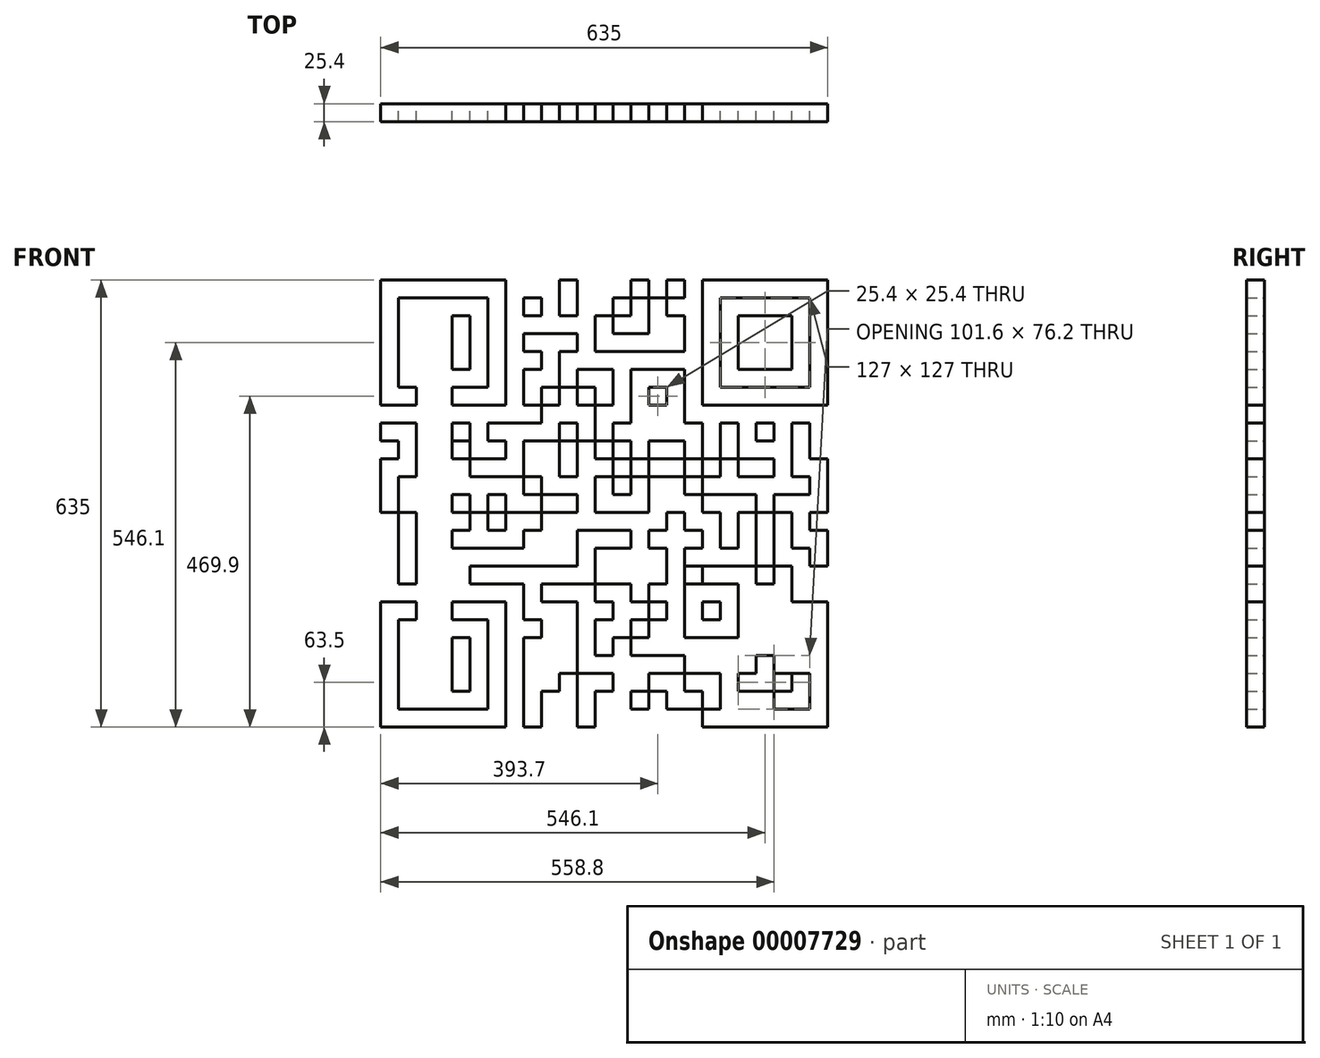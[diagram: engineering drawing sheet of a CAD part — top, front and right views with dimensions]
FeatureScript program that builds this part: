
annotation { "Feature Type Name" : "Feature", "Feature Type Description" : "" }
export const myFeature = defineFeature(function(context is Context, id is Id, definition is map)
    precondition{}
    {
        {
            var Q0;
            Q0=qCreatedBy(makeId("Front.planeOp"),FACE);
            var sketch = newSketch(context, id + "F0", { "sketchPlane" : qUnion([Q0])});
            skLineSegment(sketch, "E0", {"start": v(25.4, 635) * mm, "end": v(25.4, 0) * mm});
            skLineSegment(sketch, "E1", {"start": v(25.4, 0) * mm, "end": v(50.8, 0) * mm});
            skLineSegment(sketch, "E2", {"start": v(50.8, 0) * mm, "end": v(50.8, 635) * mm});
            skLineSegment(sketch, "E3.bottom", {"start": v(50.8, 635) * mm, "end": v(76.2, 635) * mm});
            skLineSegment(sketch, "E3.top", {"start": v(50.8, 0) * mm, "end": v(50.8, 0) * mm});
            skLineSegment(sketch, "E3.left", {"start": v(50.8, 635) * mm, "end": v(50.8, 0) * mm});
            skLineSegment(sketch, "E3.right", {"start": v(76.2, 635) * mm, "end": v(76.2, 0) * mm});
            skLineSegment(sketch, "E4.bottom", {"start": v(76.2, 0) * mm, "end": v(76.2, 0) * mm});
            skLineSegment(sketch, "E4.top", {"start": v(76.2, 635) * mm, "end": v(101.6, 635) * mm});
            skLineSegment(sketch, "E4.left", {"start": v(76.2, 0) * mm, "end": v(76.2, 635) * mm});
            skLineSegment(sketch, "E4.right", {"start": v(101.6, 0) * mm, "end": v(101.6, 0) * mm});
            skLineSegment(sketch, "E5.bottom", {"start": v(127, 635) * mm, "end": v(152.4, 635) * mm});
            skLineSegment(sketch, "E5.top", {"start": v(127, 0) * mm, "end": v(127, 0) * mm});
            skLineSegment(sketch, "E5.left", {"start": v(127, 635) * mm, "end": v(127, 0) * mm});
            skLineSegment(sketch, "E5.right", {"start": v(152.4, 635) * mm, "end": v(152.4, 0) * mm});
            skLineSegment(sketch, "E6.bottom", {"start": v(177.8, 0) * mm, "end": v(203.2, 0) * mm});
            skLineSegment(sketch, "E6.top", {"start": v(177.8, 635) * mm, "end": v(203.2, 635) * mm});
            skLineSegment(sketch, "E6.left", {"start": v(177.8, 0) * mm, "end": v(177.8, 0) * mm});
            skLineSegment(sketch, "E6.right", {"start": v(203.2, 0) * mm, "end": v(203.2, 635) * mm});
            skLineSegment(sketch, "E7.bottom", {"start": v(228.6, 635) * mm, "end": v(254, 635) * mm});
            skLineSegment(sketch, "E7.top", {"start": v(228.6, 0) * mm, "end": v(254, 0) * mm});
            skLineSegment(sketch, "E7.left", {"start": v(228.6, 635) * mm, "end": v(228.6, 0) * mm});
            skLineSegment(sketch, "E7.right", {"start": v(254, 635) * mm, "end": v(254, 0) * mm});
            skLineSegment(sketch, "E8.top", {"start": v(279.4, 635) * mm, "end": v(330.2, 635) * mm});
            skLineSegment(sketch, "E8.left", {"start": v(279.4, 0) * mm, "end": v(279.4, 635) * mm});
            skLineSegment(sketch, "E8.right", {"start": v(330.2, 0) * mm, "end": v(330.2, 635) * mm});
            skLineSegment(sketch, "E9.bottom", {"start": v(355.6, 635) * mm, "end": v(381, 635) * mm});
            skLineSegment(sketch, "E9.left", {"start": v(355.6, 635) * mm, "end": v(355.6, 0) * mm});
            skLineSegment(sketch, "E9.right", {"start": v(381, 635) * mm, "end": v(381, 0) * mm});
            skLineSegment(sketch, "E10.bottom", {"start": v(330.2, 0) * mm, "end": v(304.8, 0) * mm});
            skLineSegment(sketch, "E10.top", {"start": v(330.2, 635) * mm, "end": v(304.8, 635) * mm});
            skLineSegment(sketch, "E10.right", {"start": v(304.8, 0) * mm, "end": v(304.8, 635) * mm});
            skLineSegment(sketch, "E11.bottom", {"start": v(406.4, 635) * mm, "end": v(431.8, 635) * mm});
            skLineSegment(sketch, "E11.left", {"start": v(406.4, 635) * mm, "end": v(406.4, 0) * mm});
            skLineSegment(sketch, "E11.right", {"start": v(431.8, 635) * mm, "end": v(431.8, 0) * mm});
            skLineSegment(sketch, "E12.bottom", {"start": v(457.2, 635) * mm, "end": v(482.6, 635) * mm});
            skLineSegment(sketch, "E12.left", {"start": v(457.2, 635) * mm, "end": v(457.2, 0) * mm});
            skLineSegment(sketch, "E12.right", {"start": v(482.6, 635) * mm, "end": v(482.6, 0) * mm});
            skLineSegment(sketch, "E13.top", {"start": v(508, 635) * mm, "end": v(533.4, 635) * mm});
            skLineSegment(sketch, "E13.left", {"start": v(508, 0) * mm, "end": v(508, 635) * mm});
            skLineSegment(sketch, "E13.right", {"start": v(533.4, 0) * mm, "end": v(533.4, 635) * mm});
            skLineSegment(sketch, "E14.bottom", {"start": v(558.8, 635) * mm, "end": v(584.2, 635) * mm});
            skLineSegment(sketch, "E14.left", {"start": v(558.8, 635) * mm, "end": v(558.8, 0) * mm});
            skLineSegment(sketch, "E14.right", {"start": v(584.2, 635) * mm, "end": v(584.2, 0) * mm});
            skLineSegment(sketch, "E15.top", {"start": v(0, 609.6) * mm, "end": v(635, 609.6) * mm});
            skLineSegment(sketch, "E15.left", {"start": v(0, 635) * mm, "end": v(0, 609.6) * mm});
            skLineSegment(sketch, "E15.right", {"start": v(609.6, 635) * mm, "end": v(609.6, 609.6) * mm});
            skLineSegment(sketch, "E16.bottom", {"start": v(635, 584.2) * mm, "end": v(0, 584.2) * mm});
            skLineSegment(sketch, "E16.top", {"start": v(635, 558.8) * mm, "end": v(0, 558.8) * mm});
            skLineSegment(sketch, "E16.left", {"start": v(609.6, 584.2) * mm, "end": v(609.6, 558.8) * mm});
            skLineSegment(sketch, "E16.right", {"start": v(0, 584.2) * mm, "end": v(0, 558.8) * mm});
            skLineSegment(sketch, "E17.bottom", {"start": v(0, 533.4) * mm, "end": v(635, 533.4) * mm});
            skLineSegment(sketch, "E17.top", {"start": v(0, 508) * mm, "end": v(635, 508) * mm});
            skLineSegment(sketch, "E17.left", {"start": v(0, 533.4) * mm, "end": v(0, 508) * mm});
            skLineSegment(sketch, "E17.right", {"start": v(609.6, 533.4) * mm, "end": v(609.6, 508) * mm});
            skLineSegment(sketch, "E18.bottom", {"start": v(635, 482.6) * mm, "end": v(0, 482.6) * mm});
            skLineSegment(sketch, "E18.top", {"start": v(635, 457.2) * mm, "end": v(0, 457.2) * mm});
            skLineSegment(sketch, "E18.left", {"start": v(609.6, 482.6) * mm, "end": v(609.6, 457.2) * mm});
            skLineSegment(sketch, "E18.right", {"start": v(0, 482.6) * mm, "end": v(0, 457.2) * mm});
            skLineSegment(sketch, "E19.bottom", {"start": v(0, 431.8) * mm, "end": v(635, 431.8) * mm});
            skLineSegment(sketch, "E19.top", {"start": v(0, 406.4) * mm, "end": v(635, 406.4) * mm});
            skLineSegment(sketch, "E19.left", {"start": v(0, 431.8) * mm, "end": v(0, 406.4) * mm});
            skLineSegment(sketch, "E19.right", {"start": v(609.6, 431.8) * mm, "end": v(609.6, 406.4) * mm});
            skLineSegment(sketch, "E20.bottom", {"start": v(635, 381) * mm, "end": v(0, 381) * mm});
            skLineSegment(sketch, "E20.top", {"start": v(635, 355.6) * mm, "end": v(0, 355.6) * mm});
            skLineSegment(sketch, "E20.left", {"start": v(609.6, 381) * mm, "end": v(609.6, 355.6) * mm});
            skLineSegment(sketch, "E20.right", {"start": v(0, 381) * mm, "end": v(0, 355.6) * mm});
            skLineSegment(sketch, "E21.bottom", {"start": v(0, 330.2) * mm, "end": v(635, 330.2) * mm});
            skLineSegment(sketch, "E21.top", {"start": v(0, 304.8) * mm, "end": v(635, 304.8) * mm});
            skLineSegment(sketch, "E21.left", {"start": v(0, 330.2) * mm, "end": v(0, 304.8) * mm});
            skLineSegment(sketch, "E21.right", {"start": v(609.6, 330.2) * mm, "end": v(609.6, 304.8) * mm});
            skLineSegment(sketch, "E22.bottom", {"start": v(635, 279.4) * mm, "end": v(0, 279.4) * mm});
            skLineSegment(sketch, "E22.top", {"start": v(635, 254) * mm, "end": v(0, 254) * mm});
            skLineSegment(sketch, "E22.left", {"start": v(609.6, 279.4) * mm, "end": v(609.6, 254) * mm});
            skLineSegment(sketch, "E22.right", {"start": v(0, 279.4) * mm, "end": v(0, 254) * mm});
            skLineSegment(sketch, "E23.bottom", {"start": v(0, 228.6) * mm, "end": v(635, 228.6) * mm});
            skLineSegment(sketch, "E23.top", {"start": v(0, 203.2) * mm, "end": v(635, 203.2) * mm});
            skLineSegment(sketch, "E23.left", {"start": v(0, 228.6) * mm, "end": v(0, 203.2) * mm});
            skLineSegment(sketch, "E23.right", {"start": v(609.6, 228.6) * mm, "end": v(609.6, 203.2) * mm});
            skLineSegment(sketch, "E24.bottom", {"start": v(635, 177.8) * mm, "end": v(0, 177.8) * mm});
            skLineSegment(sketch, "E24.top", {"start": v(635, 152.4) * mm, "end": v(0, 152.4) * mm});
            skLineSegment(sketch, "E24.left", {"start": v(609.6, 177.8) * mm, "end": v(609.6, 152.4) * mm});
            skLineSegment(sketch, "E24.right", {"start": v(0, 177.8) * mm, "end": v(0, 152.4) * mm});
            skLineSegment(sketch, "E25.bottom", {"start": v(0, 127) * mm, "end": v(635, 127) * mm});
            skLineSegment(sketch, "E25.top", {"start": v(0, 101.6) * mm, "end": v(635, 101.6) * mm});
            skLineSegment(sketch, "E25.left", {"start": v(0, 127) * mm, "end": v(0, 101.6) * mm});
            skLineSegment(sketch, "E25.right", {"start": v(609.6, 127) * mm, "end": v(609.6, 101.6) * mm});
            skLineSegment(sketch, "E26.bottom", {"start": v(635, 76.2) * mm, "end": v(0, 76.2) * mm});
            skLineSegment(sketch, "E26.top", {"start": v(635, 50.8) * mm, "end": v(0, 50.8) * mm});
            skLineSegment(sketch, "E26.left", {"start": v(609.6, 76.2) * mm, "end": v(609.6, 50.8) * mm});
            skLineSegment(sketch, "E26.right", {"start": v(0, 76.2) * mm, "end": v(0, 50.8) * mm});
            skLineSegment(sketch, "E27.bottom", {"start": v(0, 25.4) * mm, "end": v(635, 25.4) * mm});
            skLineSegment(sketch, "E28", {"start": v(0, 635) * mm, "end": v(25.4, 635) * mm});
            skLineSegment(sketch, "E29", {"start": v(25.4, 635) * mm, "end": v(50.8, 635) * mm});
            skLineSegment(sketch, "E30", {"start": v(101.6, 635) * mm, "end": v(127, 635) * mm});
            skLineSegment(sketch, "E31", {"start": v(50.8, 0) * mm, "end": v(76.2, 0) * mm});
            skLineSegment(sketch, "E32", {"start": v(76.2, 0) * mm, "end": v(101.6, 0) * mm});
            skLineSegment(sketch, "E33", {"start": v(101.6, 0) * mm, "end": v(101.6, 635) * mm});
            skLineSegment(sketch, "E34", {"start": v(177.8, 0) * mm, "end": v(177.8, 635) * mm});
            skLineSegment(sketch, "E35", {"start": v(152.4, 635) * mm, "end": v(177.8, 635) * mm});
            skLineSegment(sketch, "E36", {"start": v(203.2, 635) * mm, "end": v(228.6, 635) * mm});
            skLineSegment(sketch, "E37", {"start": v(254, 635) * mm, "end": v(279.4, 635) * mm});
            skLineSegment(sketch, "E38", {"start": v(330.2, 635) * mm, "end": v(355.6, 635) * mm});
            skLineSegment(sketch, "E39", {"start": v(381, 635) * mm, "end": v(406.4, 635) * mm});
            skLineSegment(sketch, "E40", {"start": v(431.8, 635) * mm, "end": v(457.2, 635) * mm});
            skLineSegment(sketch, "E41", {"start": v(482.6, 635) * mm, "end": v(508, 635) * mm});
            skLineSegment(sketch, "E42", {"start": v(533.4, 635) * mm, "end": v(558.8, 635) * mm});
            skLineSegment(sketch, "E43", {"start": v(584.2, 635) * mm, "end": v(609.6, 635) * mm});
            skLineSegment(sketch, "E44", {"start": v(0, 609.6) * mm, "end": v(0, 584.2) * mm});
            skLineSegment(sketch, "E45", {"start": v(0, 558.8) * mm, "end": v(0, 533.4) * mm});
            skLineSegment(sketch, "E46", {"start": v(0, 508) * mm, "end": v(0, 482.6) * mm});
            skLineSegment(sketch, "E47", {"start": v(0, 457.2) * mm, "end": v(0, 431.8) * mm});
            skLineSegment(sketch, "E48", {"start": v(0, 406.4) * mm, "end": v(0, 381) * mm});
            skLineSegment(sketch, "E49", {"start": v(0, 355.6) * mm, "end": v(0, 330.2) * mm});
            skLineSegment(sketch, "E50", {"start": v(0, 304.8) * mm, "end": v(0, 279.4) * mm});
            skLineSegment(sketch, "E51", {"start": v(0, 254) * mm, "end": v(0, 228.6) * mm});
            skLineSegment(sketch, "E52", {"start": v(25.4, 0) * mm, "end": v(0, 0) * mm});
            skLineSegment(sketch, "E53", {"start": v(0, 0) * mm, "end": v(0, 25.4) * mm});
            skLineSegment(sketch, "E54", {"start": v(0, 50.8) * mm, "end": v(0, 25.4) * mm});
            skLineSegment(sketch, "E55", {"start": v(0, 76.2) * mm, "end": v(0, 101.6) * mm});
            skLineSegment(sketch, "E56", {"start": v(0, 127) * mm, "end": v(0, 152.4) * mm});
            skLineSegment(sketch, "E57", {"start": v(0, 177.8) * mm, "end": v(0, 203.2) * mm});
            skLineSegment(sketch, "E58", {"start": v(101.6, 0) * mm, "end": v(127, 0) * mm});
            skLineSegment(sketch, "E59", {"start": v(152.4, 0) * mm, "end": v(177.8, 0) * mm});
            skLineSegment(sketch, "E60", {"start": v(203.2, 0) * mm, "end": v(228.6, 0) * mm});
            skLineSegment(sketch, "E61", {"start": v(254, 0) * mm, "end": v(279.4, 0) * mm});
            skLineSegment(sketch, "E62", {"start": v(609.6, 609.6) * mm, "end": v(609.6, 584.2) * mm});
            skLineSegment(sketch, "E63", {"start": v(609.6, 558.8) * mm, "end": v(609.6, 533.4) * mm});
            skLineSegment(sketch, "E64", {"start": v(609.6, 508) * mm, "end": v(609.6, 482.6) * mm});
            skLineSegment(sketch, "E65", {"start": v(609.6, 25.4) * mm, "end": v(609.6, 0) * mm});
            skLineSegment(sketch, "E66", {"start": v(609.6, 25.4) * mm, "end": v(609.6, 50.8) * mm});
            skLineSegment(sketch, "E67", {"start": v(609.6, 76.2) * mm, "end": v(609.6, 101.6) * mm});
            skLineSegment(sketch, "E68", {"start": v(609.6, 127) * mm, "end": v(609.6, 152.4) * mm});
            skLineSegment(sketch, "E69", {"start": v(609.6, 177.8) * mm, "end": v(609.6, 203.2) * mm});
            skLineSegment(sketch, "E70", {"start": v(609.6, 228.6) * mm, "end": v(609.6, 254) * mm});
            skLineSegment(sketch, "E71", {"start": v(609.6, 279.4) * mm, "end": v(609.6, 304.8) * mm});
            skLineSegment(sketch, "E72", {"start": v(609.6, 381) * mm, "end": v(609.6, 406.4) * mm});
            skLineSegment(sketch, "E73", {"start": v(609.6, 431.8) * mm, "end": v(609.6, 457.2) * mm});
            skLineSegment(sketch, "E74", {"start": v(609.6, 355.6) * mm, "end": v(609.6, 330.2) * mm});
            skLineSegment(sketch, "E75", {"start": v(127, 0) * mm, "end": v(152.4, 0) * mm});
            skLineSegment(sketch, "E76", {"start": v(279.4, 0) * mm, "end": v(304.8, 0) * mm});
            skLineSegment(sketch, "E77", {"start": v(330.2, 0) * mm, "end": v(355.6, 0) * mm});
            skLineSegment(sketch, "E78", {"start": v(355.6, 0) * mm, "end": v(381, 0) * mm});
            skLineSegment(sketch, "E79", {"start": v(381, 0) * mm, "end": v(406.4, 0) * mm});
            skLineSegment(sketch, "E80", {"start": v(406.4, 0) * mm, "end": v(431.8, 0) * mm});
            skLineSegment(sketch, "E81", {"start": v(431.8, 0) * mm, "end": v(457.2, 0) * mm});
            skLineSegment(sketch, "E82", {"start": v(457.2, 0) * mm, "end": v(482.6, 0) * mm});
            skLineSegment(sketch, "E83", {"start": v(482.6, 0) * mm, "end": v(508, 0) * mm});
            skLineSegment(sketch, "E84", {"start": v(508, 0) * mm, "end": v(533.4, 0) * mm});
            skLineSegment(sketch, "E85", {"start": v(533.4, 0) * mm, "end": v(558.8, 0) * mm});
            skLineSegment(sketch, "E86", {"start": v(558.8, 0) * mm, "end": v(584.2, 0) * mm});
            skLineSegment(sketch, "E87", {"start": v(584.2, 0) * mm, "end": v(609.6, 0) * mm});
            skLineSegment(sketch, "E88.bottom", {"start": v(609.6, 635) * mm, "end": v(635, 635) * mm});
            skLineSegment(sketch, "E88.top", {"start": v(609.6, 0) * mm, "end": v(635, 0) * mm});
            skLineSegment(sketch, "E88.left", {"start": v(609.6, 635) * mm, "end": v(609.6, 0) * mm});
            skLineSegment(sketch, "E88.right", {"start": v(635, 635) * mm, "end": v(635, 0) * mm});
            skSolve(sketch);
        }
        {
            var Q0;
            {var subQ1=sQuery(id+"F0.wireOp",EDGE,"E88.bottom");Q0=makeQuery(id+"F0.imprint","IMPRINT",FACE,{"disambiguationData":[TD([[makeQuery(id+"F0.imprint","IMPRINT",EDGE,{"derivedFrom":subQ1}),-1.0]])]});}
            var Q1;
            {var subQ1=sQuery(id+"F0.wireOp",EDGE,"E15.left");Q1=makeQuery(id+"F0.imprint","IMPRINT",FACE,{"disambiguationData":[TD([[makeQuery(id+"F0.imprint","IMPRINT",EDGE,{"derivedFrom":subQ1}),1.0]])]});}
            var Q2;
            {var subQ0=sQuery(id+"F0.wireOp",EDGE,"E29");Q2=makeQuery(id+"F0.imprint","IMPRINT",FACE,{"disambiguationData":[TD([[makeQuery(id+"F0.imprint","IMPRINT",EDGE,{"derivedFrom":subQ0}),-1.0]])]});}
            var Q3;
            {var subQ5=sQuery(id+"F0.wireOp",EDGE,"E3.bottom");Q3=makeQuery(id+"F0.imprint","IMPRINT",FACE,{"disambiguationData":[TD([[makeQuery(id+"F0.imprint","IMPRINT",EDGE,{"derivedFrom":subQ5}),-1.0]])]});}
            var Q4;
            {var subQ3=sQuery(id+"F0.wireOp",EDGE,"E4.top");Q4=makeQuery(id+"F0.imprint","IMPRINT",FACE,{"disambiguationData":[TD([[makeQuery(id+"F0.imprint","IMPRINT",EDGE,{"derivedFrom":subQ3}),-1.0]])]});}
            var Q5;
            {var subQ3=sQuery(id+"F0.wireOp",EDGE,"E30");Q5=makeQuery(id+"F0.imprint","IMPRINT",FACE,{"disambiguationData":[TD([[makeQuery(id+"F0.imprint","IMPRINT",EDGE,{"derivedFrom":subQ3}),-1.0]])]});}
            var Q6;
            {var subQ5=sQuery(id+"F0.wireOp",EDGE,"E5.bottom");Q6=makeQuery(id+"F0.imprint","IMPRINT",FACE,{"disambiguationData":[TD([[makeQuery(id+"F0.imprint","IMPRINT",EDGE,{"derivedFrom":subQ5}),-1.0]])]});}
            var Q7;
            {var subQ3=sQuery(id+"F0.wireOp",EDGE,"E3.left");var subQ5=sQuery(id+"F0.wireOp",EDGE,"E16.bottom");var subQ7=makeQuery(id+"F0.imprint","INTERSECT",VERTEX,{"derivedFrom":[subQ3,subQ5]});Q7=makeQuery(id+"F0.imprint","IMPRINT",FACE,{"disambiguationData":[TD([[makeQuery(id+"F0.imprint","IMPRINT",EDGE,{"disambiguationData":[TD([[subQ7,-1.0]])],"derivedFrom":subQ3}),1.0]])]});}
            var Q8;
            {var subQ1=sQuery(id+"F0.wireOp",EDGE,"E16.top");var subQ5=sQuery(id+"F0.wireOp",EDGE,"E4.left");var subQ6=makeQuery(id+"F0.imprint","INTERSECT",VERTEX,{"derivedFrom":[subQ5,subQ1]});Q8=makeQuery(id+"F0.imprint","IMPRINT",FACE,{"disambiguationData":[TD([[makeQuery(id+"F0.imprint","IMPRINT",EDGE,{"disambiguationData":[TD([[subQ6,-1.0]])],"derivedFrom":subQ5}),-1.0]])]});}
            var Q9;
            {var subQ3=sQuery(id+"F0.wireOp",EDGE,"E5.left");var subQ5=sQuery(id+"F0.wireOp",EDGE,"E16.bottom");var subQ7=makeQuery(id+"F0.imprint","INTERSECT",VERTEX,{"derivedFrom":[subQ3,subQ5]});Q9=makeQuery(id+"F0.imprint","IMPRINT",FACE,{"disambiguationData":[TD([[makeQuery(id+"F0.imprint","IMPRINT",EDGE,{"disambiguationData":[TD([[subQ7,-1.0]])],"derivedFrom":subQ3}),-1.0]])]});}
            var Q10;
            {var subQ3=sQuery(id+"F0.wireOp",EDGE,"E16.top");var subQ5=sQuery(id+"F0.wireOp",EDGE,"E5.left");var subQ7=makeQuery(id+"F0.imprint","INTERSECT",VERTEX,{"derivedFrom":[subQ5,subQ3]});Q10=makeQuery(id+"F0.imprint","IMPRINT",FACE,{"disambiguationData":[TD([[makeQuery(id+"F0.imprint","IMPRINT",EDGE,{"disambiguationData":[TD([[subQ7,-1.0]])],"derivedFrom":subQ5}),-1.0]])]});}
            var Q11;
            {var subQ1=sQuery(id+"F0.wireOp",EDGE,"E17.bottom");var subQ5=sQuery(id+"F0.wireOp",EDGE,"E4.left");var subQ6=makeQuery(id+"F0.imprint","INTERSECT",VERTEX,{"derivedFrom":[subQ5,subQ1]});Q11=makeQuery(id+"F0.imprint","IMPRINT",FACE,{"disambiguationData":[TD([[makeQuery(id+"F0.imprint","IMPRINT",EDGE,{"disambiguationData":[TD([[subQ6,-1.0]])],"derivedFrom":subQ5}),-1.0]])]});}
            var Q12;
            {var subQ3=sQuery(id+"F0.wireOp",EDGE,"E3.left");var subQ5=sQuery(id+"F0.wireOp",EDGE,"E16.top");var subQ7=makeQuery(id+"F0.imprint","INTERSECT",VERTEX,{"derivedFrom":[subQ3,subQ5]});Q12=makeQuery(id+"F0.imprint","IMPRINT",FACE,{"disambiguationData":[TD([[makeQuery(id+"F0.imprint","IMPRINT",EDGE,{"disambiguationData":[TD([[subQ7,-1.0]])],"derivedFrom":subQ3}),1.0]])]});}
            var Q13;
            {var subQ0=sQuery(id+"F0.wireOp",EDGE,"E17.bottom");var subQ3=sQuery(id+"F0.wireOp",EDGE,"E3.left");var subQ4=makeQuery(id+"F0.imprint","INTERSECT",VERTEX,{"derivedFrom":[subQ3,subQ0]});Q13=makeQuery(id+"F0.imprint","IMPRINT",FACE,{"disambiguationData":[TD([[makeQuery(id+"F0.imprint","IMPRINT",EDGE,{"disambiguationData":[TD([[subQ4,-1.0]])],"derivedFrom":subQ3}),1.0]])]});}
            var Q14;
            {var subQ1=sQuery(id+"F0.wireOp",EDGE,"E17.top");var subQ5=sQuery(id+"F0.wireOp",EDGE,"E4.left");var subQ6=makeQuery(id+"F0.imprint","INTERSECT",VERTEX,{"derivedFrom":[subQ5,subQ1]});Q14=makeQuery(id+"F0.imprint","IMPRINT",FACE,{"disambiguationData":[TD([[makeQuery(id+"F0.imprint","IMPRINT",EDGE,{"disambiguationData":[TD([[subQ6,-1.0]])],"derivedFrom":subQ5}),-1.0]])]});}
            var Q15;
            {var subQ3=sQuery(id+"F0.wireOp",EDGE,"E17.bottom");var subQ5=sQuery(id+"F0.wireOp",EDGE,"E5.left");var subQ7=makeQuery(id+"F0.imprint","INTERSECT",VERTEX,{"derivedFrom":[subQ5,subQ3]});Q15=makeQuery(id+"F0.imprint","IMPRINT",FACE,{"disambiguationData":[TD([[makeQuery(id+"F0.imprint","IMPRINT",EDGE,{"disambiguationData":[TD([[subQ7,-1.0]])],"derivedFrom":subQ5}),-1.0]])]});}
            var Q16;
            {var subQ0=sQuery(id+"F0.wireOp",EDGE,"E44");Q16=makeQuery(id+"F0.imprint","IMPRINT",FACE,{"disambiguationData":[TD([[makeQuery(id+"F0.imprint","IMPRINT",EDGE,{"derivedFrom":subQ0}),1.0]])]});}
            var Q17;
            {var subQ0=sQuery(id+"F0.wireOp",EDGE,"E16.right");Q17=makeQuery(id+"F0.imprint","IMPRINT",FACE,{"disambiguationData":[TD([[makeQuery(id+"F0.imprint","IMPRINT",EDGE,{"derivedFrom":subQ0}),1.0]])]});}
            var Q18;
            {var subQ0=sQuery(id+"F0.wireOp",EDGE,"E45");Q18=makeQuery(id+"F0.imprint","IMPRINT",FACE,{"disambiguationData":[TD([[makeQuery(id+"F0.imprint","IMPRINT",EDGE,{"derivedFrom":subQ0}),1.0]])]});}
            var Q19;
            {var subQ0=sQuery(id+"F0.wireOp",EDGE,"E17.left");Q19=makeQuery(id+"F0.imprint","IMPRINT",FACE,{"disambiguationData":[TD([[makeQuery(id+"F0.imprint","IMPRINT",EDGE,{"derivedFrom":subQ0}),1.0]])]});}
            var Q20;
            {var subQ0=sQuery(id+"F0.wireOp",EDGE,"E46");Q20=makeQuery(id+"F0.imprint","IMPRINT",FACE,{"disambiguationData":[TD([[makeQuery(id+"F0.imprint","IMPRINT",EDGE,{"derivedFrom":subQ0}),1.0]])]});}
            var Q21;
            {var subQ0=sQuery(id+"F0.wireOp",EDGE,"E18.right");Q21=makeQuery(id+"F0.imprint","IMPRINT",FACE,{"disambiguationData":[TD([[makeQuery(id+"F0.imprint","IMPRINT",EDGE,{"derivedFrom":subQ0}),1.0]])]});}
            var Q22;
            {var subQ3=sQuery(id+"F0.wireOp",EDGE,"E0");var subQ5=sQuery(id+"F0.wireOp",EDGE,"E18.bottom");var subQ7=makeQuery(id+"F0.imprint","INTERSECT",VERTEX,{"derivedFrom":[subQ3,subQ5]});Q22=makeQuery(id+"F0.imprint","IMPRINT",FACE,{"disambiguationData":[TD([[makeQuery(id+"F0.imprint","IMPRINT",EDGE,{"disambiguationData":[TD([[subQ7,-1.0]])],"derivedFrom":subQ3}),1.0]])]});}
            var Q23;
            {var subQ3=sQuery(id+"F0.wireOp",EDGE,"E3.left");var subQ5=sQuery(id+"F0.wireOp",EDGE,"E18.bottom");var subQ7=makeQuery(id+"F0.imprint","INTERSECT",VERTEX,{"derivedFrom":[subQ3,subQ5]});Q23=makeQuery(id+"F0.imprint","IMPRINT",FACE,{"disambiguationData":[TD([[makeQuery(id+"F0.imprint","IMPRINT",EDGE,{"disambiguationData":[TD([[subQ7,-1.0]])],"derivedFrom":subQ3}),1.0]])]});}
            var Q24;
            {var subQ1=sQuery(id+"F0.wireOp",EDGE,"E18.top");var subQ5=sQuery(id+"F0.wireOp",EDGE,"E4.left");var subQ6=makeQuery(id+"F0.imprint","INTERSECT",VERTEX,{"derivedFrom":[subQ5,subQ1]});Q24=makeQuery(id+"F0.imprint","IMPRINT",FACE,{"disambiguationData":[TD([[makeQuery(id+"F0.imprint","IMPRINT",EDGE,{"disambiguationData":[TD([[subQ6,-1.0]])],"derivedFrom":subQ5}),-1.0]])]});}
            var Q25;
            {var subQ3=sQuery(id+"F0.wireOp",EDGE,"E5.left");var subQ5=sQuery(id+"F0.wireOp",EDGE,"E18.bottom");var subQ7=makeQuery(id+"F0.imprint","INTERSECT",VERTEX,{"derivedFrom":[subQ3,subQ5]});Q25=makeQuery(id+"F0.imprint","IMPRINT",FACE,{"disambiguationData":[TD([[makeQuery(id+"F0.imprint","IMPRINT",EDGE,{"disambiguationData":[TD([[subQ7,-1.0]])],"derivedFrom":subQ3}),-1.0]])]});}
            var Q26;
            {var subQ0=sQuery(id+"F0.wireOp",EDGE,"E18.bottom");var subQ3=sQuery(id+"F0.wireOp",EDGE,"E5.left");var subQ4=makeQuery(id+"F0.imprint","INTERSECT",VERTEX,{"derivedFrom":[subQ3,subQ0]});Q26=makeQuery(id+"F0.imprint","IMPRINT",FACE,{"disambiguationData":[TD([[makeQuery(id+"F0.imprint","IMPRINT",EDGE,{"disambiguationData":[TD([[subQ4,-1.0]])],"derivedFrom":subQ3}),1.0]])]});}
            var Q27;
            {var subQ3=sQuery(id+"F0.wireOp",EDGE,"E18.bottom");var subQ5=sQuery(id+"F0.wireOp",EDGE,"E5.right");var subQ7=makeQuery(id+"F0.imprint","INTERSECT",VERTEX,{"derivedFrom":[subQ5,subQ3]});Q27=makeQuery(id+"F0.imprint","IMPRINT",FACE,{"disambiguationData":[TD([[makeQuery(id+"F0.imprint","IMPRINT",EDGE,{"disambiguationData":[TD([[subQ7,-1.0]])],"derivedFrom":subQ5}),1.0]])]});}
            var Q28;
            {var subQ3=sQuery(id+"F0.wireOp",EDGE,"E17.top");var subQ5=sQuery(id+"F0.wireOp",EDGE,"E5.right");var subQ7=makeQuery(id+"F0.imprint","INTERSECT",VERTEX,{"derivedFrom":[subQ5,subQ3]});Q28=makeQuery(id+"F0.imprint","IMPRINT",FACE,{"disambiguationData":[TD([[makeQuery(id+"F0.imprint","IMPRINT",EDGE,{"disambiguationData":[TD([[subQ7,-1.0]])],"derivedFrom":subQ5}),1.0]])]});}
            var Q29;
            {var subQ3=sQuery(id+"F0.wireOp",EDGE,"E17.bottom");var subQ5=sQuery(id+"F0.wireOp",EDGE,"E5.right");var subQ7=makeQuery(id+"F0.imprint","INTERSECT",VERTEX,{"derivedFrom":[subQ5,subQ3]});Q29=makeQuery(id+"F0.imprint","IMPRINT",FACE,{"disambiguationData":[TD([[makeQuery(id+"F0.imprint","IMPRINT",EDGE,{"disambiguationData":[TD([[subQ7,-1.0]])],"derivedFrom":subQ5}),1.0]])]});}
            var Q30;
            {var subQ3=sQuery(id+"F0.wireOp",EDGE,"E16.top");var subQ5=sQuery(id+"F0.wireOp",EDGE,"E5.right");var subQ7=makeQuery(id+"F0.imprint","INTERSECT",VERTEX,{"derivedFrom":[subQ5,subQ3]});Q30=makeQuery(id+"F0.imprint","IMPRINT",FACE,{"disambiguationData":[TD([[makeQuery(id+"F0.imprint","IMPRINT",EDGE,{"disambiguationData":[TD([[subQ7,-1.0]])],"derivedFrom":subQ5}),1.0]])]});}
            var Q31;
            {var subQ3=sQuery(id+"F0.wireOp",EDGE,"E5.right");var subQ5=sQuery(id+"F0.wireOp",EDGE,"E16.bottom");var subQ7=makeQuery(id+"F0.imprint","INTERSECT",VERTEX,{"derivedFrom":[subQ3,subQ5]});Q31=makeQuery(id+"F0.imprint","IMPRINT",FACE,{"disambiguationData":[TD([[makeQuery(id+"F0.imprint","IMPRINT",EDGE,{"disambiguationData":[TD([[subQ7,-1.0]])],"derivedFrom":subQ3}),1.0]])]});}
            var Q32;
            {var subQ3=sQuery(id+"F0.wireOp",EDGE,"E15.top");var subQ5=sQuery(id+"F0.wireOp",EDGE,"E5.right");var subQ7=makeQuery(id+"F0.imprint","INTERSECT",VERTEX,{"derivedFrom":[subQ5,subQ3]});Q32=makeQuery(id+"F0.imprint","IMPRINT",FACE,{"disambiguationData":[TD([[makeQuery(id+"F0.imprint","IMPRINT",EDGE,{"disambiguationData":[TD([[subQ7,-1.0]])],"derivedFrom":subQ5}),1.0]])]});}
            var Q33;
            {var subQ0=sQuery(id+"F0.wireOp",EDGE,"E35");Q33=makeQuery(id+"F0.imprint","IMPRINT",FACE,{"disambiguationData":[TD([[makeQuery(id+"F0.imprint","IMPRINT",EDGE,{"derivedFrom":subQ0}),-1.0]])]});}
            var Q34;
            {var subQ0=sQuery(id+"F0.wireOp",EDGE,"E16.bottom");var subQ3=sQuery(id+"F0.wireOp",EDGE,"E6.right");var subQ4=makeQuery(id+"F0.imprint","INTERSECT",VERTEX,{"derivedFrom":[subQ3,subQ0]});Q34=makeQuery(id+"F0.imprint","IMPRINT",FACE,{"disambiguationData":[TD([[makeQuery(id+"F0.imprint","IMPRINT",EDGE,{"disambiguationData":[TD([[subQ4,-1.0]])],"derivedFrom":subQ3}),-1.0]])]});}
            var Q35;
            {var subQ0=sQuery(id+"F0.wireOp",EDGE,"E37");Q35=makeQuery(id+"F0.imprint","IMPRINT",FACE,{"disambiguationData":[TD([[makeQuery(id+"F0.imprint","IMPRINT",EDGE,{"derivedFrom":subQ0}),-1.0]])]});}
            var Q36;
            {var subQ3=sQuery(id+"F0.wireOp",EDGE,"E7.right");var subQ5=sQuery(id+"F0.wireOp",EDGE,"E15.top");var subQ7=makeQuery(id+"F0.imprint","INTERSECT",VERTEX,{"derivedFrom":[subQ3,subQ5]});Q36=makeQuery(id+"F0.imprint","IMPRINT",FACE,{"disambiguationData":[TD([[makeQuery(id+"F0.imprint","IMPRINT",EDGE,{"disambiguationData":[TD([[subQ7,-1.0]])],"derivedFrom":subQ3}),1.0]])]});}
            var Q37;
            {var subQ5=sQuery(id+"F0.wireOp",EDGE,"E10.top");Q37=makeQuery(id+"F0.imprint","IMPRINT",FACE,{"disambiguationData":[TD([[makeQuery(id+"F0.imprint","IMPRINT",EDGE,{"derivedFrom":subQ5}),1.0]])]});}
            var Q38;
            {var subQ3=sQuery(id+"F0.wireOp",EDGE,"E9.left");var subQ5=sQuery(id+"F0.wireOp",EDGE,"E15.top");var subQ7=makeQuery(id+"F0.imprint","INTERSECT",VERTEX,{"derivedFrom":[subQ3,subQ5]});Q38=makeQuery(id+"F0.imprint","IMPRINT",FACE,{"disambiguationData":[TD([[makeQuery(id+"F0.imprint","IMPRINT",EDGE,{"disambiguationData":[TD([[subQ7,-1.0]])],"derivedFrom":subQ3}),-1.0]])]});}
            var Q39;
            {var subQ5=sQuery(id+"F0.wireOp",EDGE,"E9.bottom");Q39=makeQuery(id+"F0.imprint","IMPRINT",FACE,{"disambiguationData":[TD([[makeQuery(id+"F0.imprint","IMPRINT",EDGE,{"derivedFrom":subQ5}),-1.0]])]});}
            var Q40;
            {var subQ3=sQuery(id+"F0.wireOp",EDGE,"E9.right");var subQ5=sQuery(id+"F0.wireOp",EDGE,"E15.top");var subQ7=makeQuery(id+"F0.imprint","INTERSECT",VERTEX,{"derivedFrom":[subQ3,subQ5]});Q40=makeQuery(id+"F0.imprint","IMPRINT",FACE,{"disambiguationData":[TD([[makeQuery(id+"F0.imprint","IMPRINT",EDGE,{"disambiguationData":[TD([[subQ7,-1.0]])],"derivedFrom":subQ3}),1.0]])]});}
            var Q41;
            {var subQ5=sQuery(id+"F0.wireOp",EDGE,"E11.bottom");Q41=makeQuery(id+"F0.imprint","IMPRINT",FACE,{"disambiguationData":[TD([[makeQuery(id+"F0.imprint","IMPRINT",EDGE,{"derivedFrom":subQ5}),-1.0]])]});}
            var Q42;
            {var subQ3=sQuery(id+"F0.wireOp",EDGE,"E9.right");var subQ5=sQuery(id+"F0.wireOp",EDGE,"E16.bottom");var subQ7=makeQuery(id+"F0.imprint","INTERSECT",VERTEX,{"derivedFrom":[subQ3,subQ5]});Q42=makeQuery(id+"F0.imprint","IMPRINT",FACE,{"disambiguationData":[TD([[makeQuery(id+"F0.imprint","IMPRINT",EDGE,{"disambiguationData":[TD([[subQ7,-1.0]])],"derivedFrom":subQ3}),1.0]])]});}
            var Q43;
            {var subQ3=sQuery(id+"F0.wireOp",EDGE,"E9.right");var subQ5=sQuery(id+"F0.wireOp",EDGE,"E16.top");var subQ7=makeQuery(id+"F0.imprint","INTERSECT",VERTEX,{"derivedFrom":[subQ3,subQ5]});Q43=makeQuery(id+"F0.imprint","IMPRINT",FACE,{"disambiguationData":[TD([[makeQuery(id+"F0.imprint","IMPRINT",EDGE,{"disambiguationData":[TD([[subQ7,-1.0]])],"derivedFrom":subQ3}),1.0]])]});}
            var Q44;
            {var subQ3=sQuery(id+"F0.wireOp",EDGE,"E11.left");var subQ5=sQuery(id+"F0.wireOp",EDGE,"E16.bottom");var subQ7=makeQuery(id+"F0.imprint","INTERSECT",VERTEX,{"derivedFrom":[subQ3,subQ5]});Q44=makeQuery(id+"F0.imprint","IMPRINT",FACE,{"disambiguationData":[TD([[makeQuery(id+"F0.imprint","IMPRINT",EDGE,{"disambiguationData":[TD([[subQ7,-1.0]])],"derivedFrom":subQ3}),1.0]])]});}
            var Q45;
            {var subQ3=sQuery(id+"F0.wireOp",EDGE,"E11.left");var subQ5=sQuery(id+"F0.wireOp",EDGE,"E16.top");var subQ7=makeQuery(id+"F0.imprint","INTERSECT",VERTEX,{"derivedFrom":[subQ3,subQ5]});Q45=makeQuery(id+"F0.imprint","IMPRINT",FACE,{"disambiguationData":[TD([[makeQuery(id+"F0.imprint","IMPRINT",EDGE,{"disambiguationData":[TD([[subQ7,-1.0]])],"derivedFrom":subQ3}),1.0]])]});}
            var Q46;
            {var subQ3=sQuery(id+"F0.wireOp",EDGE,"E9.left");var subQ5=sQuery(id+"F0.wireOp",EDGE,"E16.top");var subQ7=makeQuery(id+"F0.imprint","INTERSECT",VERTEX,{"derivedFrom":[subQ3,subQ5]});Q46=makeQuery(id+"F0.imprint","IMPRINT",FACE,{"disambiguationData":[TD([[makeQuery(id+"F0.imprint","IMPRINT",EDGE,{"disambiguationData":[TD([[subQ7,-1.0]])],"derivedFrom":subQ3}),1.0]])]});}
            var Q47;
            {var subQ0=sQuery(id+"F0.wireOp",EDGE,"E16.top");var subQ3=sQuery(id+"F0.wireOp",EDGE,"E9.left");var subQ4=makeQuery(id+"F0.imprint","INTERSECT",VERTEX,{"derivedFrom":[subQ3,subQ0]});Q47=makeQuery(id+"F0.imprint","IMPRINT",FACE,{"disambiguationData":[TD([[makeQuery(id+"F0.imprint","IMPRINT",EDGE,{"disambiguationData":[TD([[subQ4,-1.0]])],"derivedFrom":subQ3}),-1.0]])]});}
            var Q48;
            {var subQ0=sQuery(id+"F0.wireOp",EDGE,"E17.bottom");var subQ3=sQuery(id+"F0.wireOp",EDGE,"E8.right");var subQ4=makeQuery(id+"F0.imprint","INTERSECT",VERTEX,{"derivedFrom":[subQ3,subQ0]});Q48=makeQuery(id+"F0.imprint","IMPRINT",FACE,{"disambiguationData":[TD([[makeQuery(id+"F0.imprint","IMPRINT",EDGE,{"disambiguationData":[TD([[subQ4,-1.0]])],"derivedFrom":subQ3}),1.0]])]});}
            var Q49;
            {var subQ0=sQuery(id+"F0.wireOp",EDGE,"E16.top");var subQ3=sQuery(id+"F0.wireOp",EDGE,"E8.right");var subQ4=makeQuery(id+"F0.imprint","INTERSECT",VERTEX,{"derivedFrom":[subQ3,subQ0]});Q49=makeQuery(id+"F0.imprint","IMPRINT",FACE,{"disambiguationData":[TD([[makeQuery(id+"F0.imprint","IMPRINT",EDGE,{"disambiguationData":[TD([[subQ4,-1.0]])],"derivedFrom":subQ3}),1.0]])]});}
            var Q50;
            {var subQ0=sQuery(id+"F0.wireOp",EDGE,"E17.bottom");var subQ3=sQuery(id+"F0.wireOp",EDGE,"E6.right");var subQ4=makeQuery(id+"F0.imprint","INTERSECT",VERTEX,{"derivedFrom":[subQ3,subQ0]});Q50=makeQuery(id+"F0.imprint","IMPRINT",FACE,{"disambiguationData":[TD([[makeQuery(id+"F0.imprint","IMPRINT",EDGE,{"disambiguationData":[TD([[subQ4,-1.0]])],"derivedFrom":subQ3}),-1.0]])]});}
            var Q51;
            {var subQ3=sQuery(id+"F0.wireOp",EDGE,"E7.left");var subQ5=sQuery(id+"F0.wireOp",EDGE,"E16.top");var subQ7=makeQuery(id+"F0.imprint","INTERSECT",VERTEX,{"derivedFrom":[subQ3,subQ5]});Q51=makeQuery(id+"F0.imprint","IMPRINT",FACE,{"disambiguationData":[TD([[makeQuery(id+"F0.imprint","IMPRINT",EDGE,{"disambiguationData":[TD([[subQ7,-1.0]])],"derivedFrom":subQ3}),1.0]])]});}
            var Q52;
            {var subQ3=sQuery(id+"F0.wireOp",EDGE,"E7.right");var subQ5=sQuery(id+"F0.wireOp",EDGE,"E16.top");var subQ7=makeQuery(id+"F0.imprint","INTERSECT",VERTEX,{"derivedFrom":[subQ3,subQ5]});Q52=makeQuery(id+"F0.imprint","IMPRINT",FACE,{"disambiguationData":[TD([[makeQuery(id+"F0.imprint","IMPRINT",EDGE,{"disambiguationData":[TD([[subQ7,-1.0]])],"derivedFrom":subQ3}),1.0]])]});}
            var Q53;
            {var subQ3=sQuery(id+"F0.wireOp",EDGE,"E7.left");var subQ5=sQuery(id+"F0.wireOp",EDGE,"E17.bottom");var subQ7=makeQuery(id+"F0.imprint","INTERSECT",VERTEX,{"derivedFrom":[subQ3,subQ5]});Q53=makeQuery(id+"F0.imprint","IMPRINT",FACE,{"disambiguationData":[TD([[makeQuery(id+"F0.imprint","IMPRINT",EDGE,{"disambiguationData":[TD([[subQ7,-1.0]])],"derivedFrom":subQ3}),1.0]])]});}
            var Q54;
            {var subQ0=sQuery(id+"F0.wireOp",EDGE,"E17.top");var subQ3=sQuery(id+"F0.wireOp",EDGE,"E7.left");var subQ4=makeQuery(id+"F0.imprint","INTERSECT",VERTEX,{"derivedFrom":[subQ3,subQ0]});Q54=makeQuery(id+"F0.imprint","IMPRINT",FACE,{"disambiguationData":[TD([[makeQuery(id+"F0.imprint","IMPRINT",EDGE,{"disambiguationData":[TD([[subQ4,-1.0]])],"derivedFrom":subQ3}),1.0]])]});}
            var Q55;
            {var subQ0=sQuery(id+"F0.wireOp",EDGE,"E18.bottom");var subQ3=sQuery(id+"F0.wireOp",EDGE,"E6.right");var subQ4=makeQuery(id+"F0.imprint","INTERSECT",VERTEX,{"derivedFrom":[subQ3,subQ0]});Q55=makeQuery(id+"F0.imprint","IMPRINT",FACE,{"disambiguationData":[TD([[makeQuery(id+"F0.imprint","IMPRINT",EDGE,{"disambiguationData":[TD([[subQ4,-1.0]])],"derivedFrom":subQ3}),-1.0]])]});}
            var Q56;
            {var subQ0=sQuery(id+"F0.wireOp",EDGE,"E18.top");var subQ3=sQuery(id+"F0.wireOp",EDGE,"E6.right");var subQ4=makeQuery(id+"F0.imprint","INTERSECT",VERTEX,{"derivedFrom":[subQ3,subQ0]});Q56=makeQuery(id+"F0.imprint","IMPRINT",FACE,{"disambiguationData":[TD([[makeQuery(id+"F0.imprint","IMPRINT",EDGE,{"disambiguationData":[TD([[subQ4,-1.0]])],"derivedFrom":subQ3}),-1.0]])]});}
            var Q57;
            {var subQ3=sQuery(id+"F0.wireOp",EDGE,"E7.right");var subQ5=sQuery(id+"F0.wireOp",EDGE,"E18.bottom");var subQ7=makeQuery(id+"F0.imprint","INTERSECT",VERTEX,{"derivedFrom":[subQ3,subQ5]});Q57=makeQuery(id+"F0.imprint","IMPRINT",FACE,{"disambiguationData":[TD([[makeQuery(id+"F0.imprint","IMPRINT",EDGE,{"disambiguationData":[TD([[subQ7,-1.0]])],"derivedFrom":subQ3}),1.0]])]});}
            var Q58;
            {var subQ3=sQuery(id+"F0.wireOp",EDGE,"E7.left");var subQ5=sQuery(id+"F0.wireOp",EDGE,"E18.top");var subQ7=makeQuery(id+"F0.imprint","INTERSECT",VERTEX,{"derivedFrom":[subQ3,subQ5]});Q58=makeQuery(id+"F0.imprint","IMPRINT",FACE,{"disambiguationData":[TD([[makeQuery(id+"F0.imprint","IMPRINT",EDGE,{"disambiguationData":[TD([[subQ7,-1.0]])],"derivedFrom":subQ3}),1.0]])]});}
            var Q59;
            {var subQ3=sQuery(id+"F0.wireOp",EDGE,"E7.right");var subQ5=sQuery(id+"F0.wireOp",EDGE,"E18.top");var subQ7=makeQuery(id+"F0.imprint","INTERSECT",VERTEX,{"derivedFrom":[subQ3,subQ5]});Q59=makeQuery(id+"F0.imprint","IMPRINT",FACE,{"disambiguationData":[TD([[makeQuery(id+"F0.imprint","IMPRINT",EDGE,{"disambiguationData":[TD([[subQ7,-1.0]])],"derivedFrom":subQ3}),1.0]])]});}
            var Q60;
            {var subQ0=sQuery(id+"F0.wireOp",EDGE,"E19.bottom");var subQ3=sQuery(id+"F0.wireOp",EDGE,"E8.left");var subQ4=makeQuery(id+"F0.imprint","INTERSECT",VERTEX,{"derivedFrom":[subQ3,subQ0]});Q60=makeQuery(id+"F0.imprint","IMPRINT",FACE,{"disambiguationData":[TD([[makeQuery(id+"F0.imprint","IMPRINT",EDGE,{"disambiguationData":[TD([[subQ4,-1.0]])],"derivedFrom":subQ3}),-1.0]])]});}
            var Q61;
            {var subQ0=sQuery(id+"F0.wireOp",EDGE,"E18.bottom");var subQ3=sQuery(id+"F0.wireOp",EDGE,"E8.left");var subQ4=makeQuery(id+"F0.imprint","INTERSECT",VERTEX,{"derivedFrom":[subQ3,subQ0]});Q61=makeQuery(id+"F0.imprint","IMPRINT",FACE,{"disambiguationData":[TD([[makeQuery(id+"F0.imprint","IMPRINT",EDGE,{"disambiguationData":[TD([[subQ4,-1.0]])],"derivedFrom":subQ3}),-1.0]])]});}
            var Q62;
            {var subQ0=sQuery(id+"F0.wireOp",EDGE,"E18.bottom");var subQ3=sQuery(id+"F0.wireOp",EDGE,"E8.right");var subQ4=makeQuery(id+"F0.imprint","INTERSECT",VERTEX,{"derivedFrom":[subQ3,subQ0]});Q62=makeQuery(id+"F0.imprint","IMPRINT",FACE,{"disambiguationData":[TD([[makeQuery(id+"F0.imprint","IMPRINT",EDGE,{"disambiguationData":[TD([[subQ4,-1.0]])],"derivedFrom":subQ3}),1.0]])]});}
            var Q63;
            {var subQ0=sQuery(id+"F0.wireOp",EDGE,"E18.top");var subQ3=sQuery(id+"F0.wireOp",EDGE,"E8.right");var subQ4=makeQuery(id+"F0.imprint","INTERSECT",VERTEX,{"derivedFrom":[subQ3,subQ0]});Q63=makeQuery(id+"F0.imprint","IMPRINT",FACE,{"disambiguationData":[TD([[makeQuery(id+"F0.imprint","IMPRINT",EDGE,{"disambiguationData":[TD([[subQ4,-1.0]])],"derivedFrom":subQ3}),1.0]])]});}
            var Q64;
            {var subQ3=sQuery(id+"F0.wireOp",EDGE,"E8.left");var subQ5=sQuery(id+"F0.wireOp",EDGE,"E19.top");var subQ7=makeQuery(id+"F0.imprint","INTERSECT",VERTEX,{"derivedFrom":[subQ3,subQ5]});Q64=makeQuery(id+"F0.imprint","IMPRINT",FACE,{"disambiguationData":[TD([[makeQuery(id+"F0.imprint","IMPRINT",EDGE,{"disambiguationData":[TD([[subQ7,-1.0]])],"derivedFrom":subQ3}),-1.0]])]});}
            var Q65;
            {var subQ3=sQuery(id+"F0.wireOp",EDGE,"E7.left");var subQ5=sQuery(id+"F0.wireOp",EDGE,"E19.bottom");var subQ7=makeQuery(id+"F0.imprint","INTERSECT",VERTEX,{"derivedFrom":[subQ3,subQ5]});Q65=makeQuery(id+"F0.imprint","IMPRINT",FACE,{"disambiguationData":[TD([[makeQuery(id+"F0.imprint","IMPRINT",EDGE,{"disambiguationData":[TD([[subQ7,-1.0]])],"derivedFrom":subQ3}),1.0]])]});}
            var Q66;
            {var subQ3=sQuery(id+"F0.wireOp",EDGE,"E7.right");var subQ5=sQuery(id+"F0.wireOp",EDGE,"E19.top");var subQ7=makeQuery(id+"F0.imprint","INTERSECT",VERTEX,{"derivedFrom":[subQ3,subQ5]});Q66=makeQuery(id+"F0.imprint","IMPRINT",FACE,{"disambiguationData":[TD([[makeQuery(id+"F0.imprint","IMPRINT",EDGE,{"disambiguationData":[TD([[subQ7,-1.0]])],"derivedFrom":subQ3}),1.0]])]});}
            var Q67;
            {var subQ3=sQuery(id+"F0.wireOp",EDGE,"E7.right");var subQ5=sQuery(id+"F0.wireOp",EDGE,"E20.bottom");var subQ7=makeQuery(id+"F0.imprint","INTERSECT",VERTEX,{"derivedFrom":[subQ3,subQ5]});Q67=makeQuery(id+"F0.imprint","IMPRINT",FACE,{"disambiguationData":[TD([[makeQuery(id+"F0.imprint","IMPRINT",EDGE,{"disambiguationData":[TD([[subQ7,-1.0]])],"derivedFrom":subQ3}),1.0]])]});}
            var Q68;
            {var subQ0=sQuery(id+"F0.wireOp",EDGE,"E19.top");var subQ3=sQuery(id+"F0.wireOp",EDGE,"E6.right");var subQ4=makeQuery(id+"F0.imprint","INTERSECT",VERTEX,{"derivedFrom":[subQ3,subQ0]});Q68=makeQuery(id+"F0.imprint","IMPRINT",FACE,{"disambiguationData":[TD([[makeQuery(id+"F0.imprint","IMPRINT",EDGE,{"disambiguationData":[TD([[subQ4,-1.0]])],"derivedFrom":subQ3}),-1.0]])]});}
            var Q69;
            {var subQ1=sQuery(id+"F0.wireOp",EDGE,"E19.top");var subQ5=sQuery(id+"F0.wireOp",EDGE,"E6.right");var subQ7=makeQuery(id+"F0.imprint","INTERSECT",VERTEX,{"derivedFrom":[subQ5,subQ1]});Q69=makeQuery(id+"F0.imprint","IMPRINT",FACE,{"disambiguationData":[TD([[makeQuery(id+"F0.imprint","IMPRINT",EDGE,{"disambiguationData":[TD([[subQ7,-1.0]])],"derivedFrom":subQ5}),1.0]])]});}
            var Q70;
            {var subQ3=sQuery(id+"F0.wireOp",EDGE,"E19.bottom");var subQ5=sQuery(id+"F0.wireOp",EDGE,"E5.right");var subQ7=makeQuery(id+"F0.imprint","INTERSECT",VERTEX,{"derivedFrom":[subQ5,subQ3]});Q70=makeQuery(id+"F0.imprint","IMPRINT",FACE,{"disambiguationData":[TD([[makeQuery(id+"F0.imprint","IMPRINT",EDGE,{"disambiguationData":[TD([[subQ7,-1.0]])],"derivedFrom":subQ5}),1.0]])]});}
            var Q71;
            {var subQ1=sQuery(id+"F0.wireOp",EDGE,"E20.bottom");var subQ5=sQuery(id+"F0.wireOp",EDGE,"E6.right");var subQ6=makeQuery(id+"F0.imprint","INTERSECT",VERTEX,{"derivedFrom":[subQ5,subQ1]});Q71=makeQuery(id+"F0.imprint","IMPRINT",FACE,{"disambiguationData":[TD([[makeQuery(id+"F0.imprint","IMPRINT",EDGE,{"disambiguationData":[TD([[subQ6,-1.0]])],"derivedFrom":subQ5}),1.0]])]});}
            var Q72;
            {var subQ1=sQuery(id+"F0.wireOp",EDGE,"E20.top");var subQ5=sQuery(id+"F0.wireOp",EDGE,"E6.right");var subQ6=makeQuery(id+"F0.imprint","INTERSECT",VERTEX,{"derivedFrom":[subQ5,subQ1]});Q72=makeQuery(id+"F0.imprint","IMPRINT",FACE,{"disambiguationData":[TD([[makeQuery(id+"F0.imprint","IMPRINT",EDGE,{"disambiguationData":[TD([[subQ6,-1.0]])],"derivedFrom":subQ5}),1.0]])]});}
            var Q73;
            {var subQ3=sQuery(id+"F0.wireOp",EDGE,"E20.bottom");var subQ5=sQuery(id+"F0.wireOp",EDGE,"E5.right");var subQ7=makeQuery(id+"F0.imprint","INTERSECT",VERTEX,{"derivedFrom":[subQ5,subQ3]});Q73=makeQuery(id+"F0.imprint","IMPRINT",FACE,{"disambiguationData":[TD([[makeQuery(id+"F0.imprint","IMPRINT",EDGE,{"disambiguationData":[TD([[subQ7,-1.0]])],"derivedFrom":subQ5}),1.0]])]});}
            var Q74;
            {var subQ0=sQuery(id+"F0.wireOp",EDGE,"E21.bottom");var subQ3=sQuery(id+"F0.wireOp",EDGE,"E6.right");var subQ4=makeQuery(id+"F0.imprint","INTERSECT",VERTEX,{"derivedFrom":[subQ3,subQ0]});Q74=makeQuery(id+"F0.imprint","IMPRINT",FACE,{"disambiguationData":[TD([[makeQuery(id+"F0.imprint","IMPRINT",EDGE,{"disambiguationData":[TD([[subQ4,-1.0]])],"derivedFrom":subQ3}),-1.0]])]});}
            var Q75;
            {var subQ3=sQuery(id+"F0.wireOp",EDGE,"E7.left");var subQ5=sQuery(id+"F0.wireOp",EDGE,"E21.bottom");var subQ7=makeQuery(id+"F0.imprint","INTERSECT",VERTEX,{"derivedFrom":[subQ3,subQ5]});Q75=makeQuery(id+"F0.imprint","IMPRINT",FACE,{"disambiguationData":[TD([[makeQuery(id+"F0.imprint","IMPRINT",EDGE,{"disambiguationData":[TD([[subQ7,-1.0]])],"derivedFrom":subQ3}),1.0]])]});}
            var Q76;
            {var subQ0=sQuery(id+"F0.wireOp",EDGE,"E21.bottom");var subQ3=sQuery(id+"F0.wireOp",EDGE,"E7.right");var subQ4=makeQuery(id+"F0.imprint","INTERSECT",VERTEX,{"derivedFrom":[subQ3,subQ0]});Q76=makeQuery(id+"F0.imprint","IMPRINT",FACE,{"disambiguationData":[TD([[makeQuery(id+"F0.imprint","IMPRINT",EDGE,{"disambiguationData":[TD([[subQ4,-1.0]])],"derivedFrom":subQ3}),1.0]])]});}
            var Q77;
            {var subQ0=sQuery(id+"F0.wireOp",EDGE,"E22.bottom");var subQ3=sQuery(id+"F0.wireOp",EDGE,"E6.right");var subQ4=makeQuery(id+"F0.imprint","INTERSECT",VERTEX,{"derivedFrom":[subQ3,subQ0]});Q77=makeQuery(id+"F0.imprint","IMPRINT",FACE,{"disambiguationData":[TD([[makeQuery(id+"F0.imprint","IMPRINT",EDGE,{"disambiguationData":[TD([[subQ4,-1.0]])],"derivedFrom":subQ3}),-1.0]])]});}
            var Q78;
            {var subQ1=sQuery(id+"F0.wireOp",EDGE,"E22.bottom");var subQ5=sQuery(id+"F0.wireOp",EDGE,"E6.right");var subQ6=makeQuery(id+"F0.imprint","INTERSECT",VERTEX,{"derivedFrom":[subQ5,subQ1]});Q78=makeQuery(id+"F0.imprint","IMPRINT",FACE,{"disambiguationData":[TD([[makeQuery(id+"F0.imprint","IMPRINT",EDGE,{"disambiguationData":[TD([[subQ6,-1.0]])],"derivedFrom":subQ5}),1.0]])]});}
            var Q79;
            {var subQ3=sQuery(id+"F0.wireOp",EDGE,"E21.bottom");var subQ5=sQuery(id+"F0.wireOp",EDGE,"E5.right");var subQ7=makeQuery(id+"F0.imprint","INTERSECT",VERTEX,{"derivedFrom":[subQ5,subQ3]});Q79=makeQuery(id+"F0.imprint","IMPRINT",FACE,{"disambiguationData":[TD([[makeQuery(id+"F0.imprint","IMPRINT",EDGE,{"disambiguationData":[TD([[subQ7,-1.0]])],"derivedFrom":subQ5}),1.0]])]});}
            var Q80;
            {var subQ3=sQuery(id+"F0.wireOp",EDGE,"E5.left");var subQ5=sQuery(id+"F0.wireOp",EDGE,"E21.top");var subQ7=makeQuery(id+"F0.imprint","INTERSECT",VERTEX,{"derivedFrom":[subQ3,subQ5]});Q80=makeQuery(id+"F0.imprint","IMPRINT",FACE,{"disambiguationData":[TD([[makeQuery(id+"F0.imprint","IMPRINT",EDGE,{"disambiguationData":[TD([[subQ7,-1.0]])],"derivedFrom":subQ3}),1.0]])]});}
            var Q81;
            {var subQ3=sQuery(id+"F0.wireOp",EDGE,"E21.bottom");var subQ5=sQuery(id+"F0.wireOp",EDGE,"E5.left");var subQ7=makeQuery(id+"F0.imprint","INTERSECT",VERTEX,{"derivedFrom":[subQ5,subQ3]});Q81=makeQuery(id+"F0.imprint","IMPRINT",FACE,{"disambiguationData":[TD([[makeQuery(id+"F0.imprint","IMPRINT",EDGE,{"disambiguationData":[TD([[subQ7,-1.0]])],"derivedFrom":subQ5}),-1.0]])]});}
            var Q82;
            {var subQ1=sQuery(id+"F0.wireOp",EDGE,"E22.top");var subQ5=sQuery(id+"F0.wireOp",EDGE,"E6.right");var subQ6=makeQuery(id+"F0.imprint","INTERSECT",VERTEX,{"derivedFrom":[subQ5,subQ1]});Q82=makeQuery(id+"F0.imprint","IMPRINT",FACE,{"disambiguationData":[TD([[makeQuery(id+"F0.imprint","IMPRINT",EDGE,{"disambiguationData":[TD([[subQ6,-1.0]])],"derivedFrom":subQ5}),1.0]])]});}
            var Q83;
            {var subQ3=sQuery(id+"F0.wireOp",EDGE,"E22.bottom");var subQ5=sQuery(id+"F0.wireOp",EDGE,"E5.right");var subQ7=makeQuery(id+"F0.imprint","INTERSECT",VERTEX,{"derivedFrom":[subQ5,subQ3]});Q83=makeQuery(id+"F0.imprint","IMPRINT",FACE,{"disambiguationData":[TD([[makeQuery(id+"F0.imprint","IMPRINT",EDGE,{"disambiguationData":[TD([[subQ7,-1.0]])],"derivedFrom":subQ5}),1.0]])]});}
            var Q84;
            {var subQ3=sQuery(id+"F0.wireOp",EDGE,"E5.left");var subQ5=sQuery(id+"F0.wireOp",EDGE,"E22.bottom");var subQ7=makeQuery(id+"F0.imprint","INTERSECT",VERTEX,{"derivedFrom":[subQ3,subQ5]});Q84=makeQuery(id+"F0.imprint","IMPRINT",FACE,{"disambiguationData":[TD([[makeQuery(id+"F0.imprint","IMPRINT",EDGE,{"disambiguationData":[TD([[subQ7,-1.0]])],"derivedFrom":subQ3}),1.0]])]});}
            var Q85;
            {var subQ3=sQuery(id+"F0.wireOp",EDGE,"E22.bottom");var subQ5=sQuery(id+"F0.wireOp",EDGE,"E5.left");var subQ7=makeQuery(id+"F0.imprint","INTERSECT",VERTEX,{"derivedFrom":[subQ5,subQ3]});Q85=makeQuery(id+"F0.imprint","IMPRINT",FACE,{"disambiguationData":[TD([[makeQuery(id+"F0.imprint","IMPRINT",EDGE,{"disambiguationData":[TD([[subQ7,-1.0]])],"derivedFrom":subQ5}),-1.0]])]});}
            var Q86;
            {var subQ1=sQuery(id+"F0.wireOp",EDGE,"E21.bottom");var subQ5=sQuery(id+"F0.wireOp",EDGE,"E4.left");var subQ6=makeQuery(id+"F0.imprint","INTERSECT",VERTEX,{"derivedFrom":[subQ5,subQ1]});Q86=makeQuery(id+"F0.imprint","IMPRINT",FACE,{"disambiguationData":[TD([[makeQuery(id+"F0.imprint","IMPRINT",EDGE,{"disambiguationData":[TD([[subQ6,-1.0]])],"derivedFrom":subQ5}),-1.0]])]});}
            var Q87;
            {var subQ3=sQuery(id+"F0.wireOp",EDGE,"E3.left");var subQ5=sQuery(id+"F0.wireOp",EDGE,"E20.top");var subQ7=makeQuery(id+"F0.imprint","INTERSECT",VERTEX,{"derivedFrom":[subQ3,subQ5]});Q87=makeQuery(id+"F0.imprint","IMPRINT",FACE,{"disambiguationData":[TD([[makeQuery(id+"F0.imprint","IMPRINT",EDGE,{"disambiguationData":[TD([[subQ7,-1.0]])],"derivedFrom":subQ3}),1.0]])]});}
            var Q88;
            {var subQ3=sQuery(id+"F0.wireOp",EDGE,"E3.left");var subQ5=sQuery(id+"F0.wireOp",EDGE,"E21.bottom");var subQ7=makeQuery(id+"F0.imprint","INTERSECT",VERTEX,{"derivedFrom":[subQ3,subQ5]});Q88=makeQuery(id+"F0.imprint","IMPRINT",FACE,{"disambiguationData":[TD([[makeQuery(id+"F0.imprint","IMPRINT",EDGE,{"disambiguationData":[TD([[subQ7,-1.0]])],"derivedFrom":subQ3}),1.0]])]});}
            var Q89;
            {var subQ0=sQuery(id+"F0.wireOp",EDGE,"E21.left");Q89=makeQuery(id+"F0.imprint","IMPRINT",FACE,{"disambiguationData":[TD([[makeQuery(id+"F0.imprint","IMPRINT",EDGE,{"derivedFrom":subQ0}),1.0]])]});}
            var Q90;
            {var subQ0=sQuery(id+"F0.wireOp",EDGE,"E49");Q90=makeQuery(id+"F0.imprint","IMPRINT",FACE,{"disambiguationData":[TD([[makeQuery(id+"F0.imprint","IMPRINT",EDGE,{"derivedFrom":subQ0}),1.0]])]});}
            var Q91;
            {var subQ0=sQuery(id+"F0.wireOp",EDGE,"E20.right");Q91=makeQuery(id+"F0.imprint","IMPRINT",FACE,{"disambiguationData":[TD([[makeQuery(id+"F0.imprint","IMPRINT",EDGE,{"derivedFrom":subQ0}),1.0]])]});}
            var Q92;
            {var subQ3=sQuery(id+"F0.wireOp",EDGE,"E0");var subQ5=sQuery(id+"F0.wireOp",EDGE,"E20.bottom");var subQ7=makeQuery(id+"F0.imprint","INTERSECT",VERTEX,{"derivedFrom":[subQ3,subQ5]});Q92=makeQuery(id+"F0.imprint","IMPRINT",FACE,{"disambiguationData":[TD([[makeQuery(id+"F0.imprint","IMPRINT",EDGE,{"disambiguationData":[TD([[subQ7,-1.0]])],"derivedFrom":subQ3}),1.0]])]});}
            var Q93;
            {var subQ3=sQuery(id+"F0.wireOp",EDGE,"E3.left");var subQ5=sQuery(id+"F0.wireOp",EDGE,"E20.bottom");var subQ7=makeQuery(id+"F0.imprint","INTERSECT",VERTEX,{"derivedFrom":[subQ3,subQ5]});Q93=makeQuery(id+"F0.imprint","IMPRINT",FACE,{"disambiguationData":[TD([[makeQuery(id+"F0.imprint","IMPRINT",EDGE,{"disambiguationData":[TD([[subQ7,-1.0]])],"derivedFrom":subQ3}),1.0]])]});}
            var Q94;
            {var subQ1=sQuery(id+"F0.wireOp",EDGE,"E20.top");var subQ5=sQuery(id+"F0.wireOp",EDGE,"E4.left");var subQ6=makeQuery(id+"F0.imprint","INTERSECT",VERTEX,{"derivedFrom":[subQ5,subQ1]});Q94=makeQuery(id+"F0.imprint","IMPRINT",FACE,{"disambiguationData":[TD([[makeQuery(id+"F0.imprint","IMPRINT",EDGE,{"disambiguationData":[TD([[subQ6,-1.0]])],"derivedFrom":subQ5}),-1.0]])]});}
            var Q95;
            {var subQ3=sQuery(id+"F0.wireOp",EDGE,"E3.left");var subQ5=sQuery(id+"F0.wireOp",EDGE,"E19.top");var subQ7=makeQuery(id+"F0.imprint","INTERSECT",VERTEX,{"derivedFrom":[subQ3,subQ5]});Q95=makeQuery(id+"F0.imprint","IMPRINT",FACE,{"disambiguationData":[TD([[makeQuery(id+"F0.imprint","IMPRINT",EDGE,{"disambiguationData":[TD([[subQ7,-1.0]])],"derivedFrom":subQ3}),1.0]])]});}
            var Q96;
            {var subQ3=sQuery(id+"F0.wireOp",EDGE,"E0");var subQ5=sQuery(id+"F0.wireOp",EDGE,"E19.top");var subQ7=makeQuery(id+"F0.imprint","INTERSECT",VERTEX,{"derivedFrom":[subQ3,subQ5]});Q96=makeQuery(id+"F0.imprint","IMPRINT",FACE,{"disambiguationData":[TD([[makeQuery(id+"F0.imprint","IMPRINT",EDGE,{"disambiguationData":[TD([[subQ7,-1.0]])],"derivedFrom":subQ3}),1.0]])]});}
            var Q97;
            {var subQ3=sQuery(id+"F0.wireOp",EDGE,"E0");var subQ5=sQuery(id+"F0.wireOp",EDGE,"E19.bottom");var subQ7=makeQuery(id+"F0.imprint","INTERSECT",VERTEX,{"derivedFrom":[subQ3,subQ5]});Q97=makeQuery(id+"F0.imprint","IMPRINT",FACE,{"disambiguationData":[TD([[makeQuery(id+"F0.imprint","IMPRINT",EDGE,{"disambiguationData":[TD([[subQ7,-1.0]])],"derivedFrom":subQ3}),1.0]])]});}
            var Q98;
            {var subQ0=sQuery(id+"F0.wireOp",EDGE,"E19.left");Q98=makeQuery(id+"F0.imprint","IMPRINT",FACE,{"disambiguationData":[TD([[makeQuery(id+"F0.imprint","IMPRINT",EDGE,{"derivedFrom":subQ0}),1.0]])]});}
            var Q99;
            {var subQ3=sQuery(id+"F0.wireOp",EDGE,"E3.left");var subQ5=sQuery(id+"F0.wireOp",EDGE,"E19.bottom");var subQ7=makeQuery(id+"F0.imprint","INTERSECT",VERTEX,{"derivedFrom":[subQ3,subQ5]});Q99=makeQuery(id+"F0.imprint","IMPRINT",FACE,{"disambiguationData":[TD([[makeQuery(id+"F0.imprint","IMPRINT",EDGE,{"disambiguationData":[TD([[subQ7,-1.0]])],"derivedFrom":subQ3}),1.0]])]});}
            var Q100;
            {var subQ1=sQuery(id+"F0.wireOp",EDGE,"E19.top");var subQ5=sQuery(id+"F0.wireOp",EDGE,"E4.left");var subQ6=makeQuery(id+"F0.imprint","INTERSECT",VERTEX,{"derivedFrom":[subQ5,subQ1]});Q100=makeQuery(id+"F0.imprint","IMPRINT",FACE,{"disambiguationData":[TD([[makeQuery(id+"F0.imprint","IMPRINT",EDGE,{"disambiguationData":[TD([[subQ6,-1.0]])],"derivedFrom":subQ5}),-1.0]])]});}
            var Q101;
            {var subQ3=sQuery(id+"F0.wireOp",EDGE,"E19.bottom");var subQ5=sQuery(id+"F0.wireOp",EDGE,"E5.left");var subQ7=makeQuery(id+"F0.imprint","INTERSECT",VERTEX,{"derivedFrom":[subQ5,subQ3]});Q101=makeQuery(id+"F0.imprint","IMPRINT",FACE,{"disambiguationData":[TD([[makeQuery(id+"F0.imprint","IMPRINT",EDGE,{"disambiguationData":[TD([[subQ7,-1.0]])],"derivedFrom":subQ5}),-1.0]])]});}
            var Q102;
            {var subQ3=sQuery(id+"F0.wireOp",EDGE,"E5.left");var subQ5=sQuery(id+"F0.wireOp",EDGE,"E20.bottom");var subQ7=makeQuery(id+"F0.imprint","INTERSECT",VERTEX,{"derivedFrom":[subQ3,subQ5]});Q102=makeQuery(id+"F0.imprint","IMPRINT",FACE,{"disambiguationData":[TD([[makeQuery(id+"F0.imprint","IMPRINT",EDGE,{"disambiguationData":[TD([[subQ7,-1.0]])],"derivedFrom":subQ3}),1.0]])]});}
            var Q103;
            {var subQ3=sQuery(id+"F0.wireOp",EDGE,"E0");var subQ5=sQuery(id+"F0.wireOp",EDGE,"E21.top");var subQ7=makeQuery(id+"F0.imprint","INTERSECT",VERTEX,{"derivedFrom":[subQ3,subQ5]});Q103=makeQuery(id+"F0.imprint","IMPRINT",FACE,{"disambiguationData":[TD([[makeQuery(id+"F0.imprint","IMPRINT",EDGE,{"disambiguationData":[TD([[subQ7,-1.0]])],"derivedFrom":subQ3}),1.0]])]});}
            var Q104;
            {var subQ3=sQuery(id+"F0.wireOp",EDGE,"E0");var subQ5=sQuery(id+"F0.wireOp",EDGE,"E22.bottom");var subQ7=makeQuery(id+"F0.imprint","INTERSECT",VERTEX,{"derivedFrom":[subQ3,subQ5]});Q104=makeQuery(id+"F0.imprint","IMPRINT",FACE,{"disambiguationData":[TD([[makeQuery(id+"F0.imprint","IMPRINT",EDGE,{"disambiguationData":[TD([[subQ7,-1.0]])],"derivedFrom":subQ3}),1.0]])]});}
            var Q105;
            {var subQ0=sQuery(id+"F0.wireOp",EDGE,"E22.top");var subQ3=sQuery(id+"F0.wireOp",EDGE,"E0");var subQ4=makeQuery(id+"F0.imprint","INTERSECT",VERTEX,{"derivedFrom":[subQ3,subQ0]});Q105=makeQuery(id+"F0.imprint","IMPRINT",FACE,{"disambiguationData":[TD([[makeQuery(id+"F0.imprint","IMPRINT",EDGE,{"disambiguationData":[TD([[subQ4,-1.0]])],"derivedFrom":subQ3}),1.0]])]});}
            var Q106;
            {var subQ3=sQuery(id+"F0.wireOp",EDGE,"E0");var subQ5=sQuery(id+"F0.wireOp",EDGE,"E23.bottom");var subQ7=makeQuery(id+"F0.imprint","INTERSECT",VERTEX,{"derivedFrom":[subQ3,subQ5]});Q106=makeQuery(id+"F0.imprint","IMPRINT",FACE,{"disambiguationData":[TD([[makeQuery(id+"F0.imprint","IMPRINT",EDGE,{"disambiguationData":[TD([[subQ7,-1.0]])],"derivedFrom":subQ3}),1.0]])]});}
            var Q107;
            {var subQ3=sQuery(id+"F0.wireOp",EDGE,"E3.left");var subQ5=sQuery(id+"F0.wireOp",EDGE,"E22.bottom");var subQ7=makeQuery(id+"F0.imprint","INTERSECT",VERTEX,{"derivedFrom":[subQ3,subQ5]});Q107=makeQuery(id+"F0.imprint","IMPRINT",FACE,{"disambiguationData":[TD([[makeQuery(id+"F0.imprint","IMPRINT",EDGE,{"disambiguationData":[TD([[subQ7,-1.0]])],"derivedFrom":subQ3}),1.0]])]});}
            var Q108;
            {var subQ3=sQuery(id+"F0.wireOp",EDGE,"E3.left");var subQ5=sQuery(id+"F0.wireOp",EDGE,"E23.bottom");var subQ7=makeQuery(id+"F0.imprint","INTERSECT",VERTEX,{"derivedFrom":[subQ3,subQ5]});Q108=makeQuery(id+"F0.imprint","IMPRINT",FACE,{"disambiguationData":[TD([[makeQuery(id+"F0.imprint","IMPRINT",EDGE,{"disambiguationData":[TD([[subQ7,-1.0]])],"derivedFrom":subQ3}),1.0]])]});}
            var Q109;
            {var subQ0=sQuery(id+"F0.wireOp",EDGE,"E23.top");var subQ3=sQuery(id+"F0.wireOp",EDGE,"E4.left");var subQ4=makeQuery(id+"F0.imprint","INTERSECT",VERTEX,{"derivedFrom":[subQ3,subQ0]});Q109=makeQuery(id+"F0.imprint","IMPRINT",FACE,{"disambiguationData":[TD([[makeQuery(id+"F0.imprint","IMPRINT",EDGE,{"disambiguationData":[TD([[subQ4,-1.0]])],"derivedFrom":subQ3}),-1.0]])]});}
            var Q110;
            {var subQ1=sQuery(id+"F0.wireOp",EDGE,"E52");Q110=makeQuery(id+"F0.imprint","IMPRINT",FACE,{"disambiguationData":[TD([[makeQuery(id+"F0.imprint","IMPRINT",EDGE,{"derivedFrom":subQ1}),-1.0]])]});}
            var Q111;
            {var subQ5=sQuery(id+"F0.wireOp",EDGE,"E1");Q111=makeQuery(id+"F0.imprint","IMPRINT",FACE,{"disambiguationData":[TD([[makeQuery(id+"F0.imprint","IMPRINT",EDGE,{"derivedFrom":subQ5}),1.0]])]});}
            var Q112;
            {var subQ0=sQuery(id+"F0.wireOp",EDGE,"E31");Q112=makeQuery(id+"F0.imprint","IMPRINT",FACE,{"disambiguationData":[TD([[makeQuery(id+"F0.imprint","IMPRINT",EDGE,{"derivedFrom":subQ0}),1.0]])]});}
            var Q113;
            {var subQ3=sQuery(id+"F0.wireOp",EDGE,"E32");Q113=makeQuery(id+"F0.imprint","IMPRINT",FACE,{"disambiguationData":[TD([[makeQuery(id+"F0.imprint","IMPRINT",EDGE,{"derivedFrom":subQ3}),1.0]])]});}
            var Q114;
            {var subQ3=sQuery(id+"F0.wireOp",EDGE,"E3.left");var subQ5=sQuery(id+"F0.wireOp",EDGE,"E26.bottom");var subQ7=makeQuery(id+"F0.imprint","INTERSECT",VERTEX,{"derivedFrom":[subQ3,subQ5]});Q114=makeQuery(id+"F0.imprint","IMPRINT",FACE,{"disambiguationData":[TD([[makeQuery(id+"F0.imprint","IMPRINT",EDGE,{"disambiguationData":[TD([[subQ7,-1.0]])],"derivedFrom":subQ3}),1.0]])]});}
            var Q115;
            {var subQ1=sQuery(id+"F0.wireOp",EDGE,"E26.top");var subQ5=sQuery(id+"F0.wireOp",EDGE,"E4.left");var subQ6=makeQuery(id+"F0.imprint","INTERSECT",VERTEX,{"derivedFrom":[subQ5,subQ1]});Q115=makeQuery(id+"F0.imprint","IMPRINT",FACE,{"disambiguationData":[TD([[makeQuery(id+"F0.imprint","IMPRINT",EDGE,{"disambiguationData":[TD([[subQ6,-1.0]])],"derivedFrom":subQ5}),-1.0]])]});}
            var Q116;
            {var subQ3=sQuery(id+"F0.wireOp",EDGE,"E26.bottom");var subQ5=sQuery(id+"F0.wireOp",EDGE,"E5.left");var subQ7=makeQuery(id+"F0.imprint","INTERSECT",VERTEX,{"derivedFrom":[subQ5,subQ3]});Q116=makeQuery(id+"F0.imprint","IMPRINT",FACE,{"disambiguationData":[TD([[makeQuery(id+"F0.imprint","IMPRINT",EDGE,{"disambiguationData":[TD([[subQ7,-1.0]])],"derivedFrom":subQ5}),-1.0]])]});}
            var Q117;
            {var subQ0=sQuery(id+"F0.wireOp",EDGE,"E25.top");var subQ3=sQuery(id+"F0.wireOp",EDGE,"E3.left");var subQ4=makeQuery(id+"F0.imprint","INTERSECT",VERTEX,{"derivedFrom":[subQ3,subQ0]});Q117=makeQuery(id+"F0.imprint","IMPRINT",FACE,{"disambiguationData":[TD([[makeQuery(id+"F0.imprint","IMPRINT",EDGE,{"disambiguationData":[TD([[subQ4,-1.0]])],"derivedFrom":subQ3}),1.0]])]});}
            var Q118;
            {var subQ0=sQuery(id+"F0.wireOp",EDGE,"E26.bottom");var subQ3=sQuery(id+"F0.wireOp",EDGE,"E4.left");var subQ4=makeQuery(id+"F0.imprint","INTERSECT",VERTEX,{"derivedFrom":[subQ3,subQ0]});Q118=makeQuery(id+"F0.imprint","IMPRINT",FACE,{"disambiguationData":[TD([[makeQuery(id+"F0.imprint","IMPRINT",EDGE,{"disambiguationData":[TD([[subQ4,-1.0]])],"derivedFrom":subQ3}),-1.0]])]});}
            var Q119;
            {var subQ3=sQuery(id+"F0.wireOp",EDGE,"E25.top");var subQ5=sQuery(id+"F0.wireOp",EDGE,"E5.left");var subQ7=makeQuery(id+"F0.imprint","INTERSECT",VERTEX,{"derivedFrom":[subQ5,subQ3]});Q119=makeQuery(id+"F0.imprint","IMPRINT",FACE,{"disambiguationData":[TD([[makeQuery(id+"F0.imprint","IMPRINT",EDGE,{"disambiguationData":[TD([[subQ7,-1.0]])],"derivedFrom":subQ5}),-1.0]])]});}
            var Q120;
            {var subQ3=sQuery(id+"F0.wireOp",EDGE,"E3.left");var subQ5=sQuery(id+"F0.wireOp",EDGE,"E25.bottom");var subQ7=makeQuery(id+"F0.imprint","INTERSECT",VERTEX,{"derivedFrom":[subQ3,subQ5]});Q120=makeQuery(id+"F0.imprint","IMPRINT",FACE,{"disambiguationData":[TD([[makeQuery(id+"F0.imprint","IMPRINT",EDGE,{"disambiguationData":[TD([[subQ7,-1.0]])],"derivedFrom":subQ3}),1.0]])]});}
            var Q121;
            {var subQ1=sQuery(id+"F0.wireOp",EDGE,"E25.top");var subQ5=sQuery(id+"F0.wireOp",EDGE,"E4.left");var subQ6=makeQuery(id+"F0.imprint","INTERSECT",VERTEX,{"derivedFrom":[subQ5,subQ1]});Q121=makeQuery(id+"F0.imprint","IMPRINT",FACE,{"disambiguationData":[TD([[makeQuery(id+"F0.imprint","IMPRINT",EDGE,{"disambiguationData":[TD([[subQ6,-1.0]])],"derivedFrom":subQ5}),-1.0]])]});}
            var Q122;
            {var subQ3=sQuery(id+"F0.wireOp",EDGE,"E25.bottom");var subQ5=sQuery(id+"F0.wireOp",EDGE,"E5.left");var subQ7=makeQuery(id+"F0.imprint","INTERSECT",VERTEX,{"derivedFrom":[subQ5,subQ3]});Q122=makeQuery(id+"F0.imprint","IMPRINT",FACE,{"disambiguationData":[TD([[makeQuery(id+"F0.imprint","IMPRINT",EDGE,{"disambiguationData":[TD([[subQ7,-1.0]])],"derivedFrom":subQ5}),-1.0]])]});}
            var Q123;
            {var subQ0=sQuery(id+"F0.wireOp",EDGE,"E54");Q123=makeQuery(id+"F0.imprint","IMPRINT",FACE,{"disambiguationData":[TD([[makeQuery(id+"F0.imprint","IMPRINT",EDGE,{"derivedFrom":subQ0}),1.0]])]});}
            var Q124;
            {var subQ0=sQuery(id+"F0.wireOp",EDGE,"E26.right");Q124=makeQuery(id+"F0.imprint","IMPRINT",FACE,{"disambiguationData":[TD([[makeQuery(id+"F0.imprint","IMPRINT",EDGE,{"derivedFrom":subQ0}),1.0]])]});}
            var Q125;
            {var subQ0=sQuery(id+"F0.wireOp",EDGE,"E55");Q125=makeQuery(id+"F0.imprint","IMPRINT",FACE,{"disambiguationData":[TD([[makeQuery(id+"F0.imprint","IMPRINT",EDGE,{"derivedFrom":subQ0}),-1.0]])]});}
            var Q126;
            {var subQ0=sQuery(id+"F0.wireOp",EDGE,"E25.left");Q126=makeQuery(id+"F0.imprint","IMPRINT",FACE,{"disambiguationData":[TD([[makeQuery(id+"F0.imprint","IMPRINT",EDGE,{"derivedFrom":subQ0}),1.0]])]});}
            var Q127;
            {var subQ0=sQuery(id+"F0.wireOp",EDGE,"E56");Q127=makeQuery(id+"F0.imprint","IMPRINT",FACE,{"disambiguationData":[TD([[makeQuery(id+"F0.imprint","IMPRINT",EDGE,{"derivedFrom":subQ0}),-1.0]])]});}
            var Q128;
            {var subQ0=sQuery(id+"F0.wireOp",EDGE,"E24.right");Q128=makeQuery(id+"F0.imprint","IMPRINT",FACE,{"disambiguationData":[TD([[makeQuery(id+"F0.imprint","IMPRINT",EDGE,{"derivedFrom":subQ0}),1.0]])]});}
            var Q129;
            {var subQ3=sQuery(id+"F0.wireOp",EDGE,"E0");var subQ5=sQuery(id+"F0.wireOp",EDGE,"E24.bottom");var subQ7=makeQuery(id+"F0.imprint","INTERSECT",VERTEX,{"derivedFrom":[subQ3,subQ5]});Q129=makeQuery(id+"F0.imprint","IMPRINT",FACE,{"disambiguationData":[TD([[makeQuery(id+"F0.imprint","IMPRINT",EDGE,{"disambiguationData":[TD([[subQ7,-1.0]])],"derivedFrom":subQ3}),1.0]])]});}
            var Q130;
            {var subQ3=sQuery(id+"F0.wireOp",EDGE,"E3.left");var subQ5=sQuery(id+"F0.wireOp",EDGE,"E24.bottom");var subQ7=makeQuery(id+"F0.imprint","INTERSECT",VERTEX,{"derivedFrom":[subQ3,subQ5]});Q130=makeQuery(id+"F0.imprint","IMPRINT",FACE,{"disambiguationData":[TD([[makeQuery(id+"F0.imprint","IMPRINT",EDGE,{"disambiguationData":[TD([[subQ7,-1.0]])],"derivedFrom":subQ3}),1.0]])]});}
            var Q131;
            {var subQ1=sQuery(id+"F0.wireOp",EDGE,"E24.top");var subQ5=sQuery(id+"F0.wireOp",EDGE,"E4.left");var subQ6=makeQuery(id+"F0.imprint","INTERSECT",VERTEX,{"derivedFrom":[subQ5,subQ1]});Q131=makeQuery(id+"F0.imprint","IMPRINT",FACE,{"disambiguationData":[TD([[makeQuery(id+"F0.imprint","IMPRINT",EDGE,{"disambiguationData":[TD([[subQ6,-1.0]])],"derivedFrom":subQ5}),-1.0]])]});}
            var Q132;
            {var subQ3=sQuery(id+"F0.wireOp",EDGE,"E24.bottom");var subQ5=sQuery(id+"F0.wireOp",EDGE,"E5.left");var subQ7=makeQuery(id+"F0.imprint","INTERSECT",VERTEX,{"derivedFrom":[subQ5,subQ3]});Q132=makeQuery(id+"F0.imprint","IMPRINT",FACE,{"disambiguationData":[TD([[makeQuery(id+"F0.imprint","IMPRINT",EDGE,{"disambiguationData":[TD([[subQ7,-1.0]])],"derivedFrom":subQ5}),-1.0]])]});}
            var Q133;
            {var subQ3=sQuery(id+"F0.wireOp",EDGE,"E5.left");var subQ5=sQuery(id+"F0.wireOp",EDGE,"E24.bottom");var subQ7=makeQuery(id+"F0.imprint","INTERSECT",VERTEX,{"derivedFrom":[subQ3,subQ5]});Q133=makeQuery(id+"F0.imprint","IMPRINT",FACE,{"disambiguationData":[TD([[makeQuery(id+"F0.imprint","IMPRINT",EDGE,{"disambiguationData":[TD([[subQ7,-1.0]])],"derivedFrom":subQ3}),1.0]])]});}
            var Q134;
            {var subQ3=sQuery(id+"F0.wireOp",EDGE,"E24.bottom");var subQ5=sQuery(id+"F0.wireOp",EDGE,"E5.right");var subQ7=makeQuery(id+"F0.imprint","INTERSECT",VERTEX,{"derivedFrom":[subQ5,subQ3]});Q134=makeQuery(id+"F0.imprint","IMPRINT",FACE,{"disambiguationData":[TD([[makeQuery(id+"F0.imprint","IMPRINT",EDGE,{"disambiguationData":[TD([[subQ7,-1.0]])],"derivedFrom":subQ5}),1.0]])]});}
            var Q135;
            {var subQ3=sQuery(id+"F0.wireOp",EDGE,"E24.top");var subQ5=sQuery(id+"F0.wireOp",EDGE,"E5.right");var subQ7=makeQuery(id+"F0.imprint","INTERSECT",VERTEX,{"derivedFrom":[subQ5,subQ3]});Q135=makeQuery(id+"F0.imprint","IMPRINT",FACE,{"disambiguationData":[TD([[makeQuery(id+"F0.imprint","IMPRINT",EDGE,{"disambiguationData":[TD([[subQ7,-1.0]])],"derivedFrom":subQ5}),1.0]])]});}
            var Q136;
            {var subQ3=sQuery(id+"F0.wireOp",EDGE,"E25.bottom");var subQ5=sQuery(id+"F0.wireOp",EDGE,"E5.right");var subQ7=makeQuery(id+"F0.imprint","INTERSECT",VERTEX,{"derivedFrom":[subQ5,subQ3]});Q136=makeQuery(id+"F0.imprint","IMPRINT",FACE,{"disambiguationData":[TD([[makeQuery(id+"F0.imprint","IMPRINT",EDGE,{"disambiguationData":[TD([[subQ7,-1.0]])],"derivedFrom":subQ5}),1.0]])]});}
            var Q137;
            {var subQ3=sQuery(id+"F0.wireOp",EDGE,"E25.top");var subQ5=sQuery(id+"F0.wireOp",EDGE,"E5.right");var subQ7=makeQuery(id+"F0.imprint","INTERSECT",VERTEX,{"derivedFrom":[subQ5,subQ3]});Q137=makeQuery(id+"F0.imprint","IMPRINT",FACE,{"disambiguationData":[TD([[makeQuery(id+"F0.imprint","IMPRINT",EDGE,{"disambiguationData":[TD([[subQ7,-1.0]])],"derivedFrom":subQ5}),1.0]])]});}
            var Q138;
            {var subQ3=sQuery(id+"F0.wireOp",EDGE,"E26.bottom");var subQ5=sQuery(id+"F0.wireOp",EDGE,"E5.right");var subQ7=makeQuery(id+"F0.imprint","INTERSECT",VERTEX,{"derivedFrom":[subQ5,subQ3]});Q138=makeQuery(id+"F0.imprint","IMPRINT",FACE,{"disambiguationData":[TD([[makeQuery(id+"F0.imprint","IMPRINT",EDGE,{"disambiguationData":[TD([[subQ7,-1.0]])],"derivedFrom":subQ5}),1.0]])]});}
            var Q139;
            {var subQ3=sQuery(id+"F0.wireOp",EDGE,"E26.top");var subQ5=sQuery(id+"F0.wireOp",EDGE,"E5.right");var subQ7=makeQuery(id+"F0.imprint","INTERSECT",VERTEX,{"derivedFrom":[subQ5,subQ3]});Q139=makeQuery(id+"F0.imprint","IMPRINT",FACE,{"disambiguationData":[TD([[makeQuery(id+"F0.imprint","IMPRINT",EDGE,{"disambiguationData":[TD([[subQ7,-1.0]])],"derivedFrom":subQ5}),1.0]])]});}
            var Q140;
            {var subQ0=sQuery(id+"F0.wireOp",EDGE,"E59");Q140=makeQuery(id+"F0.imprint","IMPRINT",FACE,{"disambiguationData":[TD([[makeQuery(id+"F0.imprint","IMPRINT",EDGE,{"derivedFrom":subQ0}),1.0]])]});}
            var Q141;
            {var subQ0=sQuery(id+"F0.wireOp",EDGE,"E75");Q141=makeQuery(id+"F0.imprint","IMPRINT",FACE,{"disambiguationData":[TD([[makeQuery(id+"F0.imprint","IMPRINT",EDGE,{"derivedFrom":subQ0}),1.0]])]});}
            var Q142;
            {var subQ0=sQuery(id+"F0.wireOp",EDGE,"E58");Q142=makeQuery(id+"F0.imprint","IMPRINT",FACE,{"disambiguationData":[TD([[makeQuery(id+"F0.imprint","IMPRINT",EDGE,{"derivedFrom":subQ0}),1.0]])]});}
            var Q143;
            {var subQ0=sQuery(id+"F0.wireOp",EDGE,"E60");Q143=makeQuery(id+"F0.imprint","IMPRINT",FACE,{"disambiguationData":[TD([[makeQuery(id+"F0.imprint","IMPRINT",EDGE,{"derivedFrom":subQ0}),1.0]])]});}
            var Q144;
            {var subQ0=sQuery(id+"F0.wireOp",EDGE,"E27.bottom");var subQ3=sQuery(id+"F0.wireOp",EDGE,"E6.right");var subQ4=makeQuery(id+"F0.imprint","INTERSECT",VERTEX,{"derivedFrom":[subQ3,subQ0]});Q144=makeQuery(id+"F0.imprint","IMPRINT",FACE,{"disambiguationData":[TD([[makeQuery(id+"F0.imprint","IMPRINT",EDGE,{"disambiguationData":[TD([[subQ4,-1.0]])],"derivedFrom":subQ3}),-1.0]])]});}
            var Q145;
            {var subQ0=sQuery(id+"F0.wireOp",EDGE,"E26.top");var subQ3=sQuery(id+"F0.wireOp",EDGE,"E6.right");var subQ4=makeQuery(id+"F0.imprint","INTERSECT",VERTEX,{"derivedFrom":[subQ3,subQ0]});Q145=makeQuery(id+"F0.imprint","IMPRINT",FACE,{"disambiguationData":[TD([[makeQuery(id+"F0.imprint","IMPRINT",EDGE,{"disambiguationData":[TD([[subQ4,-1.0]])],"derivedFrom":subQ3}),-1.0]])]});}
            var Q146;
            {var subQ3=sQuery(id+"F0.wireOp",EDGE,"E7.left");var subQ5=sQuery(id+"F0.wireOp",EDGE,"E26.bottom");var subQ7=makeQuery(id+"F0.imprint","INTERSECT",VERTEX,{"derivedFrom":[subQ3,subQ5]});Q146=makeQuery(id+"F0.imprint","IMPRINT",FACE,{"disambiguationData":[TD([[makeQuery(id+"F0.imprint","IMPRINT",EDGE,{"disambiguationData":[TD([[subQ7,-1.0]])],"derivedFrom":subQ3}),1.0]])]});}
            var Q147;
            {var subQ0=sQuery(id+"F0.wireOp",EDGE,"E26.bottom");var subQ3=sQuery(id+"F0.wireOp",EDGE,"E6.right");var subQ4=makeQuery(id+"F0.imprint","INTERSECT",VERTEX,{"derivedFrom":[subQ3,subQ0]});Q147=makeQuery(id+"F0.imprint","IMPRINT",FACE,{"disambiguationData":[TD([[makeQuery(id+"F0.imprint","IMPRINT",EDGE,{"disambiguationData":[TD([[subQ4,-1.0]])],"derivedFrom":subQ3}),-1.0]])]});}
            var Q148;
            {var subQ3=sQuery(id+"F0.wireOp",EDGE,"E7.left");var subQ5=sQuery(id+"F0.wireOp",EDGE,"E25.top");var subQ7=makeQuery(id+"F0.imprint","INTERSECT",VERTEX,{"derivedFrom":[subQ3,subQ5]});Q148=makeQuery(id+"F0.imprint","IMPRINT",FACE,{"disambiguationData":[TD([[makeQuery(id+"F0.imprint","IMPRINT",EDGE,{"disambiguationData":[TD([[subQ7,-1.0]])],"derivedFrom":subQ3}),1.0]])]});}
            var Q149;
            {var subQ3=sQuery(id+"F0.wireOp",EDGE,"E7.right");var subQ5=sQuery(id+"F0.wireOp",EDGE,"E25.top");var subQ7=makeQuery(id+"F0.imprint","INTERSECT",VERTEX,{"derivedFrom":[subQ3,subQ5]});Q149=makeQuery(id+"F0.imprint","IMPRINT",FACE,{"disambiguationData":[TD([[makeQuery(id+"F0.imprint","IMPRINT",EDGE,{"disambiguationData":[TD([[subQ7,-1.0]])],"derivedFrom":subQ3}),1.0]])]});}
            var Q150;
            {var subQ0=sQuery(id+"F0.wireOp",EDGE,"E25.top");var subQ3=sQuery(id+"F0.wireOp",EDGE,"E6.right");var subQ4=makeQuery(id+"F0.imprint","INTERSECT",VERTEX,{"derivedFrom":[subQ3,subQ0]});Q150=makeQuery(id+"F0.imprint","IMPRINT",FACE,{"disambiguationData":[TD([[makeQuery(id+"F0.imprint","IMPRINT",EDGE,{"disambiguationData":[TD([[subQ4,-1.0]])],"derivedFrom":subQ3}),-1.0]])]});}
            var Q151;
            {var subQ3=sQuery(id+"F0.wireOp",EDGE,"E7.left");var subQ5=sQuery(id+"F0.wireOp",EDGE,"E25.bottom");var subQ7=makeQuery(id+"F0.imprint","INTERSECT",VERTEX,{"derivedFrom":[subQ3,subQ5]});Q151=makeQuery(id+"F0.imprint","IMPRINT",FACE,{"disambiguationData":[TD([[makeQuery(id+"F0.imprint","IMPRINT",EDGE,{"disambiguationData":[TD([[subQ7,-1.0]])],"derivedFrom":subQ3}),1.0]])]});}
            var Q152;
            {var subQ3=sQuery(id+"F0.wireOp",EDGE,"E7.right");var subQ5=sQuery(id+"F0.wireOp",EDGE,"E25.bottom");var subQ7=makeQuery(id+"F0.imprint","INTERSECT",VERTEX,{"derivedFrom":[subQ3,subQ5]});Q152=makeQuery(id+"F0.imprint","IMPRINT",FACE,{"disambiguationData":[TD([[makeQuery(id+"F0.imprint","IMPRINT",EDGE,{"disambiguationData":[TD([[subQ7,-1.0]])],"derivedFrom":subQ3}),1.0]])]});}
            var Q153;
            {var subQ3=sQuery(id+"F0.wireOp",EDGE,"E7.left");var subQ5=sQuery(id+"F0.wireOp",EDGE,"E24.top");var subQ7=makeQuery(id+"F0.imprint","INTERSECT",VERTEX,{"derivedFrom":[subQ3,subQ5]});Q153=makeQuery(id+"F0.imprint","IMPRINT",FACE,{"disambiguationData":[TD([[makeQuery(id+"F0.imprint","IMPRINT",EDGE,{"disambiguationData":[TD([[subQ7,-1.0]])],"derivedFrom":subQ3}),1.0]])]});}
            var Q154;
            {var subQ3=sQuery(id+"F0.wireOp",EDGE,"E7.right");var subQ5=sQuery(id+"F0.wireOp",EDGE,"E24.top");var subQ7=makeQuery(id+"F0.imprint","INTERSECT",VERTEX,{"derivedFrom":[subQ3,subQ5]});Q154=makeQuery(id+"F0.imprint","IMPRINT",FACE,{"disambiguationData":[TD([[makeQuery(id+"F0.imprint","IMPRINT",EDGE,{"disambiguationData":[TD([[subQ7,-1.0]])],"derivedFrom":subQ3}),1.0]])]});}
            var Q155;
            {var subQ3=sQuery(id+"F0.wireOp",EDGE,"E7.right");var subQ5=sQuery(id+"F0.wireOp",EDGE,"E24.bottom");var subQ7=makeQuery(id+"F0.imprint","INTERSECT",VERTEX,{"derivedFrom":[subQ3,subQ5]});Q155=makeQuery(id+"F0.imprint","IMPRINT",FACE,{"disambiguationData":[TD([[makeQuery(id+"F0.imprint","IMPRINT",EDGE,{"disambiguationData":[TD([[subQ7,-1.0]])],"derivedFrom":subQ3}),1.0]])]});}
            var Q156;
            {var subQ3=sQuery(id+"F0.wireOp",EDGE,"E7.left");var subQ5=sQuery(id+"F0.wireOp",EDGE,"E24.bottom");var subQ7=makeQuery(id+"F0.imprint","INTERSECT",VERTEX,{"derivedFrom":[subQ3,subQ5]});Q156=makeQuery(id+"F0.imprint","IMPRINT",FACE,{"disambiguationData":[TD([[makeQuery(id+"F0.imprint","IMPRINT",EDGE,{"disambiguationData":[TD([[subQ7,-1.0]])],"derivedFrom":subQ3}),1.0]])]});}
            var Q157;
            {var subQ0=sQuery(id+"F0.wireOp",EDGE,"E24.top");var subQ3=sQuery(id+"F0.wireOp",EDGE,"E6.right");var subQ4=makeQuery(id+"F0.imprint","INTERSECT",VERTEX,{"derivedFrom":[subQ3,subQ0]});Q157=makeQuery(id+"F0.imprint","IMPRINT",FACE,{"disambiguationData":[TD([[makeQuery(id+"F0.imprint","IMPRINT",EDGE,{"disambiguationData":[TD([[subQ4,-1.0]])],"derivedFrom":subQ3}),-1.0]])]});}
            var Q158;
            {var subQ0=sQuery(id+"F0.wireOp",EDGE,"E24.bottom");var subQ3=sQuery(id+"F0.wireOp",EDGE,"E6.right");var subQ4=makeQuery(id+"F0.imprint","INTERSECT",VERTEX,{"derivedFrom":[subQ3,subQ0]});Q158=makeQuery(id+"F0.imprint","IMPRINT",FACE,{"disambiguationData":[TD([[makeQuery(id+"F0.imprint","IMPRINT",EDGE,{"disambiguationData":[TD([[subQ4,-1.0]])],"derivedFrom":subQ3}),-1.0]])]});}
            var Q159;
            {var subQ0=sQuery(id+"F0.wireOp",EDGE,"E23.top");var subQ3=sQuery(id+"F0.wireOp",EDGE,"E6.right");var subQ4=makeQuery(id+"F0.imprint","INTERSECT",VERTEX,{"derivedFrom":[subQ3,subQ0]});Q159=makeQuery(id+"F0.imprint","IMPRINT",FACE,{"disambiguationData":[TD([[makeQuery(id+"F0.imprint","IMPRINT",EDGE,{"disambiguationData":[TD([[subQ4,-1.0]])],"derivedFrom":subQ3}),-1.0]])]});}
            var Q160;
            {var subQ1=sQuery(id+"F0.wireOp",EDGE,"E23.top");var subQ5=sQuery(id+"F0.wireOp",EDGE,"E6.right");var subQ6=makeQuery(id+"F0.imprint","INTERSECT",VERTEX,{"derivedFrom":[subQ5,subQ1]});Q160=makeQuery(id+"F0.imprint","IMPRINT",FACE,{"disambiguationData":[TD([[makeQuery(id+"F0.imprint","IMPRINT",EDGE,{"disambiguationData":[TD([[subQ6,-1.0]])],"derivedFrom":subQ5}),1.0]])]});}
            var Q161;
            {var subQ3=sQuery(id+"F0.wireOp",EDGE,"E23.bottom");var subQ5=sQuery(id+"F0.wireOp",EDGE,"E5.right");var subQ7=makeQuery(id+"F0.imprint","INTERSECT",VERTEX,{"derivedFrom":[subQ5,subQ3]});Q161=makeQuery(id+"F0.imprint","IMPRINT",FACE,{"disambiguationData":[TD([[makeQuery(id+"F0.imprint","IMPRINT",EDGE,{"disambiguationData":[TD([[subQ7,-1.0]])],"derivedFrom":subQ5}),1.0]])]});}
            var Q162;
            {var subQ3=sQuery(id+"F0.wireOp",EDGE,"E5.left");var subQ5=sQuery(id+"F0.wireOp",EDGE,"E23.bottom");var subQ7=makeQuery(id+"F0.imprint","INTERSECT",VERTEX,{"derivedFrom":[subQ3,subQ5]});Q162=makeQuery(id+"F0.imprint","IMPRINT",FACE,{"disambiguationData":[TD([[makeQuery(id+"F0.imprint","IMPRINT",EDGE,{"disambiguationData":[TD([[subQ7,-1.0]])],"derivedFrom":subQ3}),1.0]])]});}
            var Q163;
            {var subQ3=sQuery(id+"F0.wireOp",EDGE,"E7.left");var subQ5=sQuery(id+"F0.wireOp",EDGE,"E23.bottom");var subQ7=makeQuery(id+"F0.imprint","INTERSECT",VERTEX,{"derivedFrom":[subQ3,subQ5]});Q163=makeQuery(id+"F0.imprint","IMPRINT",FACE,{"disambiguationData":[TD([[makeQuery(id+"F0.imprint","IMPRINT",EDGE,{"disambiguationData":[TD([[subQ7,-1.0]])],"derivedFrom":subQ3}),1.0]])]});}
            var Q164;
            {var subQ3=sQuery(id+"F0.wireOp",EDGE,"E7.right");var subQ5=sQuery(id+"F0.wireOp",EDGE,"E23.bottom");var subQ7=makeQuery(id+"F0.imprint","INTERSECT",VERTEX,{"derivedFrom":[subQ3,subQ5]});Q164=makeQuery(id+"F0.imprint","IMPRINT",FACE,{"disambiguationData":[TD([[makeQuery(id+"F0.imprint","IMPRINT",EDGE,{"disambiguationData":[TD([[subQ7,-1.0]])],"derivedFrom":subQ3}),1.0]])]});}
            var Q165;
            {var subQ0=sQuery(id+"F0.wireOp",EDGE,"E23.top");var subQ3=sQuery(id+"F0.wireOp",EDGE,"E8.left");var subQ4=makeQuery(id+"F0.imprint","INTERSECT",VERTEX,{"derivedFrom":[subQ3,subQ0]});Q165=makeQuery(id+"F0.imprint","IMPRINT",FACE,{"disambiguationData":[TD([[makeQuery(id+"F0.imprint","IMPRINT",EDGE,{"disambiguationData":[TD([[subQ4,-1.0]])],"derivedFrom":subQ3}),-1.0]])]});}
            var Q166;
            {var subQ0=sQuery(id+"F0.wireOp",EDGE,"E23.bottom");var subQ3=sQuery(id+"F0.wireOp",EDGE,"E8.left");var subQ4=makeQuery(id+"F0.imprint","INTERSECT",VERTEX,{"derivedFrom":[subQ3,subQ0]});Q166=makeQuery(id+"F0.imprint","IMPRINT",FACE,{"disambiguationData":[TD([[makeQuery(id+"F0.imprint","IMPRINT",EDGE,{"disambiguationData":[TD([[subQ4,-1.0]])],"derivedFrom":subQ3}),-1.0]])]});}
            var Q167;
            {var subQ0=sQuery(id+"F0.wireOp",EDGE,"E22.top");var subQ3=sQuery(id+"F0.wireOp",EDGE,"E8.left");var subQ4=makeQuery(id+"F0.imprint","INTERSECT",VERTEX,{"derivedFrom":[subQ3,subQ0]});Q167=makeQuery(id+"F0.imprint","IMPRINT",FACE,{"disambiguationData":[TD([[makeQuery(id+"F0.imprint","IMPRINT",EDGE,{"disambiguationData":[TD([[subQ4,-1.0]])],"derivedFrom":subQ3}),-1.0]])]});}
            var Q168;
            {var subQ0=sQuery(id+"F0.wireOp",EDGE,"E22.top");var subQ3=sQuery(id+"F0.wireOp",EDGE,"E8.right");var subQ4=makeQuery(id+"F0.imprint","INTERSECT",VERTEX,{"derivedFrom":[subQ3,subQ0]});Q168=makeQuery(id+"F0.imprint","IMPRINT",FACE,{"disambiguationData":[TD([[makeQuery(id+"F0.imprint","IMPRINT",EDGE,{"disambiguationData":[TD([[subQ4,-1.0]])],"derivedFrom":subQ3}),1.0]])]});}
            var Q169;
            {var subQ3=sQuery(id+"F0.wireOp",EDGE,"E9.left");var subQ5=sQuery(id+"F0.wireOp",EDGE,"E22.bottom");var subQ7=makeQuery(id+"F0.imprint","INTERSECT",VERTEX,{"derivedFrom":[subQ3,subQ5]});Q169=makeQuery(id+"F0.imprint","IMPRINT",FACE,{"disambiguationData":[TD([[makeQuery(id+"F0.imprint","IMPRINT",EDGE,{"disambiguationData":[TD([[subQ7,-1.0]])],"derivedFrom":subQ3}),-1.0]])]});}
            var Q170;
            {var subQ0=sQuery(id+"F0.wireOp",EDGE,"E76");Q170=makeQuery(id+"F0.imprint","IMPRINT",FACE,{"disambiguationData":[TD([[makeQuery(id+"F0.imprint","IMPRINT",EDGE,{"derivedFrom":subQ0}),1.0]])]});}
            var Q171;
            {var subQ0=sQuery(id+"F0.wireOp",EDGE,"E27.bottom");var subQ3=sQuery(id+"F0.wireOp",EDGE,"E8.left");var subQ4=makeQuery(id+"F0.imprint","INTERSECT",VERTEX,{"derivedFrom":[subQ3,subQ0]});Q171=makeQuery(id+"F0.imprint","IMPRINT",FACE,{"disambiguationData":[TD([[makeQuery(id+"F0.imprint","IMPRINT",EDGE,{"disambiguationData":[TD([[subQ4,-1.0]])],"derivedFrom":subQ3}),-1.0]])]});}
            var Q172;
            {var subQ0=sQuery(id+"F0.wireOp",EDGE,"E26.top");var subQ3=sQuery(id+"F0.wireOp",EDGE,"E8.left");var subQ4=makeQuery(id+"F0.imprint","INTERSECT",VERTEX,{"derivedFrom":[subQ3,subQ0]});Q172=makeQuery(id+"F0.imprint","IMPRINT",FACE,{"disambiguationData":[TD([[makeQuery(id+"F0.imprint","IMPRINT",EDGE,{"disambiguationData":[TD([[subQ4,-1.0]])],"derivedFrom":subQ3}),-1.0]])]});}
            var Q173;
            {var subQ0=sQuery(id+"F0.wireOp",EDGE,"E26.top");var subQ3=sQuery(id+"F0.wireOp",EDGE,"E8.right");var subQ4=makeQuery(id+"F0.imprint","INTERSECT",VERTEX,{"derivedFrom":[subQ3,subQ0]});Q173=makeQuery(id+"F0.imprint","IMPRINT",FACE,{"disambiguationData":[TD([[makeQuery(id+"F0.imprint","IMPRINT",EDGE,{"disambiguationData":[TD([[subQ4,-1.0]])],"derivedFrom":subQ3}),1.0]])]});}
            var Q174;
            {var subQ0=sQuery(id+"F0.wireOp",EDGE,"E25.top");var subQ3=sQuery(id+"F0.wireOp",EDGE,"E8.right");var subQ4=makeQuery(id+"F0.imprint","INTERSECT",VERTEX,{"derivedFrom":[subQ3,subQ0]});Q174=makeQuery(id+"F0.imprint","IMPRINT",FACE,{"disambiguationData":[TD([[makeQuery(id+"F0.imprint","IMPRINT",EDGE,{"disambiguationData":[TD([[subQ4,-1.0]])],"derivedFrom":subQ3}),1.0]])]});}
            var Q175;
            {var subQ3=sQuery(id+"F0.wireOp",EDGE,"E8.right");var subQ5=sQuery(id+"F0.wireOp",EDGE,"E25.bottom");var subQ7=makeQuery(id+"F0.imprint","INTERSECT",VERTEX,{"derivedFrom":[subQ3,subQ5]});Q175=makeQuery(id+"F0.imprint","IMPRINT",FACE,{"disambiguationData":[TD([[makeQuery(id+"F0.imprint","IMPRINT",EDGE,{"disambiguationData":[TD([[subQ7,-1.0]])],"derivedFrom":subQ3}),1.0]])]});}
            var Q176;
            {var subQ3=sQuery(id+"F0.wireOp",EDGE,"E9.left");var subQ5=sQuery(id+"F0.wireOp",EDGE,"E24.top");var subQ7=makeQuery(id+"F0.imprint","INTERSECT",VERTEX,{"derivedFrom":[subQ3,subQ5]});Q176=makeQuery(id+"F0.imprint","IMPRINT",FACE,{"disambiguationData":[TD([[makeQuery(id+"F0.imprint","IMPRINT",EDGE,{"disambiguationData":[TD([[subQ7,-1.0]])],"derivedFrom":subQ3}),-1.0]])]});}
            var Q177;
            {var subQ3=sQuery(id+"F0.wireOp",EDGE,"E9.left");var subQ5=sQuery(id+"F0.wireOp",EDGE,"E24.bottom");var subQ7=makeQuery(id+"F0.imprint","INTERSECT",VERTEX,{"derivedFrom":[subQ3,subQ5]});Q177=makeQuery(id+"F0.imprint","IMPRINT",FACE,{"disambiguationData":[TD([[makeQuery(id+"F0.imprint","IMPRINT",EDGE,{"disambiguationData":[TD([[subQ7,-1.0]])],"derivedFrom":subQ3}),-1.0]])]});}
            var Q178;
            {var subQ3=sQuery(id+"F0.wireOp",EDGE,"E9.left");var subQ5=sQuery(id+"F0.wireOp",EDGE,"E24.bottom");var subQ7=makeQuery(id+"F0.imprint","INTERSECT",VERTEX,{"derivedFrom":[subQ3,subQ5]});Q178=makeQuery(id+"F0.imprint","IMPRINT",FACE,{"disambiguationData":[TD([[makeQuery(id+"F0.imprint","IMPRINT",EDGE,{"disambiguationData":[TD([[subQ7,-1.0]])],"derivedFrom":subQ3}),1.0]])]});}
            var Q179;
            {var subQ3=sQuery(id+"F0.wireOp",EDGE,"E9.left");var subQ5=sQuery(id+"F0.wireOp",EDGE,"E23.top");var subQ7=makeQuery(id+"F0.imprint","INTERSECT",VERTEX,{"derivedFrom":[subQ3,subQ5]});Q179=makeQuery(id+"F0.imprint","IMPRINT",FACE,{"disambiguationData":[TD([[makeQuery(id+"F0.imprint","IMPRINT",EDGE,{"disambiguationData":[TD([[subQ7,-1.0]])],"derivedFrom":subQ3}),-1.0]])]});}
            var Q180;
            {var subQ0=sQuery(id+"F0.wireOp",EDGE,"E24.bottom");var subQ3=sQuery(id+"F0.wireOp",EDGE,"E8.right");var subQ4=makeQuery(id+"F0.imprint","INTERSECT",VERTEX,{"derivedFrom":[subQ3,subQ0]});Q180=makeQuery(id+"F0.imprint","IMPRINT",FACE,{"disambiguationData":[TD([[makeQuery(id+"F0.imprint","IMPRINT",EDGE,{"disambiguationData":[TD([[subQ4,-1.0]])],"derivedFrom":subQ3}),1.0]])]});}
            var Q181;
            {var subQ3=sQuery(id+"F0.wireOp",EDGE,"E9.left");var subQ5=sQuery(id+"F0.wireOp",EDGE,"E26.top");var subQ7=makeQuery(id+"F0.imprint","INTERSECT",VERTEX,{"derivedFrom":[subQ3,subQ5]});Q181=makeQuery(id+"F0.imprint","IMPRINT",FACE,{"disambiguationData":[TD([[makeQuery(id+"F0.imprint","IMPRINT",EDGE,{"disambiguationData":[TD([[subQ7,-1.0]])],"derivedFrom":subQ3}),1.0]])]});}
            var Q182;
            {var subQ3=sQuery(id+"F0.wireOp",EDGE,"E9.right");var subQ5=sQuery(id+"F0.wireOp",EDGE,"E26.bottom");var subQ7=makeQuery(id+"F0.imprint","INTERSECT",VERTEX,{"derivedFrom":[subQ3,subQ5]});Q182=makeQuery(id+"F0.imprint","IMPRINT",FACE,{"disambiguationData":[TD([[makeQuery(id+"F0.imprint","IMPRINT",EDGE,{"disambiguationData":[TD([[subQ7,-1.0]])],"derivedFrom":subQ3}),1.0]])]});}
            var Q183;
            {var subQ3=sQuery(id+"F0.wireOp",EDGE,"E11.left");var subQ5=sQuery(id+"F0.wireOp",EDGE,"E26.bottom");var subQ7=makeQuery(id+"F0.imprint","INTERSECT",VERTEX,{"derivedFrom":[subQ3,subQ5]});Q183=makeQuery(id+"F0.imprint","IMPRINT",FACE,{"disambiguationData":[TD([[makeQuery(id+"F0.imprint","IMPRINT",EDGE,{"disambiguationData":[TD([[subQ7,-1.0]])],"derivedFrom":subQ3}),1.0]])]});}
            var Q184;
            {var subQ3=sQuery(id+"F0.wireOp",EDGE,"E11.left");var subQ5=sQuery(id+"F0.wireOp",EDGE,"E26.top");var subQ7=makeQuery(id+"F0.imprint","INTERSECT",VERTEX,{"derivedFrom":[subQ3,subQ5]});Q184=makeQuery(id+"F0.imprint","IMPRINT",FACE,{"disambiguationData":[TD([[makeQuery(id+"F0.imprint","IMPRINT",EDGE,{"disambiguationData":[TD([[subQ7,-1.0]])],"derivedFrom":subQ3}),1.0]])]});}
            var Q185;
            {var subQ3=sQuery(id+"F0.wireOp",EDGE,"E11.right");var subQ5=sQuery(id+"F0.wireOp",EDGE,"E26.top");var subQ7=makeQuery(id+"F0.imprint","INTERSECT",VERTEX,{"derivedFrom":[subQ3,subQ5]});Q185=makeQuery(id+"F0.imprint","IMPRINT",FACE,{"disambiguationData":[TD([[makeQuery(id+"F0.imprint","IMPRINT",EDGE,{"disambiguationData":[TD([[subQ7,-1.0]])],"derivedFrom":subQ3}),1.0]])]});}
            var Q186;
            {var subQ0=sQuery(id+"F0.wireOp",EDGE,"E21.bottom");var subQ3=sQuery(id+"F0.wireOp",EDGE,"E8.right");var subQ4=makeQuery(id+"F0.imprint","INTERSECT",VERTEX,{"derivedFrom":[subQ3,subQ0]});Q186=makeQuery(id+"F0.imprint","IMPRINT",FACE,{"disambiguationData":[TD([[makeQuery(id+"F0.imprint","IMPRINT",EDGE,{"disambiguationData":[TD([[subQ4,-1.0]])],"derivedFrom":subQ3}),1.0]])]});}
            var Q187;
            {var subQ0=sQuery(id+"F0.wireOp",EDGE,"E21.top");var subQ3=sQuery(id+"F0.wireOp",EDGE,"E8.right");var subQ4=makeQuery(id+"F0.imprint","INTERSECT",VERTEX,{"derivedFrom":[subQ3,subQ0]});Q187=makeQuery(id+"F0.imprint","IMPRINT",FACE,{"disambiguationData":[TD([[makeQuery(id+"F0.imprint","IMPRINT",EDGE,{"disambiguationData":[TD([[subQ4,-1.0]])],"derivedFrom":subQ3}),1.0]])]});}
            var Q188;
            {var subQ3=sQuery(id+"F0.wireOp",EDGE,"E9.left");var subQ5=sQuery(id+"F0.wireOp",EDGE,"E21.bottom");var subQ7=makeQuery(id+"F0.imprint","INTERSECT",VERTEX,{"derivedFrom":[subQ3,subQ5]});Q188=makeQuery(id+"F0.imprint","IMPRINT",FACE,{"disambiguationData":[TD([[makeQuery(id+"F0.imprint","IMPRINT",EDGE,{"disambiguationData":[TD([[subQ7,-1.0]])],"derivedFrom":subQ3}),-1.0]])]});}
            var Q189;
            {var subQ3=sQuery(id+"F0.wireOp",EDGE,"E9.left");var subQ5=sQuery(id+"F0.wireOp",EDGE,"E21.bottom");var subQ7=makeQuery(id+"F0.imprint","INTERSECT",VERTEX,{"derivedFrom":[subQ3,subQ5]});Q189=makeQuery(id+"F0.imprint","IMPRINT",FACE,{"disambiguationData":[TD([[makeQuery(id+"F0.imprint","IMPRINT",EDGE,{"disambiguationData":[TD([[subQ7,-1.0]])],"derivedFrom":subQ3}),1.0]])]});}
            var Q190;
            {var subQ3=sQuery(id+"F0.wireOp",EDGE,"E9.left");var subQ5=sQuery(id+"F0.wireOp",EDGE,"E20.top");var subQ7=makeQuery(id+"F0.imprint","INTERSECT",VERTEX,{"derivedFrom":[subQ3,subQ5]});Q190=makeQuery(id+"F0.imprint","IMPRINT",FACE,{"disambiguationData":[TD([[makeQuery(id+"F0.imprint","IMPRINT",EDGE,{"disambiguationData":[TD([[subQ7,-1.0]])],"derivedFrom":subQ3}),1.0]])]});}
            var Q191;
            {var subQ3=sQuery(id+"F0.wireOp",EDGE,"E9.left");var subQ5=sQuery(id+"F0.wireOp",EDGE,"E20.bottom");var subQ7=makeQuery(id+"F0.imprint","INTERSECT",VERTEX,{"derivedFrom":[subQ3,subQ5]});Q191=makeQuery(id+"F0.imprint","IMPRINT",FACE,{"disambiguationData":[TD([[makeQuery(id+"F0.imprint","IMPRINT",EDGE,{"disambiguationData":[TD([[subQ7,-1.0]])],"derivedFrom":subQ3}),-1.0]])]});}
            var Q192;
            {var subQ0=sQuery(id+"F0.wireOp",EDGE,"E20.bottom");var subQ3=sQuery(id+"F0.wireOp",EDGE,"E8.right");var subQ4=makeQuery(id+"F0.imprint","INTERSECT",VERTEX,{"derivedFrom":[subQ3,subQ0]});Q192=makeQuery(id+"F0.imprint","IMPRINT",FACE,{"disambiguationData":[TD([[makeQuery(id+"F0.imprint","IMPRINT",EDGE,{"disambiguationData":[TD([[subQ4,-1.0]])],"derivedFrom":subQ3}),1.0]])]});}
            var Q193;
            {var subQ3=sQuery(id+"F0.wireOp",EDGE,"E9.left");var subQ5=sQuery(id+"F0.wireOp",EDGE,"E19.top");var subQ7=makeQuery(id+"F0.imprint","INTERSECT",VERTEX,{"derivedFrom":[subQ3,subQ5]});Q193=makeQuery(id+"F0.imprint","IMPRINT",FACE,{"disambiguationData":[TD([[makeQuery(id+"F0.imprint","IMPRINT",EDGE,{"disambiguationData":[TD([[subQ7,-1.0]])],"derivedFrom":subQ3}),1.0]])]});}
            var Q194;
            {var subQ3=sQuery(id+"F0.wireOp",EDGE,"E9.left");var subQ5=sQuery(id+"F0.wireOp",EDGE,"E19.bottom");var subQ7=makeQuery(id+"F0.imprint","INTERSECT",VERTEX,{"derivedFrom":[subQ3,subQ5]});Q194=makeQuery(id+"F0.imprint","IMPRINT",FACE,{"disambiguationData":[TD([[makeQuery(id+"F0.imprint","IMPRINT",EDGE,{"disambiguationData":[TD([[subQ7,-1.0]])],"derivedFrom":subQ3}),1.0]])]});}
            var Q195;
            {var subQ0=sQuery(id+"F0.wireOp",EDGE,"E19.bottom");var subQ3=sQuery(id+"F0.wireOp",EDGE,"E9.left");var subQ4=makeQuery(id+"F0.imprint","INTERSECT",VERTEX,{"derivedFrom":[subQ3,subQ0]});Q195=makeQuery(id+"F0.imprint","IMPRINT",FACE,{"disambiguationData":[TD([[makeQuery(id+"F0.imprint","IMPRINT",EDGE,{"disambiguationData":[TD([[subQ4,-1.0]])],"derivedFrom":subQ3}),-1.0]])]});}
            var Q196;
            {var subQ3=sQuery(id+"F0.wireOp",EDGE,"E9.left");var subQ5=sQuery(id+"F0.wireOp",EDGE,"E18.top");var subQ7=makeQuery(id+"F0.imprint","INTERSECT",VERTEX,{"derivedFrom":[subQ3,subQ5]});Q196=makeQuery(id+"F0.imprint","IMPRINT",FACE,{"disambiguationData":[TD([[makeQuery(id+"F0.imprint","IMPRINT",EDGE,{"disambiguationData":[TD([[subQ7,-1.0]])],"derivedFrom":subQ3}),1.0]])]});}
            var Q197;
            {var subQ3=sQuery(id+"F0.wireOp",EDGE,"E9.left");var subQ5=sQuery(id+"F0.wireOp",EDGE,"E18.bottom");var subQ7=makeQuery(id+"F0.imprint","INTERSECT",VERTEX,{"derivedFrom":[subQ3,subQ5]});Q197=makeQuery(id+"F0.imprint","IMPRINT",FACE,{"disambiguationData":[TD([[makeQuery(id+"F0.imprint","IMPRINT",EDGE,{"disambiguationData":[TD([[subQ7,-1.0]])],"derivedFrom":subQ3}),1.0]])]});}
            var Q198;
            {var subQ3=sQuery(id+"F0.wireOp",EDGE,"E9.left");var subQ5=sQuery(id+"F0.wireOp",EDGE,"E17.top");var subQ7=makeQuery(id+"F0.imprint","INTERSECT",VERTEX,{"derivedFrom":[subQ3,subQ5]});Q198=makeQuery(id+"F0.imprint","IMPRINT",FACE,{"disambiguationData":[TD([[makeQuery(id+"F0.imprint","IMPRINT",EDGE,{"disambiguationData":[TD([[subQ7,-1.0]])],"derivedFrom":subQ3}),1.0]])]});}
            var Q199;
            {var subQ3=sQuery(id+"F0.wireOp",EDGE,"E9.right");var subQ5=sQuery(id+"F0.wireOp",EDGE,"E17.top");var subQ7=makeQuery(id+"F0.imprint","INTERSECT",VERTEX,{"derivedFrom":[subQ3,subQ5]});Q199=makeQuery(id+"F0.imprint","IMPRINT",FACE,{"disambiguationData":[TD([[makeQuery(id+"F0.imprint","IMPRINT",EDGE,{"disambiguationData":[TD([[subQ7,-1.0]])],"derivedFrom":subQ3}),1.0]])]});}
            var Q200;
            {var subQ3=sQuery(id+"F0.wireOp",EDGE,"E11.left");var subQ5=sQuery(id+"F0.wireOp",EDGE,"E17.top");var subQ7=makeQuery(id+"F0.imprint","INTERSECT",VERTEX,{"derivedFrom":[subQ3,subQ5]});Q200=makeQuery(id+"F0.imprint","IMPRINT",FACE,{"disambiguationData":[TD([[makeQuery(id+"F0.imprint","IMPRINT",EDGE,{"disambiguationData":[TD([[subQ7,-1.0]])],"derivedFrom":subQ3}),1.0]])]});}
            var Q201;
            {var subQ3=sQuery(id+"F0.wireOp",EDGE,"E11.left");var subQ5=sQuery(id+"F0.wireOp",EDGE,"E18.bottom");var subQ7=makeQuery(id+"F0.imprint","INTERSECT",VERTEX,{"derivedFrom":[subQ3,subQ5]});Q201=makeQuery(id+"F0.imprint","IMPRINT",FACE,{"disambiguationData":[TD([[makeQuery(id+"F0.imprint","IMPRINT",EDGE,{"disambiguationData":[TD([[subQ7,-1.0]])],"derivedFrom":subQ3}),1.0]])]});}
            var Q202;
            {var subQ3=sQuery(id+"F0.wireOp",EDGE,"E11.left");var subQ5=sQuery(id+"F0.wireOp",EDGE,"E18.top");var subQ7=makeQuery(id+"F0.imprint","INTERSECT",VERTEX,{"derivedFrom":[subQ3,subQ5]});Q202=makeQuery(id+"F0.imprint","IMPRINT",FACE,{"disambiguationData":[TD([[makeQuery(id+"F0.imprint","IMPRINT",EDGE,{"disambiguationData":[TD([[subQ7,-1.0]])],"derivedFrom":subQ3}),1.0]])]});}
            var Q203;
            {var subQ3=sQuery(id+"F0.wireOp",EDGE,"E9.right");var subQ5=sQuery(id+"F0.wireOp",EDGE,"E18.top");var subQ7=makeQuery(id+"F0.imprint","INTERSECT",VERTEX,{"derivedFrom":[subQ3,subQ5]});Q203=makeQuery(id+"F0.imprint","IMPRINT",FACE,{"disambiguationData":[TD([[makeQuery(id+"F0.imprint","IMPRINT",EDGE,{"disambiguationData":[TD([[subQ7,-1.0]])],"derivedFrom":subQ3}),1.0]])]});}
            var Q204;
            {var subQ3=sQuery(id+"F0.wireOp",EDGE,"E9.right");var subQ5=sQuery(id+"F0.wireOp",EDGE,"E19.bottom");var subQ7=makeQuery(id+"F0.imprint","INTERSECT",VERTEX,{"derivedFrom":[subQ3,subQ5]});Q204=makeQuery(id+"F0.imprint","IMPRINT",FACE,{"disambiguationData":[TD([[makeQuery(id+"F0.imprint","IMPRINT",EDGE,{"disambiguationData":[TD([[subQ7,-1.0]])],"derivedFrom":subQ3}),1.0]])]});}
            var Q205;
            {var subQ3=sQuery(id+"F0.wireOp",EDGE,"E11.left");var subQ5=sQuery(id+"F0.wireOp",EDGE,"E19.bottom");var subQ7=makeQuery(id+"F0.imprint","INTERSECT",VERTEX,{"derivedFrom":[subQ3,subQ5]});Q205=makeQuery(id+"F0.imprint","IMPRINT",FACE,{"disambiguationData":[TD([[makeQuery(id+"F0.imprint","IMPRINT",EDGE,{"disambiguationData":[TD([[subQ7,-1.0]])],"derivedFrom":subQ3}),1.0]])]});}
            var Q206;
            {var subQ3=sQuery(id+"F0.wireOp",EDGE,"E11.right");var subQ5=sQuery(id+"F0.wireOp",EDGE,"E19.bottom");var subQ7=makeQuery(id+"F0.imprint","INTERSECT",VERTEX,{"derivedFrom":[subQ3,subQ5]});Q206=makeQuery(id+"F0.imprint","IMPRINT",FACE,{"disambiguationData":[TD([[makeQuery(id+"F0.imprint","IMPRINT",EDGE,{"disambiguationData":[TD([[subQ7,-1.0]])],"derivedFrom":subQ3}),1.0]])]});}
            var Q207;
            {var subQ3=sQuery(id+"F0.wireOp",EDGE,"E11.right");var subQ5=sQuery(id+"F0.wireOp",EDGE,"E19.top");var subQ7=makeQuery(id+"F0.imprint","INTERSECT",VERTEX,{"derivedFrom":[subQ3,subQ5]});Q207=makeQuery(id+"F0.imprint","IMPRINT",FACE,{"disambiguationData":[TD([[makeQuery(id+"F0.imprint","IMPRINT",EDGE,{"disambiguationData":[TD([[subQ7,-1.0]])],"derivedFrom":subQ3}),1.0]])]});}
            var Q208;
            {var subQ3=sQuery(id+"F0.wireOp",EDGE,"E12.left");var subQ5=sQuery(id+"F0.wireOp",EDGE,"E20.bottom");var subQ7=makeQuery(id+"F0.imprint","INTERSECT",VERTEX,{"derivedFrom":[subQ3,subQ5]});Q208=makeQuery(id+"F0.imprint","IMPRINT",FACE,{"disambiguationData":[TD([[makeQuery(id+"F0.imprint","IMPRINT",EDGE,{"disambiguationData":[TD([[subQ7,-1.0]])],"derivedFrom":subQ3}),1.0]])]});}
            var Q209;
            {var subQ3=sQuery(id+"F0.wireOp",EDGE,"E11.right");var subQ5=sQuery(id+"F0.wireOp",EDGE,"E20.top");var subQ7=makeQuery(id+"F0.imprint","INTERSECT",VERTEX,{"derivedFrom":[subQ3,subQ5]});Q209=makeQuery(id+"F0.imprint","IMPRINT",FACE,{"disambiguationData":[TD([[makeQuery(id+"F0.imprint","IMPRINT",EDGE,{"disambiguationData":[TD([[subQ7,-1.0]])],"derivedFrom":subQ3}),1.0]])]});}
            var Q210;
            {var subQ3=sQuery(id+"F0.wireOp",EDGE,"E11.left");var subQ5=sQuery(id+"F0.wireOp",EDGE,"E20.bottom");var subQ7=makeQuery(id+"F0.imprint","INTERSECT",VERTEX,{"derivedFrom":[subQ3,subQ5]});Q210=makeQuery(id+"F0.imprint","IMPRINT",FACE,{"disambiguationData":[TD([[makeQuery(id+"F0.imprint","IMPRINT",EDGE,{"disambiguationData":[TD([[subQ7,-1.0]])],"derivedFrom":subQ3}),1.0]])]});}
            var Q211;
            {var subQ3=sQuery(id+"F0.wireOp",EDGE,"E9.right");var subQ5=sQuery(id+"F0.wireOp",EDGE,"E20.bottom");var subQ7=makeQuery(id+"F0.imprint","INTERSECT",VERTEX,{"derivedFrom":[subQ3,subQ5]});Q211=makeQuery(id+"F0.imprint","IMPRINT",FACE,{"disambiguationData":[TD([[makeQuery(id+"F0.imprint","IMPRINT",EDGE,{"disambiguationData":[TD([[subQ7,-1.0]])],"derivedFrom":subQ3}),1.0]])]});}
            var Q212;
            {var subQ3=sQuery(id+"F0.wireOp",EDGE,"E14.left");var subQ5=sQuery(id+"F0.wireOp",EDGE,"E16.bottom");var subQ7=makeQuery(id+"F0.imprint","INTERSECT",VERTEX,{"derivedFrom":[subQ3,subQ5]});Q212=makeQuery(id+"F0.imprint","IMPRINT",FACE,{"disambiguationData":[TD([[makeQuery(id+"F0.imprint","IMPRINT",EDGE,{"disambiguationData":[TD([[subQ7,-1.0]])],"derivedFrom":subQ3}),1.0]])]});}
            var Q213;
            {var subQ0=sQuery(id+"F0.wireOp",EDGE,"E16.top");var subQ3=sQuery(id+"F0.wireOp",EDGE,"E13.right");var subQ4=makeQuery(id+"F0.imprint","INTERSECT",VERTEX,{"derivedFrom":[subQ3,subQ0]});Q213=makeQuery(id+"F0.imprint","IMPRINT",FACE,{"disambiguationData":[TD([[makeQuery(id+"F0.imprint","IMPRINT",EDGE,{"disambiguationData":[TD([[subQ4,-1.0]])],"derivedFrom":subQ3}),-1.0]])]});}
            var Q214;
            {var subQ0=sQuery(id+"F0.wireOp",EDGE,"E16.top");var subQ3=sQuery(id+"F0.wireOp",EDGE,"E13.left");var subQ4=makeQuery(id+"F0.imprint","INTERSECT",VERTEX,{"derivedFrom":[subQ3,subQ0]});Q214=makeQuery(id+"F0.imprint","IMPRINT",FACE,{"disambiguationData":[TD([[makeQuery(id+"F0.imprint","IMPRINT",EDGE,{"disambiguationData":[TD([[subQ4,-1.0]])],"derivedFrom":subQ3}),-1.0]])]});}
            var Q215;
            {var subQ0=sQuery(id+"F0.wireOp",EDGE,"E17.bottom");var subQ3=sQuery(id+"F0.wireOp",EDGE,"E13.left");var subQ4=makeQuery(id+"F0.imprint","INTERSECT",VERTEX,{"derivedFrom":[subQ3,subQ0]});Q215=makeQuery(id+"F0.imprint","IMPRINT",FACE,{"disambiguationData":[TD([[makeQuery(id+"F0.imprint","IMPRINT",EDGE,{"disambiguationData":[TD([[subQ4,-1.0]])],"derivedFrom":subQ3}),-1.0]])]});}
            var Q216;
            {var subQ0=sQuery(id+"F0.wireOp",EDGE,"E17.bottom");var subQ3=sQuery(id+"F0.wireOp",EDGE,"E13.right");var subQ4=makeQuery(id+"F0.imprint","INTERSECT",VERTEX,{"derivedFrom":[subQ3,subQ0]});Q216=makeQuery(id+"F0.imprint","IMPRINT",FACE,{"disambiguationData":[TD([[makeQuery(id+"F0.imprint","IMPRINT",EDGE,{"disambiguationData":[TD([[subQ4,-1.0]])],"derivedFrom":subQ3}),-1.0]])]});}
            var Q217;
            {var subQ3=sQuery(id+"F0.wireOp",EDGE,"E14.left");var subQ5=sQuery(id+"F0.wireOp",EDGE,"E16.top");var subQ7=makeQuery(id+"F0.imprint","INTERSECT",VERTEX,{"derivedFrom":[subQ3,subQ5]});Q217=makeQuery(id+"F0.imprint","IMPRINT",FACE,{"disambiguationData":[TD([[makeQuery(id+"F0.imprint","IMPRINT",EDGE,{"disambiguationData":[TD([[subQ7,-1.0]])],"derivedFrom":subQ3}),1.0]])]});}
            var Q218;
            {var subQ3=sQuery(id+"F0.wireOp",EDGE,"E14.left");var subQ5=sQuery(id+"F0.wireOp",EDGE,"E17.bottom");var subQ7=makeQuery(id+"F0.imprint","INTERSECT",VERTEX,{"derivedFrom":[subQ3,subQ5]});Q218=makeQuery(id+"F0.imprint","IMPRINT",FACE,{"disambiguationData":[TD([[makeQuery(id+"F0.imprint","IMPRINT",EDGE,{"disambiguationData":[TD([[subQ7,-1.0]])],"derivedFrom":subQ3}),1.0]])]});}
            var Q219;
            {var subQ0=sQuery(id+"F0.wireOp",EDGE,"E17.top");var subQ3=sQuery(id+"F0.wireOp",EDGE,"E13.right");var subQ4=makeQuery(id+"F0.imprint","INTERSECT",VERTEX,{"derivedFrom":[subQ3,subQ0]});Q219=makeQuery(id+"F0.imprint","IMPRINT",FACE,{"disambiguationData":[TD([[makeQuery(id+"F0.imprint","IMPRINT",EDGE,{"disambiguationData":[TD([[subQ4,-1.0]])],"derivedFrom":subQ3}),-1.0]])]});}
            var Q220;
            {var subQ0=sQuery(id+"F0.wireOp",EDGE,"E17.top");var subQ3=sQuery(id+"F0.wireOp",EDGE,"E13.left");var subQ4=makeQuery(id+"F0.imprint","INTERSECT",VERTEX,{"derivedFrom":[subQ3,subQ0]});Q220=makeQuery(id+"F0.imprint","IMPRINT",FACE,{"disambiguationData":[TD([[makeQuery(id+"F0.imprint","IMPRINT",EDGE,{"disambiguationData":[TD([[subQ4,-1.0]])],"derivedFrom":subQ3}),-1.0]])]});}
            var Q221;
            {var subQ3=sQuery(id+"F0.wireOp",EDGE,"E43");Q221=makeQuery(id+"F0.imprint","IMPRINT",FACE,{"disambiguationData":[TD([[makeQuery(id+"F0.imprint","IMPRINT",EDGE,{"derivedFrom":subQ3}),-1.0]])]});}
            var Q222;
            {var subQ3=sQuery(id+"F0.wireOp",EDGE,"E14.bottom");Q222=makeQuery(id+"F0.imprint","IMPRINT",FACE,{"disambiguationData":[TD([[makeQuery(id+"F0.imprint","IMPRINT",EDGE,{"derivedFrom":subQ3}),-1.0]])]});}
            var Q223;
            {var subQ0=sQuery(id+"F0.wireOp",EDGE,"E42");Q223=makeQuery(id+"F0.imprint","IMPRINT",FACE,{"disambiguationData":[TD([[makeQuery(id+"F0.imprint","IMPRINT",EDGE,{"derivedFrom":subQ0}),-1.0]])]});}
            var Q224;
            {var subQ5=sQuery(id+"F0.wireOp",EDGE,"E13.top");Q224=makeQuery(id+"F0.imprint","IMPRINT",FACE,{"disambiguationData":[TD([[makeQuery(id+"F0.imprint","IMPRINT",EDGE,{"derivedFrom":subQ5}),-1.0]])]});}
            var Q225;
            {var subQ0=sQuery(id+"F0.wireOp",EDGE,"E41");Q225=makeQuery(id+"F0.imprint","IMPRINT",FACE,{"disambiguationData":[TD([[makeQuery(id+"F0.imprint","IMPRINT",EDGE,{"derivedFrom":subQ0}),-1.0]])]});}
            var Q226;
            {var subQ5=sQuery(id+"F0.wireOp",EDGE,"E12.bottom");Q226=makeQuery(id+"F0.imprint","IMPRINT",FACE,{"disambiguationData":[TD([[makeQuery(id+"F0.imprint","IMPRINT",EDGE,{"derivedFrom":subQ5}),-1.0]])]});}
            var Q227;
            {var subQ3=sQuery(id+"F0.wireOp",EDGE,"E12.left");var subQ5=sQuery(id+"F0.wireOp",EDGE,"E15.top");var subQ7=makeQuery(id+"F0.imprint","INTERSECT",VERTEX,{"derivedFrom":[subQ3,subQ5]});Q227=makeQuery(id+"F0.imprint","IMPRINT",FACE,{"disambiguationData":[TD([[makeQuery(id+"F0.imprint","IMPRINT",EDGE,{"disambiguationData":[TD([[subQ7,-1.0]])],"derivedFrom":subQ3}),1.0]])]});}
            var Q228;
            {var subQ0=sQuery(id+"F0.wireOp",EDGE,"E16.bottom");var subQ3=sQuery(id+"F0.wireOp",EDGE,"E12.left");var subQ4=makeQuery(id+"F0.imprint","INTERSECT",VERTEX,{"derivedFrom":[subQ3,subQ0]});Q228=makeQuery(id+"F0.imprint","IMPRINT",FACE,{"disambiguationData":[TD([[makeQuery(id+"F0.imprint","IMPRINT",EDGE,{"disambiguationData":[TD([[subQ4,-1.0]])],"derivedFrom":subQ3}),1.0]])]});}
            var Q229;
            {var subQ3=sQuery(id+"F0.wireOp",EDGE,"E12.left");var subQ5=sQuery(id+"F0.wireOp",EDGE,"E16.top");var subQ7=makeQuery(id+"F0.imprint","INTERSECT",VERTEX,{"derivedFrom":[subQ3,subQ5]});Q229=makeQuery(id+"F0.imprint","IMPRINT",FACE,{"disambiguationData":[TD([[makeQuery(id+"F0.imprint","IMPRINT",EDGE,{"disambiguationData":[TD([[subQ7,-1.0]])],"derivedFrom":subQ3}),1.0]])]});}
            var Q230;
            {var subQ3=sQuery(id+"F0.wireOp",EDGE,"E12.left");var subQ5=sQuery(id+"F0.wireOp",EDGE,"E17.bottom");var subQ7=makeQuery(id+"F0.imprint","INTERSECT",VERTEX,{"derivedFrom":[subQ3,subQ5]});Q230=makeQuery(id+"F0.imprint","IMPRINT",FACE,{"disambiguationData":[TD([[makeQuery(id+"F0.imprint","IMPRINT",EDGE,{"disambiguationData":[TD([[subQ7,-1.0]])],"derivedFrom":subQ3}),1.0]])]});}
            var Q231;
            {var subQ3=sQuery(id+"F0.wireOp",EDGE,"E12.left");var subQ5=sQuery(id+"F0.wireOp",EDGE,"E17.top");var subQ7=makeQuery(id+"F0.imprint","INTERSECT",VERTEX,{"derivedFrom":[subQ3,subQ5]});Q231=makeQuery(id+"F0.imprint","IMPRINT",FACE,{"disambiguationData":[TD([[makeQuery(id+"F0.imprint","IMPRINT",EDGE,{"disambiguationData":[TD([[subQ7,-1.0]])],"derivedFrom":subQ3}),1.0]])]});}
            var Q232;
            {var subQ0=sQuery(id+"F0.wireOp",EDGE,"E18.bottom");var subQ3=sQuery(id+"F0.wireOp",EDGE,"E12.left");var subQ4=makeQuery(id+"F0.imprint","INTERSECT",VERTEX,{"derivedFrom":[subQ3,subQ0]});Q232=makeQuery(id+"F0.imprint","IMPRINT",FACE,{"disambiguationData":[TD([[makeQuery(id+"F0.imprint","IMPRINT",EDGE,{"disambiguationData":[TD([[subQ4,-1.0]])],"derivedFrom":subQ3}),1.0]])]});}
            var Q233;
            {var subQ3=sQuery(id+"F0.wireOp",EDGE,"E12.right");var subQ5=sQuery(id+"F0.wireOp",EDGE,"E18.bottom");var subQ7=makeQuery(id+"F0.imprint","INTERSECT",VERTEX,{"derivedFrom":[subQ3,subQ5]});Q233=makeQuery(id+"F0.imprint","IMPRINT",FACE,{"disambiguationData":[TD([[makeQuery(id+"F0.imprint","IMPRINT",EDGE,{"disambiguationData":[TD([[subQ7,-1.0]])],"derivedFrom":subQ3}),1.0]])]});}
            var Q234;
            {var subQ0=sQuery(id+"F0.wireOp",EDGE,"E18.top");var subQ3=sQuery(id+"F0.wireOp",EDGE,"E13.left");var subQ4=makeQuery(id+"F0.imprint","INTERSECT",VERTEX,{"derivedFrom":[subQ3,subQ0]});Q234=makeQuery(id+"F0.imprint","IMPRINT",FACE,{"disambiguationData":[TD([[makeQuery(id+"F0.imprint","IMPRINT",EDGE,{"disambiguationData":[TD([[subQ4,-1.0]])],"derivedFrom":subQ3}),-1.0]])]});}
            var Q235;
            {var subQ0=sQuery(id+"F0.wireOp",EDGE,"E18.top");var subQ3=sQuery(id+"F0.wireOp",EDGE,"E13.right");var subQ4=makeQuery(id+"F0.imprint","INTERSECT",VERTEX,{"derivedFrom":[subQ3,subQ0]});Q235=makeQuery(id+"F0.imprint","IMPRINT",FACE,{"disambiguationData":[TD([[makeQuery(id+"F0.imprint","IMPRINT",EDGE,{"disambiguationData":[TD([[subQ4,-1.0]])],"derivedFrom":subQ3}),-1.0]])]});}
            var Q236;
            {var subQ3=sQuery(id+"F0.wireOp",EDGE,"E14.left");var subQ5=sQuery(id+"F0.wireOp",EDGE,"E18.bottom");var subQ7=makeQuery(id+"F0.imprint","INTERSECT",VERTEX,{"derivedFrom":[subQ3,subQ5]});Q236=makeQuery(id+"F0.imprint","IMPRINT",FACE,{"disambiguationData":[TD([[makeQuery(id+"F0.imprint","IMPRINT",EDGE,{"disambiguationData":[TD([[subQ7,-1.0]])],"derivedFrom":subQ3}),1.0]])]});}
            var Q237;
            {var subQ3=sQuery(id+"F0.wireOp",EDGE,"E18.bottom");var subQ5=sQuery(id+"F0.wireOp",EDGE,"E14.right");var subQ7=makeQuery(id+"F0.imprint","INTERSECT",VERTEX,{"derivedFrom":[subQ5,subQ3]});Q237=makeQuery(id+"F0.imprint","IMPRINT",FACE,{"disambiguationData":[TD([[makeQuery(id+"F0.imprint","IMPRINT",EDGE,{"disambiguationData":[TD([[subQ7,-1.0]])],"derivedFrom":subQ5}),1.0]])]});}
            var Q238;
            {var subQ0=sQuery(id+"F0.wireOp",EDGE,"E88.right");var subQ3=sQuery(id+"F0.wireOp",EDGE,"E18.bottom");var subQ4=makeQuery(id+"F0.imprint","INTERSECT",VERTEX,{"derivedFrom":[subQ3,subQ0]});Q238=makeQuery(id+"F0.imprint","IMPRINT",FACE,{"disambiguationData":[TD([[makeQuery(id+"F0.imprint","IMPRINT",EDGE,{"disambiguationData":[TD([[subQ4,-1.0]])],"derivedFrom":subQ3}),1.0]])]});}
            var Q239;
            {var subQ0=sQuery(id+"F0.wireOp",EDGE,"E19.top");var subQ3=sQuery(id+"F0.wireOp",EDGE,"E13.right");var subQ4=makeQuery(id+"F0.imprint","INTERSECT",VERTEX,{"derivedFrom":[subQ3,subQ0]});Q239=makeQuery(id+"F0.imprint","IMPRINT",FACE,{"disambiguationData":[TD([[makeQuery(id+"F0.imprint","IMPRINT",EDGE,{"disambiguationData":[TD([[subQ4,-1.0]])],"derivedFrom":subQ3}),-1.0]])]});}
            var Q240;
            {var subQ3=sQuery(id+"F0.wireOp",EDGE,"E12.right");var subQ5=sQuery(id+"F0.wireOp",EDGE,"E19.top");var subQ7=makeQuery(id+"F0.imprint","INTERSECT",VERTEX,{"derivedFrom":[subQ3,subQ5]});Q240=makeQuery(id+"F0.imprint","IMPRINT",FACE,{"disambiguationData":[TD([[makeQuery(id+"F0.imprint","IMPRINT",EDGE,{"disambiguationData":[TD([[subQ7,-1.0]])],"derivedFrom":subQ3}),1.0]])]});}
            var Q241;
            {var subQ3=sQuery(id+"F0.wireOp",EDGE,"E12.right");var subQ5=sQuery(id+"F0.wireOp",EDGE,"E19.bottom");var subQ7=makeQuery(id+"F0.imprint","INTERSECT",VERTEX,{"derivedFrom":[subQ3,subQ5]});Q241=makeQuery(id+"F0.imprint","IMPRINT",FACE,{"disambiguationData":[TD([[makeQuery(id+"F0.imprint","IMPRINT",EDGE,{"disambiguationData":[TD([[subQ7,-1.0]])],"derivedFrom":subQ3}),1.0]])]});}
            var Q242;
            {var subQ0=sQuery(id+"F0.wireOp",EDGE,"E20.top");var subQ3=sQuery(id+"F0.wireOp",EDGE,"E13.left");var subQ4=makeQuery(id+"F0.imprint","INTERSECT",VERTEX,{"derivedFrom":[subQ3,subQ0]});Q242=makeQuery(id+"F0.imprint","IMPRINT",FACE,{"disambiguationData":[TD([[makeQuery(id+"F0.imprint","IMPRINT",EDGE,{"disambiguationData":[TD([[subQ4,-1.0]])],"derivedFrom":subQ3}),-1.0]])]});}
            var Q243;
            {var subQ0=sQuery(id+"F0.wireOp",EDGE,"E20.top");var subQ3=sQuery(id+"F0.wireOp",EDGE,"E13.right");var subQ4=makeQuery(id+"F0.imprint","INTERSECT",VERTEX,{"derivedFrom":[subQ3,subQ0]});Q243=makeQuery(id+"F0.imprint","IMPRINT",FACE,{"disambiguationData":[TD([[makeQuery(id+"F0.imprint","IMPRINT",EDGE,{"disambiguationData":[TD([[subQ4,-1.0]])],"derivedFrom":subQ3}),-1.0]])]});}
            var Q244;
            {var subQ0=sQuery(id+"F0.wireOp",EDGE,"E21.bottom");var subQ3=sQuery(id+"F0.wireOp",EDGE,"E12.left");var subQ4=makeQuery(id+"F0.imprint","INTERSECT",VERTEX,{"derivedFrom":[subQ3,subQ0]});Q244=makeQuery(id+"F0.imprint","IMPRINT",FACE,{"disambiguationData":[TD([[makeQuery(id+"F0.imprint","IMPRINT",EDGE,{"disambiguationData":[TD([[subQ4,-1.0]])],"derivedFrom":subQ3}),1.0]])]});}
            var Q245;
            {var subQ3=sQuery(id+"F0.wireOp",EDGE,"E12.right");var subQ5=sQuery(id+"F0.wireOp",EDGE,"E21.bottom");var subQ7=makeQuery(id+"F0.imprint","INTERSECT",VERTEX,{"derivedFrom":[subQ3,subQ5]});Q245=makeQuery(id+"F0.imprint","IMPRINT",FACE,{"disambiguationData":[TD([[makeQuery(id+"F0.imprint","IMPRINT",EDGE,{"disambiguationData":[TD([[subQ7,-1.0]])],"derivedFrom":subQ3}),1.0]])]});}
            var Q246;
            {var subQ0=sQuery(id+"F0.wireOp",EDGE,"E21.top");var subQ3=sQuery(id+"F0.wireOp",EDGE,"E13.left");var subQ4=makeQuery(id+"F0.imprint","INTERSECT",VERTEX,{"derivedFrom":[subQ3,subQ0]});Q246=makeQuery(id+"F0.imprint","IMPRINT",FACE,{"disambiguationData":[TD([[makeQuery(id+"F0.imprint","IMPRINT",EDGE,{"disambiguationData":[TD([[subQ4,-1.0]])],"derivedFrom":subQ3}),-1.0]])]});}
            var Q247;
            {var subQ3=sQuery(id+"F0.wireOp",EDGE,"E12.right");var subQ5=sQuery(id+"F0.wireOp",EDGE,"E21.top");var subQ7=makeQuery(id+"F0.imprint","INTERSECT",VERTEX,{"derivedFrom":[subQ3,subQ5]});Q247=makeQuery(id+"F0.imprint","IMPRINT",FACE,{"disambiguationData":[TD([[makeQuery(id+"F0.imprint","IMPRINT",EDGE,{"disambiguationData":[TD([[subQ7,-1.0]])],"derivedFrom":subQ3}),1.0]])]});}
            var Q248;
            {var subQ3=sQuery(id+"F0.wireOp",EDGE,"E12.right");var subQ5=sQuery(id+"F0.wireOp",EDGE,"E22.bottom");var subQ7=makeQuery(id+"F0.imprint","INTERSECT",VERTEX,{"derivedFrom":[subQ3,subQ5]});Q248=makeQuery(id+"F0.imprint","IMPRINT",FACE,{"disambiguationData":[TD([[makeQuery(id+"F0.imprint","IMPRINT",EDGE,{"disambiguationData":[TD([[subQ7,-1.0]])],"derivedFrom":subQ3}),1.0]])]});}
            var Q249;
            {var subQ0=sQuery(id+"F0.wireOp",EDGE,"E22.bottom");var subQ3=sQuery(id+"F0.wireOp",EDGE,"E13.right");var subQ4=makeQuery(id+"F0.imprint","INTERSECT",VERTEX,{"derivedFrom":[subQ3,subQ0]});Q249=makeQuery(id+"F0.imprint","IMPRINT",FACE,{"disambiguationData":[TD([[makeQuery(id+"F0.imprint","IMPRINT",EDGE,{"disambiguationData":[TD([[subQ4,-1.0]])],"derivedFrom":subQ3}),-1.0]])]});}
            var Q250;
            {var subQ3=sQuery(id+"F0.wireOp",EDGE,"E13.right");var subQ5=sQuery(id+"F0.wireOp",EDGE,"E22.top");var subQ7=makeQuery(id+"F0.imprint","INTERSECT",VERTEX,{"derivedFrom":[subQ3,subQ5]});Q250=makeQuery(id+"F0.imprint","IMPRINT",FACE,{"disambiguationData":[TD([[makeQuery(id+"F0.imprint","IMPRINT",EDGE,{"disambiguationData":[TD([[subQ7,-1.0]])],"derivedFrom":subQ3}),-1.0]])]});}
            var Q251;
            {var subQ0=sQuery(id+"F0.wireOp",EDGE,"E23.bottom");var subQ3=sQuery(id+"F0.wireOp",EDGE,"E13.right");var subQ4=makeQuery(id+"F0.imprint","INTERSECT",VERTEX,{"derivedFrom":[subQ3,subQ0]});Q251=makeQuery(id+"F0.imprint","IMPRINT",FACE,{"disambiguationData":[TD([[makeQuery(id+"F0.imprint","IMPRINT",EDGE,{"disambiguationData":[TD([[subQ4,-1.0]])],"derivedFrom":subQ3}),-1.0]])]});}
            var Q252;
            {var subQ3=sQuery(id+"F0.wireOp",EDGE,"E19.bottom");var subQ5=sQuery(id+"F0.wireOp",EDGE,"E14.right");var subQ7=makeQuery(id+"F0.imprint","INTERSECT",VERTEX,{"derivedFrom":[subQ5,subQ3]});Q252=makeQuery(id+"F0.imprint","IMPRINT",FACE,{"disambiguationData":[TD([[makeQuery(id+"F0.imprint","IMPRINT",EDGE,{"disambiguationData":[TD([[subQ7,-1.0]])],"derivedFrom":subQ5}),1.0]])]});}
            var Q253;
            {var subQ3=sQuery(id+"F0.wireOp",EDGE,"E19.top");var subQ5=sQuery(id+"F0.wireOp",EDGE,"E14.right");var subQ7=makeQuery(id+"F0.imprint","INTERSECT",VERTEX,{"derivedFrom":[subQ5,subQ3]});Q253=makeQuery(id+"F0.imprint","IMPRINT",FACE,{"disambiguationData":[TD([[makeQuery(id+"F0.imprint","IMPRINT",EDGE,{"disambiguationData":[TD([[subQ7,-1.0]])],"derivedFrom":subQ5}),1.0]])]});}
            var Q254;
            {var subQ3=sQuery(id+"F0.wireOp",EDGE,"E20.bottom");var subQ5=sQuery(id+"F0.wireOp",EDGE,"E14.right");var subQ7=makeQuery(id+"F0.imprint","INTERSECT",VERTEX,{"derivedFrom":[subQ5,subQ3]});Q254=makeQuery(id+"F0.imprint","IMPRINT",FACE,{"disambiguationData":[TD([[makeQuery(id+"F0.imprint","IMPRINT",EDGE,{"disambiguationData":[TD([[subQ7,-1.0]])],"derivedFrom":subQ5}),1.0]])]});}
            var Q255;
            {var subQ0=sQuery(id+"F0.wireOp",EDGE,"E88.right");var subQ3=sQuery(id+"F0.wireOp",EDGE,"E20.bottom");var subQ4=makeQuery(id+"F0.imprint","INTERSECT",VERTEX,{"derivedFrom":[subQ3,subQ0]});Q255=makeQuery(id+"F0.imprint","IMPRINT",FACE,{"disambiguationData":[TD([[makeQuery(id+"F0.imprint","IMPRINT",EDGE,{"disambiguationData":[TD([[subQ4,-1.0]])],"derivedFrom":subQ3}),1.0]])]});}
            var Q256;
            {var subQ0=sQuery(id+"F0.wireOp",EDGE,"E88.right");var subQ3=sQuery(id+"F0.wireOp",EDGE,"E20.top");var subQ4=makeQuery(id+"F0.imprint","INTERSECT",VERTEX,{"derivedFrom":[subQ3,subQ0]});Q256=makeQuery(id+"F0.imprint","IMPRINT",FACE,{"disambiguationData":[TD([[makeQuery(id+"F0.imprint","IMPRINT",EDGE,{"disambiguationData":[TD([[subQ4,-1.0]])],"derivedFrom":subQ3}),1.0]])]});}
            var Q257;
            {var subQ0=sQuery(id+"F0.wireOp",EDGE,"E88.right");var subQ3=sQuery(id+"F0.wireOp",EDGE,"E21.bottom");var subQ4=makeQuery(id+"F0.imprint","INTERSECT",VERTEX,{"derivedFrom":[subQ3,subQ0]});Q257=makeQuery(id+"F0.imprint","IMPRINT",FACE,{"disambiguationData":[TD([[makeQuery(id+"F0.imprint","IMPRINT",EDGE,{"disambiguationData":[TD([[subQ4,1.0]])],"derivedFrom":subQ3}),-1.0]])]});}
            var Q258;
            {var subQ3=sQuery(id+"F0.wireOp",EDGE,"E21.bottom");var subQ5=sQuery(id+"F0.wireOp",EDGE,"E14.right");var subQ7=makeQuery(id+"F0.imprint","INTERSECT",VERTEX,{"derivedFrom":[subQ5,subQ3]});Q258=makeQuery(id+"F0.imprint","IMPRINT",FACE,{"disambiguationData":[TD([[makeQuery(id+"F0.imprint","IMPRINT",EDGE,{"disambiguationData":[TD([[subQ7,-1.0]])],"derivedFrom":subQ5}),1.0]])]});}
            var Q259;
            {var subQ0=sQuery(id+"F0.wireOp",EDGE,"E21.bottom");var subQ3=sQuery(id+"F0.wireOp",EDGE,"E14.left");var subQ4=makeQuery(id+"F0.imprint","INTERSECT",VERTEX,{"derivedFrom":[subQ3,subQ0]});Q259=makeQuery(id+"F0.imprint","IMPRINT",FACE,{"disambiguationData":[TD([[makeQuery(id+"F0.imprint","IMPRINT",EDGE,{"disambiguationData":[TD([[subQ4,-1.0]])],"derivedFrom":subQ3}),1.0]])]});}
            var Q260;
            {var subQ3=sQuery(id+"F0.wireOp",EDGE,"E21.top");var subQ5=sQuery(id+"F0.wireOp",EDGE,"E14.right");var subQ7=makeQuery(id+"F0.imprint","INTERSECT",VERTEX,{"derivedFrom":[subQ5,subQ3]});Q260=makeQuery(id+"F0.imprint","IMPRINT",FACE,{"disambiguationData":[TD([[makeQuery(id+"F0.imprint","IMPRINT",EDGE,{"disambiguationData":[TD([[subQ7,-1.0]])],"derivedFrom":subQ5}),1.0]])]});}
            var Q261;
            {var subQ3=sQuery(id+"F0.wireOp",EDGE,"E22.bottom");var subQ5=sQuery(id+"F0.wireOp",EDGE,"E14.right");var subQ7=makeQuery(id+"F0.imprint","INTERSECT",VERTEX,{"derivedFrom":[subQ5,subQ3]});Q261=makeQuery(id+"F0.imprint","IMPRINT",FACE,{"disambiguationData":[TD([[makeQuery(id+"F0.imprint","IMPRINT",EDGE,{"disambiguationData":[TD([[subQ7,-1.0]])],"derivedFrom":subQ5}),1.0]])]});}
            var Q262;
            {var subQ0=sQuery(id+"F0.wireOp",EDGE,"E88.right");var subQ3=sQuery(id+"F0.wireOp",EDGE,"E22.bottom");var subQ4=makeQuery(id+"F0.imprint","INTERSECT",VERTEX,{"derivedFrom":[subQ3,subQ0]});Q262=makeQuery(id+"F0.imprint","IMPRINT",FACE,{"disambiguationData":[TD([[makeQuery(id+"F0.imprint","IMPRINT",EDGE,{"disambiguationData":[TD([[subQ4,-1.0]])],"derivedFrom":subQ3}),1.0]])]});}
            var Q263;
            {var subQ0=sQuery(id+"F0.wireOp",EDGE,"E88.right");var subQ3=sQuery(id+"F0.wireOp",EDGE,"E22.top");var subQ4=makeQuery(id+"F0.imprint","INTERSECT",VERTEX,{"derivedFrom":[subQ3,subQ0]});Q263=makeQuery(id+"F0.imprint","IMPRINT",FACE,{"disambiguationData":[TD([[makeQuery(id+"F0.imprint","IMPRINT",EDGE,{"disambiguationData":[TD([[subQ4,-1.0]])],"derivedFrom":subQ3}),1.0]])]});}
            var Q264;
            {var subQ0=sQuery(id+"F0.wireOp",EDGE,"E82");Q264=makeQuery(id+"F0.imprint","IMPRINT",FACE,{"disambiguationData":[TD([[makeQuery(id+"F0.imprint","IMPRINT",EDGE,{"derivedFrom":subQ0}),1.0]])]});}
            var Q265;
            {var subQ0=sQuery(id+"F0.wireOp",EDGE,"E83");Q265=makeQuery(id+"F0.imprint","IMPRINT",FACE,{"disambiguationData":[TD([[makeQuery(id+"F0.imprint","IMPRINT",EDGE,{"derivedFrom":subQ0}),1.0]])]});}
            var Q266;
            {var subQ0=sQuery(id+"F0.wireOp",EDGE,"E84");Q266=makeQuery(id+"F0.imprint","IMPRINT",FACE,{"disambiguationData":[TD([[makeQuery(id+"F0.imprint","IMPRINT",EDGE,{"derivedFrom":subQ0}),1.0]])]});}
            var Q267;
            {var subQ0=sQuery(id+"F0.wireOp",EDGE,"E85");Q267=makeQuery(id+"F0.imprint","IMPRINT",FACE,{"disambiguationData":[TD([[makeQuery(id+"F0.imprint","IMPRINT",EDGE,{"derivedFrom":subQ0}),1.0]])]});}
            var Q268;
            {var subQ0=sQuery(id+"F0.wireOp",EDGE,"E86");Q268=makeQuery(id+"F0.imprint","IMPRINT",FACE,{"disambiguationData":[TD([[makeQuery(id+"F0.imprint","IMPRINT",EDGE,{"derivedFrom":subQ0}),1.0]])]});}
            var Q269;
            {var subQ3=sQuery(id+"F0.wireOp",EDGE,"E87");Q269=makeQuery(id+"F0.imprint","IMPRINT",FACE,{"disambiguationData":[TD([[makeQuery(id+"F0.imprint","IMPRINT",EDGE,{"derivedFrom":subQ3}),1.0]])]});}
            var Q270;
            {var subQ1=sQuery(id+"F0.wireOp",EDGE,"E88.top");Q270=makeQuery(id+"F0.imprint","IMPRINT",FACE,{"disambiguationData":[TD([[makeQuery(id+"F0.imprint","IMPRINT",EDGE,{"derivedFrom":subQ1}),1.0]])]});}
            var Q271;
            {var subQ0=sQuery(id+"F0.wireOp",EDGE,"E88.right");var subQ3=sQuery(id+"F0.wireOp",EDGE,"E26.top");var subQ4=makeQuery(id+"F0.imprint","INTERSECT",VERTEX,{"derivedFrom":[subQ3,subQ0]});Q271=makeQuery(id+"F0.imprint","IMPRINT",FACE,{"disambiguationData":[TD([[makeQuery(id+"F0.imprint","IMPRINT",EDGE,{"disambiguationData":[TD([[subQ4,-1.0]])],"derivedFrom":subQ3}),1.0]])]});}
            var Q272;
            {var subQ0=sQuery(id+"F0.wireOp",EDGE,"E88.right");var subQ3=sQuery(id+"F0.wireOp",EDGE,"E26.bottom");var subQ4=makeQuery(id+"F0.imprint","INTERSECT",VERTEX,{"derivedFrom":[subQ3,subQ0]});Q272=makeQuery(id+"F0.imprint","IMPRINT",FACE,{"disambiguationData":[TD([[makeQuery(id+"F0.imprint","IMPRINT",EDGE,{"disambiguationData":[TD([[subQ4,-1.0]])],"derivedFrom":subQ3}),1.0]])]});}
            var Q273;
            {var subQ0=sQuery(id+"F0.wireOp",EDGE,"E88.right");var subQ3=sQuery(id+"F0.wireOp",EDGE,"E25.top");var subQ4=makeQuery(id+"F0.imprint","INTERSECT",VERTEX,{"derivedFrom":[subQ3,subQ0]});Q273=makeQuery(id+"F0.imprint","IMPRINT",FACE,{"disambiguationData":[TD([[makeQuery(id+"F0.imprint","IMPRINT",EDGE,{"disambiguationData":[TD([[subQ4,1.0]])],"derivedFrom":subQ3}),-1.0]])]});}
            var Q274;
            {var subQ0=sQuery(id+"F0.wireOp",EDGE,"E88.right");var subQ3=sQuery(id+"F0.wireOp",EDGE,"E25.bottom");var subQ4=makeQuery(id+"F0.imprint","INTERSECT",VERTEX,{"derivedFrom":[subQ3,subQ0]});Q274=makeQuery(id+"F0.imprint","IMPRINT",FACE,{"disambiguationData":[TD([[makeQuery(id+"F0.imprint","IMPRINT",EDGE,{"disambiguationData":[TD([[subQ4,1.0]])],"derivedFrom":subQ3}),-1.0]])]});}
            var Q275;
            {var subQ0=sQuery(id+"F0.wireOp",EDGE,"E88.right");var subQ3=sQuery(id+"F0.wireOp",EDGE,"E24.top");var subQ4=makeQuery(id+"F0.imprint","INTERSECT",VERTEX,{"derivedFrom":[subQ3,subQ0]});Q275=makeQuery(id+"F0.imprint","IMPRINT",FACE,{"disambiguationData":[TD([[makeQuery(id+"F0.imprint","IMPRINT",EDGE,{"disambiguationData":[TD([[subQ4,-1.0]])],"derivedFrom":subQ3}),1.0]])]});}
            var Q276;
            {var subQ0=sQuery(id+"F0.wireOp",EDGE,"E88.right");var subQ3=sQuery(id+"F0.wireOp",EDGE,"E24.bottom");var subQ4=makeQuery(id+"F0.imprint","INTERSECT",VERTEX,{"derivedFrom":[subQ3,subQ0]});Q276=makeQuery(id+"F0.imprint","IMPRINT",FACE,{"disambiguationData":[TD([[makeQuery(id+"F0.imprint","IMPRINT",EDGE,{"disambiguationData":[TD([[subQ4,-1.0]])],"derivedFrom":subQ3}),1.0]])]});}
            var Q277;
            {var subQ3=sQuery(id+"F0.wireOp",EDGE,"E24.bottom");var subQ5=sQuery(id+"F0.wireOp",EDGE,"E14.right");var subQ7=makeQuery(id+"F0.imprint","INTERSECT",VERTEX,{"derivedFrom":[subQ5,subQ3]});Q277=makeQuery(id+"F0.imprint","IMPRINT",FACE,{"disambiguationData":[TD([[makeQuery(id+"F0.imprint","IMPRINT",EDGE,{"disambiguationData":[TD([[subQ7,-1.0]])],"derivedFrom":subQ5}),1.0]])]});}
            var Q278;
            {var subQ3=sQuery(id+"F0.wireOp",EDGE,"E14.left");var subQ5=sQuery(id+"F0.wireOp",EDGE,"E24.bottom");var subQ7=makeQuery(id+"F0.imprint","INTERSECT",VERTEX,{"derivedFrom":[subQ3,subQ5]});Q278=makeQuery(id+"F0.imprint","IMPRINT",FACE,{"disambiguationData":[TD([[makeQuery(id+"F0.imprint","IMPRINT",EDGE,{"disambiguationData":[TD([[subQ7,-1.0]])],"derivedFrom":subQ3}),1.0]])]});}
            var Q279;
            {var subQ3=sQuery(id+"F0.wireOp",EDGE,"E14.left");var subQ5=sQuery(id+"F0.wireOp",EDGE,"E23.top");var subQ7=makeQuery(id+"F0.imprint","INTERSECT",VERTEX,{"derivedFrom":[subQ3,subQ5]});Q279=makeQuery(id+"F0.imprint","IMPRINT",FACE,{"disambiguationData":[TD([[makeQuery(id+"F0.imprint","IMPRINT",EDGE,{"disambiguationData":[TD([[subQ7,-1.0]])],"derivedFrom":subQ3}),1.0]])]});}
            var Q280;
            {var subQ0=sQuery(id+"F0.wireOp",EDGE,"E23.bottom");var subQ3=sQuery(id+"F0.wireOp",EDGE,"E14.left");var subQ4=makeQuery(id+"F0.imprint","INTERSECT",VERTEX,{"derivedFrom":[subQ3,subQ0]});Q280=makeQuery(id+"F0.imprint","IMPRINT",FACE,{"disambiguationData":[TD([[makeQuery(id+"F0.imprint","IMPRINT",EDGE,{"disambiguationData":[TD([[subQ4,-1.0]])],"derivedFrom":subQ3}),1.0]])]});}
            var Q281;
            {var subQ0=sQuery(id+"F0.wireOp",EDGE,"E24.bottom");var subQ3=sQuery(id+"F0.wireOp",EDGE,"E13.right");var subQ4=makeQuery(id+"F0.imprint","INTERSECT",VERTEX,{"derivedFrom":[subQ3,subQ0]});Q281=makeQuery(id+"F0.imprint","IMPRINT",FACE,{"disambiguationData":[TD([[makeQuery(id+"F0.imprint","IMPRINT",EDGE,{"disambiguationData":[TD([[subQ4,-1.0]])],"derivedFrom":subQ3}),-1.0]])]});}
            var Q282;
            {var subQ3=sQuery(id+"F0.wireOp",EDGE,"E13.left");var subQ5=sQuery(id+"F0.wireOp",EDGE,"E23.top");var subQ7=makeQuery(id+"F0.imprint","INTERSECT",VERTEX,{"derivedFrom":[subQ3,subQ5]});Q282=makeQuery(id+"F0.imprint","IMPRINT",FACE,{"disambiguationData":[TD([[makeQuery(id+"F0.imprint","IMPRINT",EDGE,{"disambiguationData":[TD([[subQ7,-1.0]])],"derivedFrom":subQ3}),-1.0]])]});}
            var Q283;
            {var subQ0=sQuery(id+"F0.wireOp",EDGE,"E24.bottom");var subQ3=sQuery(id+"F0.wireOp",EDGE,"E13.left");var subQ4=makeQuery(id+"F0.imprint","INTERSECT",VERTEX,{"derivedFrom":[subQ3,subQ0]});Q283=makeQuery(id+"F0.imprint","IMPRINT",FACE,{"disambiguationData":[TD([[makeQuery(id+"F0.imprint","IMPRINT",EDGE,{"disambiguationData":[TD([[subQ4,-1.0]])],"derivedFrom":subQ3}),-1.0]])]});}
            var Q284;
            {var subQ0=sQuery(id+"F0.wireOp",EDGE,"E24.top");var subQ3=sQuery(id+"F0.wireOp",EDGE,"E13.left");var subQ4=makeQuery(id+"F0.imprint","INTERSECT",VERTEX,{"derivedFrom":[subQ3,subQ0]});Q284=makeQuery(id+"F0.imprint","IMPRINT",FACE,{"disambiguationData":[TD([[makeQuery(id+"F0.imprint","IMPRINT",EDGE,{"disambiguationData":[TD([[subQ4,-1.0]])],"derivedFrom":subQ3}),-1.0]])]});}
            var Q285;
            {var subQ0=sQuery(id+"F0.wireOp",EDGE,"E25.bottom");var subQ3=sQuery(id+"F0.wireOp",EDGE,"E13.left");var subQ4=makeQuery(id+"F0.imprint","INTERSECT",VERTEX,{"derivedFrom":[subQ3,subQ0]});Q285=makeQuery(id+"F0.imprint","IMPRINT",FACE,{"disambiguationData":[TD([[makeQuery(id+"F0.imprint","IMPRINT",EDGE,{"disambiguationData":[TD([[subQ4,-1.0]])],"derivedFrom":subQ3}),-1.0]])]});}
            var Q286;
            {var subQ0=sQuery(id+"F0.wireOp",EDGE,"E25.top");var subQ3=sQuery(id+"F0.wireOp",EDGE,"E13.left");var subQ4=makeQuery(id+"F0.imprint","INTERSECT",VERTEX,{"derivedFrom":[subQ3,subQ0]});Q286=makeQuery(id+"F0.imprint","IMPRINT",FACE,{"disambiguationData":[TD([[makeQuery(id+"F0.imprint","IMPRINT",EDGE,{"disambiguationData":[TD([[subQ4,-1.0]])],"derivedFrom":subQ3}),-1.0]])]});}
            var Q287;
            {var subQ3=sQuery(id+"F0.wireOp",EDGE,"E9.left");var subQ5=sQuery(id+"F0.wireOp",EDGE,"E25.bottom");var subQ7=makeQuery(id+"F0.imprint","INTERSECT",VERTEX,{"derivedFrom":[subQ3,subQ5]});Q287=makeQuery(id+"F0.imprint","IMPRINT",FACE,{"disambiguationData":[TD([[makeQuery(id+"F0.imprint","IMPRINT",EDGE,{"disambiguationData":[TD([[subQ7,-1.0]])],"derivedFrom":subQ3}),1.0]])]});}
            var Q288;
            {var subQ3=sQuery(id+"F0.wireOp",EDGE,"E9.right");var subQ5=sQuery(id+"F0.wireOp",EDGE,"E24.top");var subQ7=makeQuery(id+"F0.imprint","INTERSECT",VERTEX,{"derivedFrom":[subQ3,subQ5]});Q288=makeQuery(id+"F0.imprint","IMPRINT",FACE,{"disambiguationData":[TD([[makeQuery(id+"F0.imprint","IMPRINT",EDGE,{"disambiguationData":[TD([[subQ7,-1.0]])],"derivedFrom":subQ3}),1.0]])]});}
            var Q289;
            {var subQ3=sQuery(id+"F0.wireOp",EDGE,"E9.right");var subQ5=sQuery(id+"F0.wireOp",EDGE,"E23.top");var subQ7=makeQuery(id+"F0.imprint","INTERSECT",VERTEX,{"derivedFrom":[subQ3,subQ5]});Q289=makeQuery(id+"F0.imprint","IMPRINT",FACE,{"disambiguationData":[TD([[makeQuery(id+"F0.imprint","IMPRINT",EDGE,{"disambiguationData":[TD([[subQ7,-1.0]])],"derivedFrom":subQ3}),1.0]])]});}
            var Q290;
            {var subQ3=sQuery(id+"F0.wireOp",EDGE,"E11.left");var subQ5=sQuery(id+"F0.wireOp",EDGE,"E23.top");var subQ7=makeQuery(id+"F0.imprint","INTERSECT",VERTEX,{"derivedFrom":[subQ3,subQ5]});Q290=makeQuery(id+"F0.imprint","IMPRINT",FACE,{"disambiguationData":[TD([[makeQuery(id+"F0.imprint","IMPRINT",EDGE,{"disambiguationData":[TD([[subQ7,-1.0]])],"derivedFrom":subQ3}),1.0]])]});}
            var Q291;
            {var subQ3=sQuery(id+"F0.wireOp",EDGE,"E11.left");var subQ5=sQuery(id+"F0.wireOp",EDGE,"E24.bottom");var subQ7=makeQuery(id+"F0.imprint","INTERSECT",VERTEX,{"derivedFrom":[subQ3,subQ5]});Q291=makeQuery(id+"F0.imprint","IMPRINT",FACE,{"disambiguationData":[TD([[makeQuery(id+"F0.imprint","IMPRINT",EDGE,{"disambiguationData":[TD([[subQ7,-1.0]])],"derivedFrom":subQ3}),1.0]])]});}
            var Q292;
            {var subQ3=sQuery(id+"F0.wireOp",EDGE,"E11.left");var subQ5=sQuery(id+"F0.wireOp",EDGE,"E24.top");var subQ7=makeQuery(id+"F0.imprint","INTERSECT",VERTEX,{"derivedFrom":[subQ3,subQ5]});Q292=makeQuery(id+"F0.imprint","IMPRINT",FACE,{"disambiguationData":[TD([[makeQuery(id+"F0.imprint","IMPRINT",EDGE,{"disambiguationData":[TD([[subQ7,-1.0]])],"derivedFrom":subQ3}),1.0]])]});}
            var Q293;
            {var subQ3=sQuery(id+"F0.wireOp",EDGE,"E11.left");var subQ5=sQuery(id+"F0.wireOp",EDGE,"E25.bottom");var subQ7=makeQuery(id+"F0.imprint","INTERSECT",VERTEX,{"derivedFrom":[subQ3,subQ5]});Q293=makeQuery(id+"F0.imprint","IMPRINT",FACE,{"disambiguationData":[TD([[makeQuery(id+"F0.imprint","IMPRINT",EDGE,{"disambiguationData":[TD([[subQ7,-1.0]])],"derivedFrom":subQ3}),1.0]])]});}
            var Q294;
            {var subQ3=sQuery(id+"F0.wireOp",EDGE,"E9.right");var subQ5=sQuery(id+"F0.wireOp",EDGE,"E25.bottom");var subQ7=makeQuery(id+"F0.imprint","INTERSECT",VERTEX,{"derivedFrom":[subQ3,subQ5]});Q294=makeQuery(id+"F0.imprint","IMPRINT",FACE,{"disambiguationData":[TD([[makeQuery(id+"F0.imprint","IMPRINT",EDGE,{"disambiguationData":[TD([[subQ7,-1.0]])],"derivedFrom":subQ3}),1.0]])]});}
            var Q295;
            {var subQ3=sQuery(id+"F0.wireOp",EDGE,"E11.right");var subQ5=sQuery(id+"F0.wireOp",EDGE,"E25.bottom");var subQ7=makeQuery(id+"F0.imprint","INTERSECT",VERTEX,{"derivedFrom":[subQ3,subQ5]});Q295=makeQuery(id+"F0.imprint","IMPRINT",FACE,{"disambiguationData":[TD([[makeQuery(id+"F0.imprint","IMPRINT",EDGE,{"disambiguationData":[TD([[subQ7,-1.0]])],"derivedFrom":subQ3}),1.0]])]});}
            var Q296;
            {var subQ3=sQuery(id+"F0.wireOp",EDGE,"E11.right");var subQ5=sQuery(id+"F0.wireOp",EDGE,"E25.top");var subQ7=makeQuery(id+"F0.imprint","INTERSECT",VERTEX,{"derivedFrom":[subQ3,subQ5]});Q296=makeQuery(id+"F0.imprint","IMPRINT",FACE,{"disambiguationData":[TD([[makeQuery(id+"F0.imprint","IMPRINT",EDGE,{"disambiguationData":[TD([[subQ7,-1.0]])],"derivedFrom":subQ3}),1.0]])]});}
            var Q297;
            {var subQ3=sQuery(id+"F0.wireOp",EDGE,"E12.left");var subQ5=sQuery(id+"F0.wireOp",EDGE,"E25.bottom");var subQ7=makeQuery(id+"F0.imprint","INTERSECT",VERTEX,{"derivedFrom":[subQ3,subQ5]});Q297=makeQuery(id+"F0.imprint","IMPRINT",FACE,{"disambiguationData":[TD([[makeQuery(id+"F0.imprint","IMPRINT",EDGE,{"disambiguationData":[TD([[subQ7,-1.0]])],"derivedFrom":subQ3}),1.0]])]});}
            var Q298;
            {var subQ3=sQuery(id+"F0.wireOp",EDGE,"E12.left");var subQ5=sQuery(id+"F0.wireOp",EDGE,"E25.top");var subQ7=makeQuery(id+"F0.imprint","INTERSECT",VERTEX,{"derivedFrom":[subQ3,subQ5]});Q298=makeQuery(id+"F0.imprint","IMPRINT",FACE,{"disambiguationData":[TD([[makeQuery(id+"F0.imprint","IMPRINT",EDGE,{"disambiguationData":[TD([[subQ7,-1.0]])],"derivedFrom":subQ3}),1.0]])]});}
            var Q299;
            {var subQ3=sQuery(id+"F0.wireOp",EDGE,"E12.right");var subQ5=sQuery(id+"F0.wireOp",EDGE,"E25.bottom");var subQ7=makeQuery(id+"F0.imprint","INTERSECT",VERTEX,{"derivedFrom":[subQ3,subQ5]});Q299=makeQuery(id+"F0.imprint","IMPRINT",FACE,{"disambiguationData":[TD([[makeQuery(id+"F0.imprint","IMPRINT",EDGE,{"disambiguationData":[TD([[subQ7,-1.0]])],"derivedFrom":subQ3}),1.0]])]});}
            var Q300;
            {var subQ3=sQuery(id+"F0.wireOp",EDGE,"E12.right");var subQ5=sQuery(id+"F0.wireOp",EDGE,"E25.top");var subQ7=makeQuery(id+"F0.imprint","INTERSECT",VERTEX,{"derivedFrom":[subQ3,subQ5]});Q300=makeQuery(id+"F0.imprint","IMPRINT",FACE,{"disambiguationData":[TD([[makeQuery(id+"F0.imprint","IMPRINT",EDGE,{"disambiguationData":[TD([[subQ7,-1.0]])],"derivedFrom":subQ3}),1.0]])]});}
            var Q301;
            {var subQ3=sQuery(id+"F0.wireOp",EDGE,"E12.right");var subQ5=sQuery(id+"F0.wireOp",EDGE,"E26.bottom");var subQ7=makeQuery(id+"F0.imprint","INTERSECT",VERTEX,{"derivedFrom":[subQ3,subQ5]});Q301=makeQuery(id+"F0.imprint","IMPRINT",FACE,{"disambiguationData":[TD([[makeQuery(id+"F0.imprint","IMPRINT",EDGE,{"disambiguationData":[TD([[subQ7,-1.0]])],"derivedFrom":subQ3}),1.0]])]});}
            var Q302;
            {var subQ3=sQuery(id+"F0.wireOp",EDGE,"E12.right");var subQ5=sQuery(id+"F0.wireOp",EDGE,"E26.top");var subQ7=makeQuery(id+"F0.imprint","INTERSECT",VERTEX,{"derivedFrom":[subQ3,subQ5]});Q302=makeQuery(id+"F0.imprint","IMPRINT",FACE,{"disambiguationData":[TD([[makeQuery(id+"F0.imprint","IMPRINT",EDGE,{"disambiguationData":[TD([[subQ7,-1.0]])],"derivedFrom":subQ3}),1.0]])]});}
            var Q303;
            {var subQ0=sQuery(id+"F0.wireOp",EDGE,"E27.bottom");var subQ3=sQuery(id+"F0.wireOp",EDGE,"E13.left");var subQ4=makeQuery(id+"F0.imprint","INTERSECT",VERTEX,{"derivedFrom":[subQ3,subQ0]});Q303=makeQuery(id+"F0.imprint","IMPRINT",FACE,{"disambiguationData":[TD([[makeQuery(id+"F0.imprint","IMPRINT",EDGE,{"disambiguationData":[TD([[subQ4,-1.0]])],"derivedFrom":subQ3}),-1.0]])]});}
            var Q304;
            {var subQ0=sQuery(id+"F0.wireOp",EDGE,"E27.bottom");var subQ3=sQuery(id+"F0.wireOp",EDGE,"E13.right");var subQ4=makeQuery(id+"F0.imprint","INTERSECT",VERTEX,{"derivedFrom":[subQ3,subQ0]});Q304=makeQuery(id+"F0.imprint","IMPRINT",FACE,{"disambiguationData":[TD([[makeQuery(id+"F0.imprint","IMPRINT",EDGE,{"disambiguationData":[TD([[subQ4,-1.0]])],"derivedFrom":subQ3}),-1.0]])]});}
            var Q305;
            {var subQ3=sQuery(id+"F0.wireOp",EDGE,"E25.top");var subQ5=sQuery(id+"F0.wireOp",EDGE,"E14.right");var subQ7=makeQuery(id+"F0.imprint","INTERSECT",VERTEX,{"derivedFrom":[subQ5,subQ3]});Q305=makeQuery(id+"F0.imprint","IMPRINT",FACE,{"disambiguationData":[TD([[makeQuery(id+"F0.imprint","IMPRINT",EDGE,{"disambiguationData":[TD([[subQ7,-1.0]])],"derivedFrom":subQ5}),1.0]])]});}
            var Q306;
            {var subQ3=sQuery(id+"F0.wireOp",EDGE,"E14.left");var subQ5=sQuery(id+"F0.wireOp",EDGE,"E25.top");var subQ7=makeQuery(id+"F0.imprint","INTERSECT",VERTEX,{"derivedFrom":[subQ3,subQ5]});Q306=makeQuery(id+"F0.imprint","IMPRINT",FACE,{"disambiguationData":[TD([[makeQuery(id+"F0.imprint","IMPRINT",EDGE,{"disambiguationData":[TD([[subQ7,-1.0]])],"derivedFrom":subQ3}),1.0]])]});}
            var Q307;
            {var subQ0=sQuery(id+"F0.wireOp",EDGE,"E26.bottom");var subQ3=sQuery(id+"F0.wireOp",EDGE,"E13.left");var subQ4=makeQuery(id+"F0.imprint","INTERSECT",VERTEX,{"derivedFrom":[subQ3,subQ0]});Q307=makeQuery(id+"F0.imprint","IMPRINT",FACE,{"disambiguationData":[TD([[makeQuery(id+"F0.imprint","IMPRINT",EDGE,{"disambiguationData":[TD([[subQ4,-1.0]])],"derivedFrom":subQ3}),-1.0]])]});}
            var Q308;
            {var subQ0=sQuery(id+"F0.wireOp",EDGE,"E25.top");var subQ3=sQuery(id+"F0.wireOp",EDGE,"E13.right");var subQ4=makeQuery(id+"F0.imprint","INTERSECT",VERTEX,{"derivedFrom":[subQ3,subQ0]});Q308=makeQuery(id+"F0.imprint","IMPRINT",FACE,{"disambiguationData":[TD([[makeQuery(id+"F0.imprint","IMPRINT",EDGE,{"disambiguationData":[TD([[subQ4,-1.0]])],"derivedFrom":subQ3}),-1.0]])]});}
            var Q309;
            {var subQ0=sQuery(id+"F0.wireOp",EDGE,"E25.bottom");var subQ3=sQuery(id+"F0.wireOp",EDGE,"E14.left");var subQ4=makeQuery(id+"F0.imprint","INTERSECT",VERTEX,{"derivedFrom":[subQ3,subQ0]});Q309=makeQuery(id+"F0.imprint","IMPRINT",FACE,{"disambiguationData":[TD([[makeQuery(id+"F0.imprint","IMPRINT",EDGE,{"disambiguationData":[TD([[subQ4,-1.0]])],"derivedFrom":subQ3}),1.0]])]});}
            var Q310;
            {var subQ3=sQuery(id+"F0.wireOp",EDGE,"E25.bottom");var subQ5=sQuery(id+"F0.wireOp",EDGE,"E14.right");var subQ7=makeQuery(id+"F0.imprint","INTERSECT",VERTEX,{"derivedFrom":[subQ5,subQ3]});Q310=makeQuery(id+"F0.imprint","IMPRINT",FACE,{"disambiguationData":[TD([[makeQuery(id+"F0.imprint","IMPRINT",EDGE,{"disambiguationData":[TD([[subQ7,-1.0]])],"derivedFrom":subQ5}),1.0]])]});}
            var Q311;
            {var subQ3=sQuery(id+"F0.wireOp",EDGE,"E24.top");var subQ5=sQuery(id+"F0.wireOp",EDGE,"E14.right");var subQ7=makeQuery(id+"F0.imprint","INTERSECT",VERTEX,{"derivedFrom":[subQ5,subQ3]});Q311=makeQuery(id+"F0.imprint","IMPRINT",FACE,{"disambiguationData":[TD([[makeQuery(id+"F0.imprint","IMPRINT",EDGE,{"disambiguationData":[TD([[subQ7,-1.0]])],"derivedFrom":subQ5}),1.0]])]});}
            var Q312;
            {var subQ3=sQuery(id+"F0.wireOp",EDGE,"E14.left");var subQ5=sQuery(id+"F0.wireOp",EDGE,"E24.top");var subQ7=makeQuery(id+"F0.imprint","INTERSECT",VERTEX,{"derivedFrom":[subQ3,subQ5]});Q312=makeQuery(id+"F0.imprint","IMPRINT",FACE,{"disambiguationData":[TD([[makeQuery(id+"F0.imprint","IMPRINT",EDGE,{"disambiguationData":[TD([[subQ7,-1.0]])],"derivedFrom":subQ3}),1.0]])]});}
            var Q313;
            {var subQ3=sQuery(id+"F0.wireOp",EDGE,"E13.right");var subQ5=sQuery(id+"F0.wireOp",EDGE,"E25.bottom");var subQ7=makeQuery(id+"F0.imprint","INTERSECT",VERTEX,{"derivedFrom":[subQ3,subQ5]});Q313=makeQuery(id+"F0.imprint","IMPRINT",FACE,{"disambiguationData":[TD([[makeQuery(id+"F0.imprint","IMPRINT",EDGE,{"disambiguationData":[TD([[subQ7,-1.0]])],"derivedFrom":subQ3}),-1.0]])]});}
            var Q314;
            {var subQ3=sQuery(id+"F0.wireOp",EDGE,"E13.right");var subQ5=sQuery(id+"F0.wireOp",EDGE,"E24.top");var subQ7=makeQuery(id+"F0.imprint","INTERSECT",VERTEX,{"derivedFrom":[subQ3,subQ5]});Q314=makeQuery(id+"F0.imprint","IMPRINT",FACE,{"disambiguationData":[TD([[makeQuery(id+"F0.imprint","IMPRINT",EDGE,{"disambiguationData":[TD([[subQ7,-1.0]])],"derivedFrom":subQ3}),-1.0]])]});}
            var Q315;
            {var subQ3=sQuery(id+"F0.wireOp",EDGE,"E12.left");var subQ5=sQuery(id+"F0.wireOp",EDGE,"E24.bottom");var subQ7=makeQuery(id+"F0.imprint","INTERSECT",VERTEX,{"derivedFrom":[subQ3,subQ5]});Q315=makeQuery(id+"F0.imprint","IMPRINT",FACE,{"disambiguationData":[TD([[makeQuery(id+"F0.imprint","IMPRINT",EDGE,{"disambiguationData":[TD([[subQ7,-1.0]])],"derivedFrom":subQ3}),1.0]])]});}
            var Q316;
            {var subQ3=sQuery(id+"F0.wireOp",EDGE,"E12.right");var subQ5=sQuery(id+"F0.wireOp",EDGE,"E23.bottom");var subQ7=makeQuery(id+"F0.imprint","INTERSECT",VERTEX,{"derivedFrom":[subQ3,subQ5]});Q316=makeQuery(id+"F0.imprint","IMPRINT",FACE,{"disambiguationData":[TD([[makeQuery(id+"F0.imprint","IMPRINT",EDGE,{"disambiguationData":[TD([[subQ7,-1.0]])],"derivedFrom":subQ3}),1.0]])]});}
            var Q317;
            {var subQ3=sQuery(id+"F0.wireOp",EDGE,"E12.left");var subQ5=sQuery(id+"F0.wireOp",EDGE,"E23.bottom");var subQ7=makeQuery(id+"F0.imprint","INTERSECT",VERTEX,{"derivedFrom":[subQ3,subQ5]});Q317=makeQuery(id+"F0.imprint","IMPRINT",FACE,{"disambiguationData":[TD([[makeQuery(id+"F0.imprint","IMPRINT",EDGE,{"disambiguationData":[TD([[subQ7,-1.0]])],"derivedFrom":subQ3}),1.0]])]});}
            var Q318;
            {var subQ3=sQuery(id+"F0.wireOp",EDGE,"E11.left");var subQ5=sQuery(id+"F0.wireOp",EDGE,"E23.bottom");var subQ7=makeQuery(id+"F0.imprint","INTERSECT",VERTEX,{"derivedFrom":[subQ3,subQ5]});Q318=makeQuery(id+"F0.imprint","IMPRINT",FACE,{"disambiguationData":[TD([[makeQuery(id+"F0.imprint","IMPRINT",EDGE,{"disambiguationData":[TD([[subQ7,-1.0]])],"derivedFrom":subQ3}),1.0]])]});}
            var Q319;
            {var subQ0=sQuery(id+"F0.wireOp",EDGE,"E22.top");var subQ3=sQuery(id+"F0.wireOp",EDGE,"E11.left");var subQ4=makeQuery(id+"F0.imprint","INTERSECT",VERTEX,{"derivedFrom":[subQ3,subQ0]});Q319=makeQuery(id+"F0.imprint","IMPRINT",FACE,{"disambiguationData":[TD([[makeQuery(id+"F0.imprint","IMPRINT",EDGE,{"disambiguationData":[TD([[subQ4,-1.0]])],"derivedFrom":subQ3}),1.0]])]});}
            var Q320;
            {var subQ3=sQuery(id+"F0.wireOp",EDGE,"E11.left");var subQ5=sQuery(id+"F0.wireOp",EDGE,"E22.bottom");var subQ7=makeQuery(id+"F0.imprint","INTERSECT",VERTEX,{"derivedFrom":[subQ3,subQ5]});Q320=makeQuery(id+"F0.imprint","IMPRINT",FACE,{"disambiguationData":[TD([[makeQuery(id+"F0.imprint","IMPRINT",EDGE,{"disambiguationData":[TD([[subQ7,-1.0]])],"derivedFrom":subQ3}),1.0]])]});}
            var Q321;
            {var subQ3=sQuery(id+"F0.wireOp",EDGE,"E9.right");var subQ5=sQuery(id+"F0.wireOp",EDGE,"E22.bottom");var subQ7=makeQuery(id+"F0.imprint","INTERSECT",VERTEX,{"derivedFrom":[subQ3,subQ5]});Q321=makeQuery(id+"F0.imprint","IMPRINT",FACE,{"disambiguationData":[TD([[makeQuery(id+"F0.imprint","IMPRINT",EDGE,{"disambiguationData":[TD([[subQ7,-1.0]])],"derivedFrom":subQ3}),1.0]])]});}
            var Q322;
            {var subQ3=sQuery(id+"F0.wireOp",EDGE,"E11.left");var subQ5=sQuery(id+"F0.wireOp",EDGE,"E21.top");var subQ7=makeQuery(id+"F0.imprint","INTERSECT",VERTEX,{"derivedFrom":[subQ3,subQ5]});Q322=makeQuery(id+"F0.imprint","IMPRINT",FACE,{"disambiguationData":[TD([[makeQuery(id+"F0.imprint","IMPRINT",EDGE,{"disambiguationData":[TD([[subQ7,-1.0]])],"derivedFrom":subQ3}),1.0]])]});}
            var Q323;
            {var subQ3=sQuery(id+"F0.wireOp",EDGE,"E11.right");var subQ5=sQuery(id+"F0.wireOp",EDGE,"E22.bottom");var subQ7=makeQuery(id+"F0.imprint","INTERSECT",VERTEX,{"derivedFrom":[subQ3,subQ5]});Q323=makeQuery(id+"F0.imprint","IMPRINT",FACE,{"disambiguationData":[TD([[makeQuery(id+"F0.imprint","IMPRINT",EDGE,{"disambiguationData":[TD([[subQ7,-1.0]])],"derivedFrom":subQ3}),1.0]])]});}
            var Q324;
            {var subQ0=sQuery(id+"F0.wireOp",EDGE,"E88.right");var subQ3=sQuery(id+"F0.wireOp",EDGE,"E15.top");var subQ4=makeQuery(id+"F0.imprint","INTERSECT",VERTEX,{"derivedFrom":[subQ3,subQ0]});Q324=makeQuery(id+"F0.imprint","IMPRINT",FACE,{"disambiguationData":[TD([[makeQuery(id+"F0.imprint","IMPRINT",EDGE,{"disambiguationData":[TD([[subQ4,1.0]])],"derivedFrom":subQ3}),-1.0]])]});}
            var Q325;
            {var subQ0=sQuery(id+"F0.wireOp",EDGE,"E88.right");var subQ3=sQuery(id+"F0.wireOp",EDGE,"E16.bottom");var subQ4=makeQuery(id+"F0.imprint","INTERSECT",VERTEX,{"derivedFrom":[subQ3,subQ0]});Q325=makeQuery(id+"F0.imprint","IMPRINT",FACE,{"disambiguationData":[TD([[makeQuery(id+"F0.imprint","IMPRINT",EDGE,{"disambiguationData":[TD([[subQ4,-1.0]])],"derivedFrom":subQ3}),1.0]])]});}
            var Q326;
            {var subQ0=sQuery(id+"F0.wireOp",EDGE,"E88.right");var subQ3=sQuery(id+"F0.wireOp",EDGE,"E16.top");var subQ4=makeQuery(id+"F0.imprint","INTERSECT",VERTEX,{"derivedFrom":[subQ3,subQ0]});Q326=makeQuery(id+"F0.imprint","IMPRINT",FACE,{"disambiguationData":[TD([[makeQuery(id+"F0.imprint","IMPRINT",EDGE,{"disambiguationData":[TD([[subQ4,-1.0]])],"derivedFrom":subQ3}),1.0]])]});}
            var Q327;
            {var subQ0=sQuery(id+"F0.wireOp",EDGE,"E88.right");var subQ3=sQuery(id+"F0.wireOp",EDGE,"E17.bottom");var subQ4=makeQuery(id+"F0.imprint","INTERSECT",VERTEX,{"derivedFrom":[subQ3,subQ0]});Q327=makeQuery(id+"F0.imprint","IMPRINT",FACE,{"disambiguationData":[TD([[makeQuery(id+"F0.imprint","IMPRINT",EDGE,{"disambiguationData":[TD([[subQ4,1.0]])],"derivedFrom":subQ3}),-1.0]])]});}
            var Q328;
            {var subQ0=sQuery(id+"F0.wireOp",EDGE,"E88.right");var subQ3=sQuery(id+"F0.wireOp",EDGE,"E17.top");var subQ4=makeQuery(id+"F0.imprint","INTERSECT",VERTEX,{"derivedFrom":[subQ3,subQ0]});Q328=makeQuery(id+"F0.imprint","IMPRINT",FACE,{"disambiguationData":[TD([[makeQuery(id+"F0.imprint","IMPRINT",EDGE,{"disambiguationData":[TD([[subQ4,1.0]])],"derivedFrom":subQ3}),-1.0]])]});}
            extrude(context, id + "F1", {"entities" : qUnion([Q0, Q1, Q2, Q3, Q4, Q5, Q6, Q7, Q8, Q9, Q10, Q11, Q12, Q13, Q14, Q15, Q16, Q17, Q18, Q19, Q20, Q21, Q22, Q23, Q24, Q25, Q26, Q27, Q28, Q29, Q30, Q31, Q32, Q33, Q34, Q35, Q36, Q37, Q38, Q39, Q40, Q41, Q42, Q43, Q44, Q45, Q46, Q47, Q48, Q49, Q50, Q51, Q52, Q53, Q54, Q55, Q56, Q57, Q58, Q59, Q60, Q61, Q62, Q63, Q64, Q65, Q66, Q67, Q68, Q69, Q70, Q71, Q72, Q73, Q74, Q75, Q76, Q77, Q78, Q79, Q80, Q81, Q82, Q83, Q84, Q85, Q86, Q87, Q88, Q89, Q90, Q91, Q92, Q93, Q94, Q95, Q96, Q97, Q98, Q99, Q100, Q101, Q102, Q103, Q104, Q105, Q106, Q107, Q108, Q109, Q110, Q111, Q112, Q113, Q114, Q115, Q116, Q117, Q118, Q119, Q120, Q121, Q122, Q123, Q124, Q125, Q126, Q127, Q128, Q129, Q130, Q131, Q132, Q133, Q134, Q135, Q136, Q137, Q138, Q139, Q140, Q141, Q142, Q143, Q144, Q145, Q146, Q147, Q148, Q149, Q150, Q151, Q152, Q153, Q154, Q155, Q156, Q157, Q158, Q159, Q160, Q161, Q162, Q163, Q164, Q165, Q166, Q167, Q168, Q169, Q170, Q171, Q172, Q173, Q174, Q175, Q176, Q177, Q178, Q179, Q180, Q181, Q182, Q183, Q184, Q185, Q186, Q187, Q188, Q189, Q190, Q191, Q192, Q193, Q194, Q195, Q196, Q197, Q198, Q199, Q200, Q201, Q202, Q203, Q204, Q205, Q206, Q207, Q208, Q209, Q210, Q211, Q212, Q213, Q214, Q215, Q216, Q217, Q218, Q219, Q220, Q221, Q222, Q223, Q224, Q225, Q226, Q227, Q228, Q229, Q230, Q231, Q232, Q233, Q234, Q235, Q236, Q237, Q238, Q239, Q240, Q241, Q242, Q243, Q244, Q245, Q246, Q247, Q248, Q249, Q250, Q251, Q252, Q253, Q254, Q255, Q256, Q257, Q258, Q259, Q260, Q261, Q262, Q263, Q264, Q265, Q266, Q267, Q268, Q269, Q270, Q271, Q272, Q273, Q274, Q275, Q276, Q277, Q278, Q279, Q280, Q281, Q282, Q283, Q284, Q285, Q286, Q287, Q288, Q289, Q290, Q291, Q292, Q293, Q294, Q295, Q296, Q297, Q298, Q299, Q300, Q301, Q302, Q303, Q304, Q305, Q306, Q307, Q308, Q309, Q310, Q311, Q312, Q313, Q314, Q315, Q316, Q317, Q318, Q319, Q320, Q321, Q322, Q323, Q324, Q325, Q326, Q327, Q328]), "depth" : 25.4 * mm});
        }
        {
            var Q0;
            {var subQ3=sQuery(id+"F0.wireOp",EDGE,"E14.left");var subQ5=sQuery(id+"F0.wireOp",EDGE,"E26.bottom");var subQ7=makeQuery(id+"F0.imprint","INTERSECT",VERTEX,{"derivedFrom":[subQ3,subQ5]});Q0=makeQuery(id+"F0.imprint","IMPRINT",FACE,{"disambiguationData":[TD([[makeQuery(id+"F0.imprint","IMPRINT",EDGE,{"disambiguationData":[TD([[subQ7,-1.0]])],"derivedFrom":subQ3}),1.0]])]});}
            var Q1;
            {var subQ3=sQuery(id+"F0.wireOp",EDGE,"E11.right");var subQ5=sQuery(id+"F0.wireOp",EDGE,"E23.bottom");var subQ7=makeQuery(id+"F0.imprint","INTERSECT",VERTEX,{"derivedFrom":[subQ3,subQ5]});Q1=makeQuery(id+"F0.imprint","IMPRINT",FACE,{"disambiguationData":[TD([[makeQuery(id+"F0.imprint","IMPRINT",EDGE,{"disambiguationData":[TD([[subQ7,-1.0]])],"derivedFrom":subQ3}),1.0]])]});}
            var Q2;
            {var subQ3=sQuery(id+"F0.wireOp",EDGE,"E19.top");var subQ5=sQuery(id+"F0.wireOp",EDGE,"E5.left");var subQ7=makeQuery(id+"F0.imprint","INTERSECT",VERTEX,{"derivedFrom":[subQ5,subQ3]});Q2=makeQuery(id+"F0.imprint","IMPRINT",FACE,{"disambiguationData":[TD([[makeQuery(id+"F0.imprint","IMPRINT",EDGE,{"disambiguationData":[TD([[subQ7,-1.0]])],"derivedFrom":subQ5}),-1.0]])]});}
            extrude(context, id + "F2", {"entities" : qUnion([Q0, Q1, Q2]), "depth" : 25.4 * mm});
        }
    });
